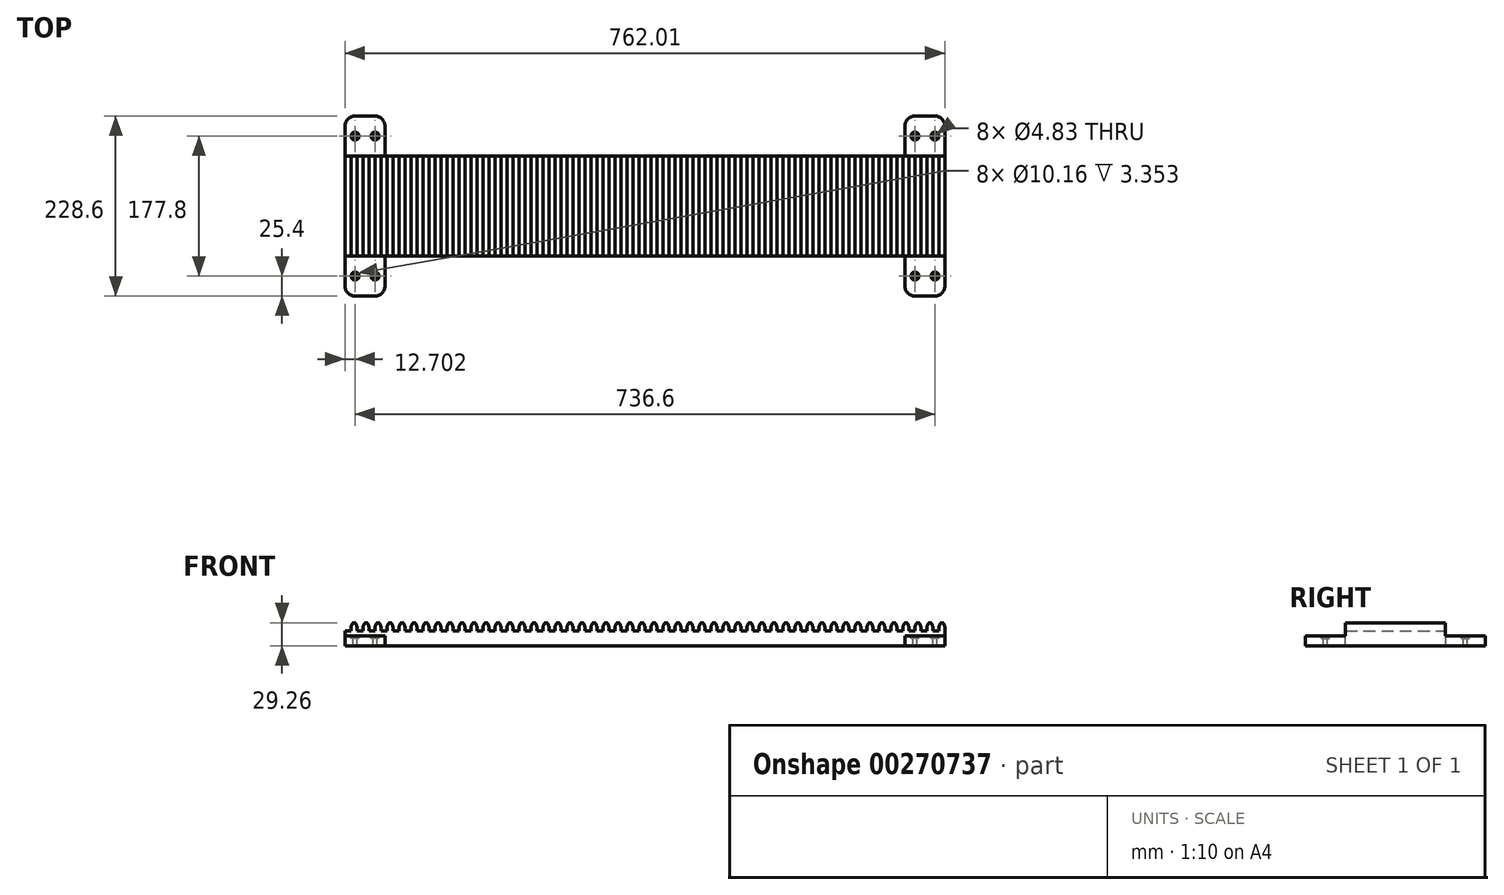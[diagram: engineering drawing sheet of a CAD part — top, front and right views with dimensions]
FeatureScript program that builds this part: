
annotation { "Feature Type Name" : "Feature", "Feature Type Description" : "" }
export const myFeature = defineFeature(function(context is Context, id is Id, definition is map)
    precondition{}
    {
        {
            var Q0;
            Q0=qCreatedBy(makeId("Front.planeOp"),FACE);
            var sketch = newSketch(context, id + "F0", { "sketchPlane" : qUnion([Q0])});
            skPoint(sketch, "E0.orphan", {"position": v(0.2, 56.91) * mm});
            skPoint(sketch, "E1.orphan", {"position": v(-3.78, 56.79) * mm});
            skArc(sketch, "E2.MirrorCS", {"start": v(-11.95, 74.44) * mm, "mid": v(-11.17, 76.23) * mm, "end": v(-10.29, 77.97) * mm});
            skArc(sketch, "E3.MirrorCS", {"start": v(-5.23, 74.46) * mm, "mid": v(-6, 76.24) * mm, "end": v(-6.88, 77.97) * mm});
            skPoint(sketch, "E4.orphan", {"position": v(-4.82, 78.33) * mm});
            skPoint(sketch, "E5.orphan", {"position": v(-12.38, 78.33) * mm});
            skPoint(sketch, "E6.visualSharp", {"position": v(-12.4, 73.25) * mm});
            skArc(sketch, "E6.filletArc", {"start": v(-11.95, 74.44) * mm, "mid": v(-12.28, 73.3) * mm, "end": v(-12.4, 72.11) * mm});
            skPoint(sketch, "E7.visualSharp", {"position": v(-4.77, 73.25) * mm});
            skArc(sketch, "E7.filletArc", {"start": v(-4.78, 72.1) * mm, "mid": v(-4.89, 73.3) * mm, "end": v(-5.23, 74.46) * mm});
            skPoint(sketch, "E8.visualSharp", {"position": v(-10.06, 78.38) * mm});
            skArc(sketch, "E8.filletArc", {"start": v(-9.6, 78.38) * mm, "mid": v(-10, 78.27) * mm, "end": v(-10.29, 77.97) * mm});
            skPoint(sketch, "E9.visualSharp", {"position": v(-7.1, 78.38) * mm});
            skArc(sketch, "E9.filletArc", {"start": v(-6.88, 77.97) * mm, "mid": v(-7.17, 78.27) * mm, "end": v(-7.57, 78.38) * mm});
            skLineSegment(sketch, "E10", {"start": v(-4.78, 72.1) * mm, "end": v(-4.79, 68.17) * mm});
            skLineSegment(sketch, "E11", {"start": v(-12.4, 72.11) * mm, "end": v(-12.4, 68.17) * mm});
            skLineSegment(sketch, "E12", {"start": v(-9.6, 78.38) * mm, "end": v(-7.57, 78.38) * mm});
            skLineSegment(sketch, "E13", {"start": v(-12.4, 68.17) * mm, "end": v(-4.79, 68.17) * mm});
            skPoint(sketch, "E14.orphan", {"position": v(-14.13, 68.17) * mm});
            skLineSegment(sketch, "E15", {"start": v(-12.4, 68.17) * mm, "end": v(2.83, 68.17) * mm});
            skPoint(sketch, "E16.1.0.0", {"position": v(5.18, 78.38) * mm});
            skArc(sketch, "E16.1.0.1", {"start": v(10.01, 74.46) * mm, "mid": v(9.24, 76.24) * mm, "end": v(8.36, 77.97) * mm});
            skArc(sketch, "E16.1.0.2", {"start": v(3.3, 74.44) * mm, "mid": v(4.07, 76.23) * mm, "end": v(4.95, 77.97) * mm});
            skPoint(sketch, "E16.1.0.3", {"position": v(10.42, 78.33) * mm});
            skPoint(sketch, "E16.1.0.4", {"position": v(2.85, 73.25) * mm});
            skPoint(sketch, "E16.1.0.5", {"position": v(10.47, 73.25) * mm});
            skPoint(sketch, "E16.1.0.6", {"position": v(1.11, 68.17) * mm});
            skLineSegment(sketch, "E16.1.0.7", {"start": v(5.64, 78.38) * mm, "end": v(7.67, 78.38) * mm});
            skPoint(sketch, "E16.1.0.8", {"position": v(8.13, 78.38) * mm});
            skLineSegment(sketch, "E16.1.0.9", {"start": v(10.46, 72.1) * mm, "end": v(10.45, 68.17) * mm});
            skLineSegment(sketch, "E16.1.0.10", {"start": v(2.83, 68.17) * mm, "end": v(18.07, 68.17) * mm});
            skPoint(sketch, "E16.1.0.11", {"position": v(2.86, 78.33) * mm});
            skLineSegment(sketch, "E16.1.0.12", {"start": v(2.84, 72.11) * mm, "end": v(2.83, 68.17) * mm});
            skArc(sketch, "E16.1.0.13", {"start": v(10.46, 72.1) * mm, "mid": v(10.35, 73.3) * mm, "end": v(10.01, 74.46) * mm});
            skArc(sketch, "E16.1.0.14", {"start": v(3.3, 74.44) * mm, "mid": v(2.96, 73.3) * mm, "end": v(2.84, 72.11) * mm});
            skLineSegment(sketch, "E16.1.0.15", {"start": v(2.83, 68.17) * mm, "end": v(10.45, 68.17) * mm});
            skArc(sketch, "E16.1.0.16", {"start": v(8.36, 77.97) * mm, "mid": v(8.07, 78.27) * mm, "end": v(7.67, 78.38) * mm});
            skArc(sketch, "E16.1.0.17", {"start": v(5.64, 78.38) * mm, "mid": v(5.24, 78.27) * mm, "end": v(4.95, 77.97) * mm});
            skPoint(sketch, "E16.2.0.0", {"position": v(20.42, 78.38) * mm});
            skArc(sketch, "E16.2.0.1", {"start": v(25.25, 74.46) * mm, "mid": v(24.48, 76.24) * mm, "end": v(23.6, 77.97) * mm});
            skArc(sketch, "E16.2.0.2", {"start": v(18.53, 74.44) * mm, "mid": v(19.3, 76.23) * mm, "end": v(20.2, 77.97) * mm});
            skPoint(sketch, "E16.2.0.3", {"position": v(25.66, 78.33) * mm});
            skPoint(sketch, "E16.2.0.4", {"position": v(18.09, 73.25) * mm});
            skPoint(sketch, "E16.2.0.5", {"position": v(25.7, 73.25) * mm});
            skPoint(sketch, "E16.2.0.6", {"position": v(16.35, 68.17) * mm});
            skLineSegment(sketch, "E16.2.0.7", {"start": v(20.88, 78.38) * mm, "end": v(22.9, 78.38) * mm});
            skPoint(sketch, "E16.2.0.8", {"position": v(23.37, 78.38) * mm});
            skLineSegment(sketch, "E16.2.0.9", {"start": v(25.7, 72.1) * mm, "end": v(25.7, 68.17) * mm});
            skLineSegment(sketch, "E16.2.0.10", {"start": v(18.07, 68.17) * mm, "end": v(33.31, 68.17) * mm});
            skPoint(sketch, "E16.2.0.11", {"position": v(18.1, 78.33) * mm});
            skLineSegment(sketch, "E16.2.0.12", {"start": v(18.08, 72.11) * mm, "end": v(18.07, 68.17) * mm});
            skArc(sketch, "E16.2.0.13", {"start": v(25.7, 72.1) * mm, "mid": v(25.6, 73.3) * mm, "end": v(25.25, 74.46) * mm});
            skArc(sketch, "E16.2.0.14", {"start": v(18.53, 74.44) * mm, "mid": v(18.2, 73.3) * mm, "end": v(18.08, 72.11) * mm});
            skLineSegment(sketch, "E16.2.0.15", {"start": v(18.07, 68.17) * mm, "end": v(25.7, 68.17) * mm});
            skArc(sketch, "E16.2.0.16", {"start": v(23.6, 77.97) * mm, "mid": v(23.31, 78.27) * mm, "end": v(22.9, 78.38) * mm});
            skArc(sketch, "E16.2.0.17", {"start": v(20.88, 78.38) * mm, "mid": v(20.48, 78.27) * mm, "end": v(20.2, 77.97) * mm});
            skPoint(sketch, "E17.0.3.0", {"position": v(35.66, 78.38) * mm});
            skArc(sketch, "E17.1.3.0", {"start": v(40.5, 74.46) * mm, "mid": v(39.72, 76.24) * mm, "end": v(38.84, 77.97) * mm});
            skArc(sketch, "E17.5.3.0", {"start": v(33.77, 74.44) * mm, "mid": v(34.55, 76.23) * mm, "end": v(35.43, 77.97) * mm});
            skPoint(sketch, "E17.9.3.0", {"position": v(40.9, 78.33) * mm});
            skPoint(sketch, "E17.10.3.0", {"position": v(33.33, 73.25) * mm});
            skPoint(sketch, "E17.11.3.0", {"position": v(40.95, 73.25) * mm});
            skPoint(sketch, "E17.12.3.0", {"position": v(31.6, 68.17) * mm});
            skLineSegment(sketch, "E17.13.3.0", {"start": v(36.12, 78.38) * mm, "end": v(38.15, 78.38) * mm});
            skPoint(sketch, "E17.16.3.0", {"position": v(38.61, 78.38) * mm});
            skLineSegment(sketch, "E17.17.3.0", {"start": v(40.94, 72.1) * mm, "end": v(40.93, 68.17) * mm});
            skLineSegment(sketch, "E17.20.3.0", {"start": v(33.31, 68.17) * mm, "end": v(48.55, 68.17) * mm});
            skPoint(sketch, "E17.23.3.0", {"position": v(33.34, 78.33) * mm});
            skLineSegment(sketch, "E17.24.3.0", {"start": v(33.32, 72.11) * mm, "end": v(33.31, 68.17) * mm});
            skArc(sketch, "E17.27.3.0", {"start": v(40.94, 72.1) * mm, "mid": v(40.83, 73.3) * mm, "end": v(40.5, 74.46) * mm});
            skArc(sketch, "E17.31.3.0", {"start": v(33.77, 74.44) * mm, "mid": v(33.44, 73.3) * mm, "end": v(33.32, 72.11) * mm});
            skLineSegment(sketch, "E17.35.3.0", {"start": v(33.31, 68.17) * mm, "end": v(40.93, 68.17) * mm});
            skArc(sketch, "E17.38.3.0", {"start": v(38.84, 77.97) * mm, "mid": v(38.55, 78.27) * mm, "end": v(38.15, 78.38) * mm});
            skArc(sketch, "E17.42.3.0", {"start": v(36.12, 78.38) * mm, "mid": v(35.72, 78.27) * mm, "end": v(35.43, 77.97) * mm});
            skPoint(sketch, "E17.0.4.0", {"position": v(50.9, 78.38) * mm});
            skArc(sketch, "E17.1.4.0", {"start": v(55.73, 74.46) * mm, "mid": v(54.96, 76.24) * mm, "end": v(54.08, 77.97) * mm});
            skArc(sketch, "E17.5.4.0", {"start": v(49.01, 74.44) * mm, "mid": v(49.79, 76.23) * mm, "end": v(50.67, 77.97) * mm});
            skPoint(sketch, "E17.9.4.0", {"position": v(56.14, 78.33) * mm});
            skPoint(sketch, "E17.10.4.0", {"position": v(48.57, 73.25) * mm});
            skPoint(sketch, "E17.11.4.0", {"position": v(56.19, 73.25) * mm});
            skPoint(sketch, "E17.12.4.0", {"position": v(46.83, 68.17) * mm});
            skLineSegment(sketch, "E17.13.4.0", {"start": v(51.36, 78.38) * mm, "end": v(53.39, 78.38) * mm});
            skPoint(sketch, "E17.16.4.0", {"position": v(53.85, 78.38) * mm});
            skLineSegment(sketch, "E17.17.4.0", {"start": v(56.18, 72.1) * mm, "end": v(56.17, 68.17) * mm});
            skLineSegment(sketch, "E17.20.4.0", {"start": v(48.55, 68.17) * mm, "end": v(63.8, 68.17) * mm});
            skPoint(sketch, "E17.23.4.0", {"position": v(48.58, 78.33) * mm});
            skLineSegment(sketch, "E17.24.4.0", {"start": v(48.56, 72.11) * mm, "end": v(48.55, 68.17) * mm});
            skArc(sketch, "E17.27.4.0", {"start": v(56.18, 72.1) * mm, "mid": v(56.07, 73.3) * mm, "end": v(55.73, 74.46) * mm});
            skArc(sketch, "E17.31.4.0", {"start": v(49.01, 74.44) * mm, "mid": v(48.68, 73.3) * mm, "end": v(48.56, 72.11) * mm});
            skLineSegment(sketch, "E17.35.4.0", {"start": v(48.55, 68.17) * mm, "end": v(56.17, 68.17) * mm});
            skArc(sketch, "E17.38.4.0", {"start": v(54.08, 77.97) * mm, "mid": v(53.8, 78.27) * mm, "end": v(53.39, 78.38) * mm});
            skArc(sketch, "E17.42.4.0", {"start": v(51.36, 78.38) * mm, "mid": v(50.96, 78.27) * mm, "end": v(50.67, 77.97) * mm});
            skPoint(sketch, "E17.0.5.0", {"position": v(66.14, 78.38) * mm});
            skArc(sketch, "E17.1.5.0", {"start": v(70.97, 74.46) * mm, "mid": v(70.2, 76.24) * mm, "end": v(69.32, 77.97) * mm});
            skArc(sketch, "E17.5.5.0", {"start": v(64.25, 74.44) * mm, "mid": v(65.03, 76.23) * mm, "end": v(65.91, 77.97) * mm});
            skPoint(sketch, "E17.9.5.0", {"position": v(71.38, 78.33) * mm});
            skPoint(sketch, "E17.10.5.0", {"position": v(63.8, 73.25) * mm});
            skPoint(sketch, "E17.11.5.0", {"position": v(71.43, 73.25) * mm});
            skPoint(sketch, "E17.12.5.0", {"position": v(62.07, 68.17) * mm});
            skLineSegment(sketch, "E17.13.5.0", {"start": v(66.6, 78.38) * mm, "end": v(68.63, 78.38) * mm});
            skPoint(sketch, "E17.16.5.0", {"position": v(69.1, 78.38) * mm});
            skLineSegment(sketch, "E17.17.5.0", {"start": v(71.42, 72.1) * mm, "end": v(71.41, 68.17) * mm});
            skLineSegment(sketch, "E17.20.5.0", {"start": v(63.8, 68.17) * mm, "end": v(79.03, 68.17) * mm});
            skPoint(sketch, "E17.23.5.0", {"position": v(63.82, 78.33) * mm});
            skLineSegment(sketch, "E17.24.5.0", {"start": v(63.8, 72.11) * mm, "end": v(63.8, 68.17) * mm});
            skArc(sketch, "E17.27.5.0", {"start": v(71.42, 72.1) * mm, "mid": v(71.31, 73.3) * mm, "end": v(70.97, 74.46) * mm});
            skArc(sketch, "E17.31.5.0", {"start": v(64.25, 74.44) * mm, "mid": v(63.92, 73.3) * mm, "end": v(63.8, 72.11) * mm});
            skLineSegment(sketch, "E17.35.5.0", {"start": v(63.8, 68.17) * mm, "end": v(71.41, 68.17) * mm});
            skArc(sketch, "E17.38.5.0", {"start": v(69.32, 77.97) * mm, "mid": v(69.03, 78.27) * mm, "end": v(68.63, 78.38) * mm});
            skArc(sketch, "E17.42.5.0", {"start": v(66.6, 78.38) * mm, "mid": v(66.2, 78.27) * mm, "end": v(65.91, 77.97) * mm});
            skPoint(sketch, "E17.0.6.0", {"position": v(81.38, 78.38) * mm});
            skArc(sketch, "E17.1.6.0", {"start": v(86.21, 74.46) * mm, "mid": v(85.44, 76.24) * mm, "end": v(84.56, 77.97) * mm});
            skArc(sketch, "E17.5.6.0", {"start": v(79.5, 74.44) * mm, "mid": v(80.27, 76.23) * mm, "end": v(81.15, 77.97) * mm});
            skPoint(sketch, "E17.9.6.0", {"position": v(86.62, 78.33) * mm});
            skPoint(sketch, "E17.10.6.0", {"position": v(79.05, 73.25) * mm});
            skPoint(sketch, "E17.11.6.0", {"position": v(86.67, 73.25) * mm});
            skPoint(sketch, "E17.12.6.0", {"position": v(77.31, 68.17) * mm});
            skLineSegment(sketch, "E17.13.6.0", {"start": v(81.84, 78.38) * mm, "end": v(83.87, 78.38) * mm});
            skPoint(sketch, "E17.16.6.0", {"position": v(84.33, 78.38) * mm});
            skLineSegment(sketch, "E17.17.6.0", {"start": v(86.66, 72.1) * mm, "end": v(86.65, 68.17) * mm});
            skLineSegment(sketch, "E17.20.6.0", {"start": v(79.03, 68.17) * mm, "end": v(94.27, 68.17) * mm});
            skPoint(sketch, "E17.23.6.0", {"position": v(79.06, 78.33) * mm});
            skLineSegment(sketch, "E17.24.6.0", {"start": v(79.04, 72.11) * mm, "end": v(79.03, 68.17) * mm});
            skArc(sketch, "E17.27.6.0", {"start": v(86.66, 72.1) * mm, "mid": v(86.55, 73.3) * mm, "end": v(86.21, 74.46) * mm});
            skArc(sketch, "E17.31.6.0", {"start": v(79.5, 74.44) * mm, "mid": v(79.16, 73.3) * mm, "end": v(79.04, 72.11) * mm});
            skLineSegment(sketch, "E17.35.6.0", {"start": v(79.03, 68.17) * mm, "end": v(86.65, 68.17) * mm});
            skArc(sketch, "E17.38.6.0", {"start": v(84.56, 77.97) * mm, "mid": v(84.27, 78.27) * mm, "end": v(83.87, 78.38) * mm});
            skArc(sketch, "E17.42.6.0", {"start": v(81.84, 78.38) * mm, "mid": v(81.44, 78.27) * mm, "end": v(81.15, 77.97) * mm});
            skPoint(sketch, "E17.0.7.0", {"position": v(96.62, 78.38) * mm});
            skArc(sketch, "E17.1.7.0", {"start": v(101.45, 74.46) * mm, "mid": v(100.68, 76.24) * mm, "end": v(99.8, 77.97) * mm});
            skArc(sketch, "E17.5.7.0", {"start": v(94.73, 74.44) * mm, "mid": v(95.5, 76.23) * mm, "end": v(96.4, 77.97) * mm});
            skPoint(sketch, "E17.9.7.0", {"position": v(101.86, 78.33) * mm});
            skPoint(sketch, "E17.10.7.0", {"position": v(94.29, 73.25) * mm});
            skPoint(sketch, "E17.11.7.0", {"position": v(101.9, 73.25) * mm});
            skPoint(sketch, "E17.12.7.0", {"position": v(92.55, 68.17) * mm});
            skLineSegment(sketch, "E17.13.7.0", {"start": v(97.08, 78.38) * mm, "end": v(99.1, 78.38) * mm});
            skPoint(sketch, "E17.16.7.0", {"position": v(99.57, 78.38) * mm});
            skLineSegment(sketch, "E17.17.7.0", {"start": v(101.9, 72.1) * mm, "end": v(101.9, 68.17) * mm});
            skLineSegment(sketch, "E17.20.7.0", {"start": v(94.27, 68.17) * mm, "end": v(109.51, 68.17) * mm});
            skPoint(sketch, "E17.23.7.0", {"position": v(94.3, 78.33) * mm});
            skLineSegment(sketch, "E17.24.7.0", {"start": v(94.28, 72.11) * mm, "end": v(94.27, 68.17) * mm});
            skArc(sketch, "E17.27.7.0", {"start": v(101.9, 72.1) * mm, "mid": v(101.8, 73.3) * mm, "end": v(101.45, 74.46) * mm});
            skArc(sketch, "E17.31.7.0", {"start": v(94.73, 74.44) * mm, "mid": v(94.4, 73.3) * mm, "end": v(94.28, 72.11) * mm});
            skLineSegment(sketch, "E17.35.7.0", {"start": v(94.27, 68.17) * mm, "end": v(101.9, 68.17) * mm});
            skArc(sketch, "E17.38.7.0", {"start": v(99.8, 77.97) * mm, "mid": v(99.51, 78.27) * mm, "end": v(99.1, 78.38) * mm});
            skArc(sketch, "E17.42.7.0", {"start": v(97.08, 78.38) * mm, "mid": v(96.68, 78.27) * mm, "end": v(96.4, 77.97) * mm});
            skPoint(sketch, "E17.0.8.0", {"position": v(111.86, 78.38) * mm});
            skArc(sketch, "E17.1.8.0", {"start": v(116.7, 74.46) * mm, "mid": v(115.92, 76.24) * mm, "end": v(115.04, 77.97) * mm});
            skArc(sketch, "E17.5.8.0", {"start": v(109.97, 74.44) * mm, "mid": v(110.75, 76.23) * mm, "end": v(111.63, 77.97) * mm});
            skPoint(sketch, "E17.9.8.0", {"position": v(117.1, 78.33) * mm});
            skPoint(sketch, "E17.10.8.0", {"position": v(109.53, 73.25) * mm});
            skPoint(sketch, "E17.11.8.0", {"position": v(117.15, 73.25) * mm});
            skPoint(sketch, "E17.12.8.0", {"position": v(107.8, 68.17) * mm});
            skLineSegment(sketch, "E17.13.8.0", {"start": v(112.32, 78.38) * mm, "end": v(114.35, 78.38) * mm});
            skPoint(sketch, "E17.16.8.0", {"position": v(114.81, 78.38) * mm});
            skLineSegment(sketch, "E17.17.8.0", {"start": v(117.14, 72.1) * mm, "end": v(117.13, 68.17) * mm});
            skLineSegment(sketch, "E17.20.8.0", {"start": v(109.51, 68.17) * mm, "end": v(124.75, 68.17) * mm});
            skPoint(sketch, "E17.23.8.0", {"position": v(109.54, 78.33) * mm});
            skLineSegment(sketch, "E17.24.8.0", {"start": v(109.52, 72.11) * mm, "end": v(109.51, 68.17) * mm});
            skArc(sketch, "E17.27.8.0", {"start": v(117.14, 72.1) * mm, "mid": v(117.03, 73.3) * mm, "end": v(116.7, 74.46) * mm});
            skArc(sketch, "E17.31.8.0", {"start": v(109.97, 74.44) * mm, "mid": v(109.64, 73.3) * mm, "end": v(109.52, 72.11) * mm});
            skLineSegment(sketch, "E17.35.8.0", {"start": v(109.51, 68.17) * mm, "end": v(117.13, 68.17) * mm});
            skArc(sketch, "E17.38.8.0", {"start": v(115.04, 77.97) * mm, "mid": v(114.75, 78.27) * mm, "end": v(114.35, 78.38) * mm});
            skArc(sketch, "E17.42.8.0", {"start": v(112.32, 78.38) * mm, "mid": v(111.92, 78.27) * mm, "end": v(111.63, 77.97) * mm});
            skPoint(sketch, "E17.0.9.0", {"position": v(127.1, 78.38) * mm});
            skArc(sketch, "E17.1.9.0", {"start": v(131.93, 74.46) * mm, "mid": v(131.16, 76.24) * mm, "end": v(130.28, 77.97) * mm});
            skArc(sketch, "E17.5.9.0", {"start": v(125.21, 74.44) * mm, "mid": v(125.99, 76.23) * mm, "end": v(126.87, 77.97) * mm});
            skPoint(sketch, "E17.9.9.0", {"position": v(132.34, 78.33) * mm});
            skPoint(sketch, "E17.10.9.0", {"position": v(124.77, 73.25) * mm});
            skPoint(sketch, "E17.11.9.0", {"position": v(132.39, 73.25) * mm});
            skPoint(sketch, "E17.12.9.0", {"position": v(123.03, 68.17) * mm});
            skLineSegment(sketch, "E17.13.9.0", {"start": v(127.56, 78.38) * mm, "end": v(129.59, 78.38) * mm});
            skPoint(sketch, "E17.16.9.0", {"position": v(130.05, 78.38) * mm});
            skLineSegment(sketch, "E17.17.9.0", {"start": v(132.38, 72.1) * mm, "end": v(132.37, 68.17) * mm});
            skLineSegment(sketch, "E17.20.9.0", {"start": v(124.75, 68.17) * mm, "end": v(140, 68.17) * mm});
            skPoint(sketch, "E17.23.9.0", {"position": v(124.78, 78.33) * mm});
            skLineSegment(sketch, "E17.24.9.0", {"start": v(124.76, 72.11) * mm, "end": v(124.75, 68.17) * mm});
            skArc(sketch, "E17.27.9.0", {"start": v(132.38, 72.1) * mm, "mid": v(132.27, 73.3) * mm, "end": v(131.93, 74.46) * mm});
            skArc(sketch, "E17.31.9.0", {"start": v(125.21, 74.44) * mm, "mid": v(124.88, 73.3) * mm, "end": v(124.76, 72.11) * mm});
            skLineSegment(sketch, "E17.35.9.0", {"start": v(124.75, 68.17) * mm, "end": v(132.37, 68.17) * mm});
            skArc(sketch, "E17.38.9.0", {"start": v(130.28, 77.97) * mm, "mid": v(130, 78.27) * mm, "end": v(129.59, 78.38) * mm});
            skArc(sketch, "E17.42.9.0", {"start": v(127.56, 78.38) * mm, "mid": v(127.16, 78.27) * mm, "end": v(126.87, 77.97) * mm});
            skPoint(sketch, "E17.0.10.0", {"position": v(142.34, 78.38) * mm});
            skArc(sketch, "E17.1.10.0", {"start": v(147.17, 74.46) * mm, "mid": v(146.4, 76.24) * mm, "end": v(145.52, 77.97) * mm});
            skArc(sketch, "E17.5.10.0", {"start": v(140.45, 74.44) * mm, "mid": v(141.23, 76.23) * mm, "end": v(142.11, 77.97) * mm});
            skPoint(sketch, "E17.9.10.0", {"position": v(147.58, 78.33) * mm});
            skPoint(sketch, "E17.10.10.0", {"position": v(140, 73.25) * mm});
            skPoint(sketch, "E17.11.10.0", {"position": v(147.63, 73.25) * mm});
            skPoint(sketch, "E17.12.10.0", {"position": v(138.27, 68.17) * mm});
            skLineSegment(sketch, "E17.13.10.0", {"start": v(142.8, 78.38) * mm, "end": v(144.83, 78.38) * mm});
            skPoint(sketch, "E17.16.10.0", {"position": v(145.3, 78.38) * mm});
            skLineSegment(sketch, "E17.17.10.0", {"start": v(147.62, 72.1) * mm, "end": v(147.61, 68.17) * mm});
            skLineSegment(sketch, "E17.20.10.0", {"start": v(140, 68.17) * mm, "end": v(155.23, 68.17) * mm});
            skPoint(sketch, "E17.23.10.0", {"position": v(140.02, 78.33) * mm});
            skLineSegment(sketch, "E17.24.10.0", {"start": v(140, 72.11) * mm, "end": v(140, 68.17) * mm});
            skArc(sketch, "E17.27.10.0", {"start": v(147.62, 72.1) * mm, "mid": v(147.51, 73.3) * mm, "end": v(147.17, 74.46) * mm});
            skArc(sketch, "E17.31.10.0", {"start": v(140.45, 74.44) * mm, "mid": v(140.12, 73.3) * mm, "end": v(140, 72.11) * mm});
            skLineSegment(sketch, "E17.35.10.0", {"start": v(140, 68.17) * mm, "end": v(147.61, 68.17) * mm});
            skArc(sketch, "E17.38.10.0", {"start": v(145.52, 77.97) * mm, "mid": v(145.23, 78.27) * mm, "end": v(144.83, 78.38) * mm});
            skArc(sketch, "E17.42.10.0", {"start": v(142.8, 78.38) * mm, "mid": v(142.4, 78.27) * mm, "end": v(142.11, 77.97) * mm});
            skPoint(sketch, "E17.0.11.0", {"position": v(157.58, 78.38) * mm});
            skArc(sketch, "E17.1.11.0", {"start": v(162.41, 74.46) * mm, "mid": v(161.64, 76.24) * mm, "end": v(160.76, 77.97) * mm});
            skArc(sketch, "E17.5.11.0", {"start": v(155.7, 74.44) * mm, "mid": v(156.47, 76.23) * mm, "end": v(157.35, 77.97) * mm});
            skPoint(sketch, "E17.9.11.0", {"position": v(162.82, 78.33) * mm});
            skPoint(sketch, "E17.10.11.0", {"position": v(155.25, 73.25) * mm});
            skPoint(sketch, "E17.11.11.0", {"position": v(162.87, 73.25) * mm});
            skPoint(sketch, "E17.12.11.0", {"position": v(153.51, 68.17) * mm});
            skLineSegment(sketch, "E17.13.11.0", {"start": v(158.04, 78.38) * mm, "end": v(160.07, 78.38) * mm});
            skPoint(sketch, "E17.16.11.0", {"position": v(160.53, 78.38) * mm});
            skLineSegment(sketch, "E17.17.11.0", {"start": v(162.86, 72.1) * mm, "end": v(162.85, 68.17) * mm});
            skLineSegment(sketch, "E17.20.11.0", {"start": v(155.23, 68.17) * mm, "end": v(170.47, 68.17) * mm});
            skPoint(sketch, "E17.23.11.0", {"position": v(155.26, 78.33) * mm});
            skLineSegment(sketch, "E17.24.11.0", {"start": v(155.24, 72.11) * mm, "end": v(155.23, 68.17) * mm});
            skArc(sketch, "E17.27.11.0", {"start": v(162.86, 72.1) * mm, "mid": v(162.75, 73.3) * mm, "end": v(162.41, 74.46) * mm});
            skArc(sketch, "E17.31.11.0", {"start": v(155.7, 74.44) * mm, "mid": v(155.36, 73.3) * mm, "end": v(155.24, 72.11) * mm});
            skLineSegment(sketch, "E17.35.11.0", {"start": v(155.23, 68.17) * mm, "end": v(162.85, 68.17) * mm});
            skArc(sketch, "E17.38.11.0", {"start": v(160.76, 77.97) * mm, "mid": v(160.47, 78.27) * mm, "end": v(160.07, 78.38) * mm});
            skArc(sketch, "E17.42.11.0", {"start": v(158.04, 78.38) * mm, "mid": v(157.64, 78.27) * mm, "end": v(157.35, 77.97) * mm});
            skPoint(sketch, "E17.0.12.0", {"position": v(172.82, 78.38) * mm});
            skArc(sketch, "E17.1.12.0", {"start": v(177.65, 74.46) * mm, "mid": v(176.88, 76.24) * mm, "end": v(176, 77.97) * mm});
            skArc(sketch, "E17.5.12.0", {"start": v(170.93, 74.44) * mm, "mid": v(171.7, 76.23) * mm, "end": v(172.6, 77.97) * mm});
            skPoint(sketch, "E17.9.12.0", {"position": v(178.06, 78.33) * mm});
            skPoint(sketch, "E17.10.12.0", {"position": v(170.49, 73.25) * mm});
            skPoint(sketch, "E17.11.12.0", {"position": v(178.1, 73.25) * mm});
            skPoint(sketch, "E17.12.12.0", {"position": v(168.75, 68.17) * mm});
            skLineSegment(sketch, "E17.13.12.0", {"start": v(173.28, 78.38) * mm, "end": v(175.3, 78.38) * mm});
            skPoint(sketch, "E17.16.12.0", {"position": v(175.77, 78.38) * mm});
            skLineSegment(sketch, "E17.17.12.0", {"start": v(178.1, 72.1) * mm, "end": v(178.1, 68.17) * mm});
            skLineSegment(sketch, "E17.20.12.0", {"start": v(170.47, 68.17) * mm, "end": v(185.71, 68.17) * mm});
            skPoint(sketch, "E17.23.12.0", {"position": v(170.5, 78.33) * mm});
            skLineSegment(sketch, "E17.24.12.0", {"start": v(170.48, 72.11) * mm, "end": v(170.47, 68.17) * mm});
            skArc(sketch, "E17.27.12.0", {"start": v(178.1, 72.1) * mm, "mid": v(178, 73.3) * mm, "end": v(177.65, 74.46) * mm});
            skArc(sketch, "E17.31.12.0", {"start": v(170.93, 74.44) * mm, "mid": v(170.6, 73.3) * mm, "end": v(170.48, 72.11) * mm});
            skLineSegment(sketch, "E17.35.12.0", {"start": v(170.47, 68.17) * mm, "end": v(178.1, 68.17) * mm});
            skArc(sketch, "E17.38.12.0", {"start": v(176, 77.97) * mm, "mid": v(175.71, 78.27) * mm, "end": v(175.3, 78.38) * mm});
            skArc(sketch, "E17.42.12.0", {"start": v(173.28, 78.38) * mm, "mid": v(172.88, 78.27) * mm, "end": v(172.6, 77.97) * mm});
            skPoint(sketch, "E17.0.13.0", {"position": v(188.06, 78.38) * mm});
            skArc(sketch, "E17.1.13.0", {"start": v(192.9, 74.46) * mm, "mid": v(192.12, 76.24) * mm, "end": v(191.24, 77.97) * mm});
            skArc(sketch, "E17.5.13.0", {"start": v(186.17, 74.44) * mm, "mid": v(186.95, 76.23) * mm, "end": v(187.83, 77.97) * mm});
            skPoint(sketch, "E17.9.13.0", {"position": v(193.3, 78.33) * mm});
            skPoint(sketch, "E17.10.13.0", {"position": v(185.73, 73.25) * mm});
            skPoint(sketch, "E17.11.13.0", {"position": v(193.35, 73.25) * mm});
            skPoint(sketch, "E17.12.13.0", {"position": v(184, 68.17) * mm});
            skLineSegment(sketch, "E17.13.13.0", {"start": v(188.52, 78.38) * mm, "end": v(190.55, 78.38) * mm});
            skPoint(sketch, "E17.16.13.0", {"position": v(191.01, 78.38) * mm});
            skLineSegment(sketch, "E17.17.13.0", {"start": v(193.34, 72.1) * mm, "end": v(193.33, 68.17) * mm});
            skLineSegment(sketch, "E17.20.13.0", {"start": v(185.71, 68.17) * mm, "end": v(200.95, 68.17) * mm});
            skPoint(sketch, "E17.23.13.0", {"position": v(185.74, 78.33) * mm});
            skLineSegment(sketch, "E17.24.13.0", {"start": v(185.72, 72.11) * mm, "end": v(185.71, 68.17) * mm});
            skArc(sketch, "E17.27.13.0", {"start": v(193.34, 72.1) * mm, "mid": v(193.23, 73.3) * mm, "end": v(192.9, 74.46) * mm});
            skArc(sketch, "E17.31.13.0", {"start": v(186.17, 74.44) * mm, "mid": v(185.84, 73.3) * mm, "end": v(185.72, 72.11) * mm});
            skLineSegment(sketch, "E17.35.13.0", {"start": v(185.71, 68.17) * mm, "end": v(193.33, 68.17) * mm});
            skArc(sketch, "E17.38.13.0", {"start": v(191.24, 77.97) * mm, "mid": v(190.95, 78.27) * mm, "end": v(190.55, 78.38) * mm});
            skArc(sketch, "E17.42.13.0", {"start": v(188.52, 78.38) * mm, "mid": v(188.12, 78.27) * mm, "end": v(187.83, 77.97) * mm});
            skPoint(sketch, "E17.0.14.0", {"position": v(203.3, 78.38) * mm});
            skArc(sketch, "E17.1.14.0", {"start": v(208.13, 74.46) * mm, "mid": v(207.36, 76.24) * mm, "end": v(206.48, 77.97) * mm});
            skArc(sketch, "E17.5.14.0", {"start": v(201.41, 74.44) * mm, "mid": v(202.19, 76.23) * mm, "end": v(203.07, 77.97) * mm});
            skPoint(sketch, "E17.9.14.0", {"position": v(208.54, 78.33) * mm});
            skPoint(sketch, "E17.10.14.0", {"position": v(200.97, 73.25) * mm});
            skPoint(sketch, "E17.11.14.0", {"position": v(208.59, 73.25) * mm});
            skPoint(sketch, "E17.12.14.0", {"position": v(199.23, 68.17) * mm});
            skLineSegment(sketch, "E17.13.14.0", {"start": v(203.76, 78.38) * mm, "end": v(205.79, 78.38) * mm});
            skPoint(sketch, "E17.16.14.0", {"position": v(206.25, 78.38) * mm});
            skLineSegment(sketch, "E17.17.14.0", {"start": v(208.58, 72.1) * mm, "end": v(208.57, 68.17) * mm});
            skLineSegment(sketch, "E17.20.14.0", {"start": v(200.95, 68.17) * mm, "end": v(216.2, 68.17) * mm});
            skPoint(sketch, "E17.23.14.0", {"position": v(200.98, 78.33) * mm});
            skLineSegment(sketch, "E17.24.14.0", {"start": v(200.96, 72.11) * mm, "end": v(200.95, 68.17) * mm});
            skArc(sketch, "E17.27.14.0", {"start": v(208.58, 72.1) * mm, "mid": v(208.47, 73.3) * mm, "end": v(208.13, 74.46) * mm});
            skArc(sketch, "E17.31.14.0", {"start": v(201.41, 74.44) * mm, "mid": v(201.08, 73.3) * mm, "end": v(200.96, 72.11) * mm});
            skLineSegment(sketch, "E17.35.14.0", {"start": v(200.95, 68.17) * mm, "end": v(208.57, 68.17) * mm});
            skArc(sketch, "E17.38.14.0", {"start": v(206.48, 77.97) * mm, "mid": v(206.2, 78.27) * mm, "end": v(205.79, 78.38) * mm});
            skArc(sketch, "E17.42.14.0", {"start": v(203.76, 78.38) * mm, "mid": v(203.36, 78.27) * mm, "end": v(203.07, 77.97) * mm});
            skPoint(sketch, "E17.0.15.0", {"position": v(218.54, 78.38) * mm});
            skArc(sketch, "E17.1.15.0", {"start": v(223.37, 74.46) * mm, "mid": v(222.6, 76.24) * mm, "end": v(221.72, 77.97) * mm});
            skArc(sketch, "E17.5.15.0", {"start": v(216.65, 74.44) * mm, "mid": v(217.43, 76.23) * mm, "end": v(218.31, 77.97) * mm});
            skPoint(sketch, "E17.9.15.0", {"position": v(223.78, 78.33) * mm});
            skPoint(sketch, "E17.10.15.0", {"position": v(216.2, 73.25) * mm});
            skPoint(sketch, "E17.11.15.0", {"position": v(223.83, 73.25) * mm});
            skPoint(sketch, "E17.12.15.0", {"position": v(214.47, 68.17) * mm});
            skLineSegment(sketch, "E17.13.15.0", {"start": v(219, 78.38) * mm, "end": v(221.03, 78.38) * mm});
            skPoint(sketch, "E17.16.15.0", {"position": v(221.5, 78.38) * mm});
            skLineSegment(sketch, "E17.17.15.0", {"start": v(223.82, 72.1) * mm, "end": v(223.81, 68.17) * mm});
            skLineSegment(sketch, "E17.20.15.0", {"start": v(216.2, 68.17) * mm, "end": v(231.43, 68.17) * mm});
            skPoint(sketch, "E17.23.15.0", {"position": v(216.22, 78.33) * mm});
            skLineSegment(sketch, "E17.24.15.0", {"start": v(216.2, 72.11) * mm, "end": v(216.2, 68.17) * mm});
            skArc(sketch, "E17.27.15.0", {"start": v(223.82, 72.1) * mm, "mid": v(223.71, 73.3) * mm, "end": v(223.37, 74.46) * mm});
            skArc(sketch, "E17.31.15.0", {"start": v(216.65, 74.44) * mm, "mid": v(216.32, 73.3) * mm, "end": v(216.2, 72.11) * mm});
            skLineSegment(sketch, "E17.35.15.0", {"start": v(216.2, 68.17) * mm, "end": v(223.81, 68.17) * mm});
            skArc(sketch, "E17.38.15.0", {"start": v(221.72, 77.97) * mm, "mid": v(221.43, 78.27) * mm, "end": v(221.03, 78.38) * mm});
            skArc(sketch, "E17.42.15.0", {"start": v(219, 78.38) * mm, "mid": v(218.6, 78.27) * mm, "end": v(218.31, 77.97) * mm});
            skPoint(sketch, "E17.0.16.0", {"position": v(233.78, 78.38) * mm});
            skArc(sketch, "E17.1.16.0", {"start": v(238.61, 74.46) * mm, "mid": v(237.84, 76.24) * mm, "end": v(236.96, 77.97) * mm});
            skArc(sketch, "E17.5.16.0", {"start": v(231.9, 74.44) * mm, "mid": v(232.67, 76.23) * mm, "end": v(233.55, 77.97) * mm});
            skPoint(sketch, "E17.9.16.0", {"position": v(239.02, 78.33) * mm});
            skPoint(sketch, "E17.10.16.0", {"position": v(231.45, 73.25) * mm});
            skPoint(sketch, "E17.11.16.0", {"position": v(239.07, 73.25) * mm});
            skPoint(sketch, "E17.12.16.0", {"position": v(229.71, 68.17) * mm});
            skLineSegment(sketch, "E17.13.16.0", {"start": v(234.24, 78.38) * mm, "end": v(236.27, 78.38) * mm});
            skPoint(sketch, "E17.16.16.0", {"position": v(236.73, 78.38) * mm});
            skLineSegment(sketch, "E17.17.16.0", {"start": v(239.06, 72.1) * mm, "end": v(239.05, 68.17) * mm});
            skLineSegment(sketch, "E17.20.16.0", {"start": v(231.43, 68.17) * mm, "end": v(246.67, 68.17) * mm});
            skPoint(sketch, "E17.23.16.0", {"position": v(231.46, 78.33) * mm});
            skLineSegment(sketch, "E17.24.16.0", {"start": v(231.44, 72.11) * mm, "end": v(231.43, 68.17) * mm});
            skArc(sketch, "E17.27.16.0", {"start": v(239.06, 72.1) * mm, "mid": v(238.95, 73.3) * mm, "end": v(238.61, 74.46) * mm});
            skArc(sketch, "E17.31.16.0", {"start": v(231.9, 74.44) * mm, "mid": v(231.56, 73.3) * mm, "end": v(231.44, 72.11) * mm});
            skLineSegment(sketch, "E17.35.16.0", {"start": v(231.43, 68.17) * mm, "end": v(239.05, 68.17) * mm});
            skArc(sketch, "E17.38.16.0", {"start": v(236.96, 77.97) * mm, "mid": v(236.67, 78.27) * mm, "end": v(236.27, 78.38) * mm});
            skArc(sketch, "E17.42.16.0", {"start": v(234.24, 78.38) * mm, "mid": v(233.84, 78.27) * mm, "end": v(233.55, 77.97) * mm});
            skPoint(sketch, "E17.0.17.0", {"position": v(249.02, 78.38) * mm});
            skArc(sketch, "E17.1.17.0", {"start": v(253.85, 74.46) * mm, "mid": v(253.08, 76.24) * mm, "end": v(252.2, 77.97) * mm});
            skArc(sketch, "E17.5.17.0", {"start": v(247.13, 74.44) * mm, "mid": v(247.9, 76.23) * mm, "end": v(248.8, 77.97) * mm});
            skPoint(sketch, "E17.9.17.0", {"position": v(254.26, 78.33) * mm});
            skPoint(sketch, "E17.10.17.0", {"position": v(246.69, 73.25) * mm});
            skPoint(sketch, "E17.11.17.0", {"position": v(254.3, 73.25) * mm});
            skPoint(sketch, "E17.12.17.0", {"position": v(244.95, 68.17) * mm});
            skLineSegment(sketch, "E17.13.17.0", {"start": v(249.48, 78.38) * mm, "end": v(251.5, 78.38) * mm});
            skPoint(sketch, "E17.16.17.0", {"position": v(251.97, 78.38) * mm});
            skLineSegment(sketch, "E17.17.17.0", {"start": v(254.3, 72.1) * mm, "end": v(254.3, 68.17) * mm});
            skLineSegment(sketch, "E17.20.17.0", {"start": v(246.67, 68.17) * mm, "end": v(261.91, 68.17) * mm});
            skPoint(sketch, "E17.23.17.0", {"position": v(246.7, 78.33) * mm});
            skLineSegment(sketch, "E17.24.17.0", {"start": v(246.68, 72.11) * mm, "end": v(246.67, 68.17) * mm});
            skArc(sketch, "E17.27.17.0", {"start": v(254.3, 72.1) * mm, "mid": v(254.2, 73.3) * mm, "end": v(253.85, 74.46) * mm});
            skArc(sketch, "E17.31.17.0", {"start": v(247.13, 74.44) * mm, "mid": v(246.8, 73.3) * mm, "end": v(246.68, 72.11) * mm});
            skLineSegment(sketch, "E17.35.17.0", {"start": v(246.67, 68.17) * mm, "end": v(254.3, 68.17) * mm});
            skArc(sketch, "E17.38.17.0", {"start": v(252.2, 77.97) * mm, "mid": v(251.91, 78.27) * mm, "end": v(251.5, 78.38) * mm});
            skArc(sketch, "E17.42.17.0", {"start": v(249.48, 78.38) * mm, "mid": v(249.08, 78.27) * mm, "end": v(248.8, 77.97) * mm});
            skPoint(sketch, "E17.0.18.0", {"position": v(264.26, 78.38) * mm});
            skArc(sketch, "E17.1.18.0", {"start": v(269.1, 74.46) * mm, "mid": v(268.32, 76.24) * mm, "end": v(267.44, 77.97) * mm});
            skArc(sketch, "E17.5.18.0", {"start": v(262.37, 74.44) * mm, "mid": v(263.15, 76.23) * mm, "end": v(264.03, 77.97) * mm});
            skPoint(sketch, "E17.9.18.0", {"position": v(269.5, 78.33) * mm});
            skPoint(sketch, "E17.10.18.0", {"position": v(261.93, 73.25) * mm});
            skPoint(sketch, "E17.11.18.0", {"position": v(269.55, 73.25) * mm});
            skPoint(sketch, "E17.12.18.0", {"position": v(260.2, 68.17) * mm});
            skLineSegment(sketch, "E17.13.18.0", {"start": v(264.72, 78.38) * mm, "end": v(266.75, 78.38) * mm});
            skPoint(sketch, "E17.16.18.0", {"position": v(267.21, 78.38) * mm});
            skLineSegment(sketch, "E17.17.18.0", {"start": v(269.54, 72.1) * mm, "end": v(269.53, 68.17) * mm});
            skLineSegment(sketch, "E17.20.18.0", {"start": v(261.91, 68.17) * mm, "end": v(277.15, 68.17) * mm});
            skPoint(sketch, "E17.23.18.0", {"position": v(261.94, 78.33) * mm});
            skLineSegment(sketch, "E17.24.18.0", {"start": v(261.92, 72.11) * mm, "end": v(261.91, 68.17) * mm});
            skArc(sketch, "E17.27.18.0", {"start": v(269.54, 72.1) * mm, "mid": v(269.43, 73.3) * mm, "end": v(269.1, 74.46) * mm});
            skArc(sketch, "E17.31.18.0", {"start": v(262.37, 74.44) * mm, "mid": v(262.04, 73.3) * mm, "end": v(261.92, 72.11) * mm});
            skLineSegment(sketch, "E17.35.18.0", {"start": v(261.91, 68.17) * mm, "end": v(269.53, 68.17) * mm});
            skArc(sketch, "E17.38.18.0", {"start": v(267.44, 77.97) * mm, "mid": v(267.15, 78.27) * mm, "end": v(266.75, 78.38) * mm});
            skArc(sketch, "E17.42.18.0", {"start": v(264.72, 78.38) * mm, "mid": v(264.32, 78.27) * mm, "end": v(264.03, 77.97) * mm});
            skPoint(sketch, "E17.0.19.0", {"position": v(279.5, 78.38) * mm});
            skArc(sketch, "E17.1.19.0", {"start": v(284.33, 74.46) * mm, "mid": v(283.56, 76.24) * mm, "end": v(282.68, 77.97) * mm});
            skArc(sketch, "E17.5.19.0", {"start": v(277.61, 74.44) * mm, "mid": v(278.39, 76.23) * mm, "end": v(279.27, 77.97) * mm});
            skPoint(sketch, "E17.9.19.0", {"position": v(284.74, 78.33) * mm});
            skPoint(sketch, "E17.10.19.0", {"position": v(277.17, 73.25) * mm});
            skPoint(sketch, "E17.11.19.0", {"position": v(284.79, 73.25) * mm});
            skPoint(sketch, "E17.12.19.0", {"position": v(275.43, 68.17) * mm});
            skLineSegment(sketch, "E17.13.19.0", {"start": v(279.96, 78.38) * mm, "end": v(281.99, 78.38) * mm});
            skPoint(sketch, "E17.16.19.0", {"position": v(282.45, 78.38) * mm});
            skLineSegment(sketch, "E17.17.19.0", {"start": v(284.78, 72.1) * mm, "end": v(284.77, 68.17) * mm});
            skLineSegment(sketch, "E17.20.19.0", {"start": v(277.15, 68.17) * mm, "end": v(292.4, 68.17) * mm});
            skPoint(sketch, "E17.23.19.0", {"position": v(277.18, 78.33) * mm});
            skLineSegment(sketch, "E17.24.19.0", {"start": v(277.16, 72.11) * mm, "end": v(277.15, 68.17) * mm});
            skArc(sketch, "E17.27.19.0", {"start": v(284.78, 72.1) * mm, "mid": v(284.67, 73.3) * mm, "end": v(284.33, 74.46) * mm});
            skArc(sketch, "E17.31.19.0", {"start": v(277.61, 74.44) * mm, "mid": v(277.28, 73.3) * mm, "end": v(277.16, 72.11) * mm});
            skLineSegment(sketch, "E17.35.19.0", {"start": v(277.15, 68.17) * mm, "end": v(284.77, 68.17) * mm});
            skArc(sketch, "E17.38.19.0", {"start": v(282.68, 77.97) * mm, "mid": v(282.4, 78.27) * mm, "end": v(281.99, 78.38) * mm});
            skArc(sketch, "E17.42.19.0", {"start": v(279.96, 78.38) * mm, "mid": v(279.56, 78.27) * mm, "end": v(279.27, 77.97) * mm});
            skPoint(sketch, "E17.0.20.0", {"position": v(294.74, 78.38) * mm});
            skArc(sketch, "E17.1.20.0", {"start": v(299.57, 74.46) * mm, "mid": v(298.8, 76.24) * mm, "end": v(297.92, 77.97) * mm});
            skArc(sketch, "E17.5.20.0", {"start": v(292.85, 74.44) * mm, "mid": v(293.63, 76.23) * mm, "end": v(294.51, 77.97) * mm});
            skPoint(sketch, "E17.9.20.0", {"position": v(299.98, 78.33) * mm});
            skPoint(sketch, "E17.10.20.0", {"position": v(292.4, 73.25) * mm});
            skPoint(sketch, "E17.11.20.0", {"position": v(300.03, 73.25) * mm});
            skPoint(sketch, "E17.12.20.0", {"position": v(290.67, 68.17) * mm});
            skLineSegment(sketch, "E17.13.20.0", {"start": v(295.2, 78.38) * mm, "end": v(297.23, 78.38) * mm});
            skPoint(sketch, "E17.16.20.0", {"position": v(297.7, 78.38) * mm});
            skLineSegment(sketch, "E17.17.20.0", {"start": v(300.02, 72.1) * mm, "end": v(300.01, 68.17) * mm});
            skLineSegment(sketch, "E17.20.20.0", {"start": v(292.4, 68.17) * mm, "end": v(307.63, 68.17) * mm});
            skPoint(sketch, "E17.23.20.0", {"position": v(292.42, 78.33) * mm});
            skLineSegment(sketch, "E17.24.20.0", {"start": v(292.4, 72.11) * mm, "end": v(292.4, 68.17) * mm});
            skArc(sketch, "E17.27.20.0", {"start": v(300.02, 72.1) * mm, "mid": v(299.91, 73.3) * mm, "end": v(299.57, 74.46) * mm});
            skArc(sketch, "E17.31.20.0", {"start": v(292.85, 74.44) * mm, "mid": v(292.52, 73.3) * mm, "end": v(292.4, 72.11) * mm});
            skLineSegment(sketch, "E17.35.20.0", {"start": v(292.4, 68.17) * mm, "end": v(300.01, 68.17) * mm});
            skArc(sketch, "E17.38.20.0", {"start": v(297.92, 77.97) * mm, "mid": v(297.63, 78.27) * mm, "end": v(297.23, 78.38) * mm});
            skArc(sketch, "E17.42.20.0", {"start": v(295.2, 78.38) * mm, "mid": v(294.8, 78.27) * mm, "end": v(294.51, 77.97) * mm});
            skPoint(sketch, "E17.0.21.0", {"position": v(309.98, 78.38) * mm});
            skArc(sketch, "E17.1.21.0", {"start": v(314.81, 74.46) * mm, "mid": v(314.04, 76.24) * mm, "end": v(313.16, 77.97) * mm});
            skArc(sketch, "E17.5.21.0", {"start": v(308.1, 74.44) * mm, "mid": v(308.87, 76.23) * mm, "end": v(309.75, 77.97) * mm});
            skPoint(sketch, "E17.9.21.0", {"position": v(315.22, 78.33) * mm});
            skPoint(sketch, "E17.10.21.0", {"position": v(307.65, 73.25) * mm});
            skPoint(sketch, "E17.11.21.0", {"position": v(315.27, 73.25) * mm});
            skPoint(sketch, "E17.12.21.0", {"position": v(305.91, 68.17) * mm});
            skLineSegment(sketch, "E17.13.21.0", {"start": v(310.44, 78.38) * mm, "end": v(312.47, 78.38) * mm});
            skPoint(sketch, "E17.16.21.0", {"position": v(312.93, 78.38) * mm});
            skLineSegment(sketch, "E17.17.21.0", {"start": v(315.26, 72.1) * mm, "end": v(315.25, 68.17) * mm});
            skLineSegment(sketch, "E17.20.21.0", {"start": v(307.63, 68.17) * mm, "end": v(322.87, 68.17) * mm});
            skPoint(sketch, "E17.23.21.0", {"position": v(307.66, 78.33) * mm});
            skLineSegment(sketch, "E17.24.21.0", {"start": v(307.64, 72.11) * mm, "end": v(307.63, 68.17) * mm});
            skArc(sketch, "E17.27.21.0", {"start": v(315.26, 72.1) * mm, "mid": v(315.15, 73.3) * mm, "end": v(314.81, 74.46) * mm});
            skArc(sketch, "E17.31.21.0", {"start": v(308.1, 74.44) * mm, "mid": v(307.76, 73.3) * mm, "end": v(307.64, 72.11) * mm});
            skLineSegment(sketch, "E17.35.21.0", {"start": v(307.63, 68.17) * mm, "end": v(315.25, 68.17) * mm});
            skArc(sketch, "E17.38.21.0", {"start": v(313.16, 77.97) * mm, "mid": v(312.87, 78.27) * mm, "end": v(312.47, 78.38) * mm});
            skArc(sketch, "E17.42.21.0", {"start": v(310.44, 78.38) * mm, "mid": v(310.04, 78.27) * mm, "end": v(309.75, 77.97) * mm});
            skPoint(sketch, "E17.0.22.0", {"position": v(325.22, 78.38) * mm});
            skArc(sketch, "E17.1.22.0", {"start": v(330.05, 74.46) * mm, "mid": v(329.28, 76.24) * mm, "end": v(328.4, 77.97) * mm});
            skArc(sketch, "E17.5.22.0", {"start": v(323.33, 74.44) * mm, "mid": v(324.1, 76.23) * mm, "end": v(325, 77.97) * mm});
            skPoint(sketch, "E17.9.22.0", {"position": v(330.46, 78.33) * mm});
            skPoint(sketch, "E17.10.22.0", {"position": v(322.89, 73.25) * mm});
            skPoint(sketch, "E17.11.22.0", {"position": v(330.5, 73.25) * mm});
            skPoint(sketch, "E17.12.22.0", {"position": v(321.15, 68.17) * mm});
            skLineSegment(sketch, "E17.13.22.0", {"start": v(325.68, 78.38) * mm, "end": v(327.7, 78.38) * mm});
            skPoint(sketch, "E17.16.22.0", {"position": v(328.17, 78.38) * mm});
            skLineSegment(sketch, "E17.17.22.0", {"start": v(330.5, 72.1) * mm, "end": v(330.5, 68.17) * mm});
            skLineSegment(sketch, "E17.20.22.0", {"start": v(322.87, 68.17) * mm, "end": v(338.11, 68.17) * mm});
            skPoint(sketch, "E17.23.22.0", {"position": v(322.9, 78.33) * mm});
            skLineSegment(sketch, "E17.24.22.0", {"start": v(322.88, 72.11) * mm, "end": v(322.87, 68.17) * mm});
            skArc(sketch, "E17.27.22.0", {"start": v(330.5, 72.1) * mm, "mid": v(330.4, 73.3) * mm, "end": v(330.05, 74.46) * mm});
            skArc(sketch, "E17.31.22.0", {"start": v(323.33, 74.44) * mm, "mid": v(323, 73.3) * mm, "end": v(322.88, 72.11) * mm});
            skLineSegment(sketch, "E17.35.22.0", {"start": v(322.87, 68.17) * mm, "end": v(330.5, 68.17) * mm});
            skArc(sketch, "E17.38.22.0", {"start": v(328.4, 77.97) * mm, "mid": v(328.11, 78.27) * mm, "end": v(327.7, 78.38) * mm});
            skArc(sketch, "E17.42.22.0", {"start": v(325.68, 78.38) * mm, "mid": v(325.28, 78.27) * mm, "end": v(325, 77.97) * mm});
            skPoint(sketch, "E17.0.23.0", {"position": v(340.46, 78.38) * mm});
            skArc(sketch, "E17.1.23.0", {"start": v(345.3, 74.46) * mm, "mid": v(344.52, 76.24) * mm, "end": v(343.64, 77.97) * mm});
            skArc(sketch, "E17.5.23.0", {"start": v(338.57, 74.44) * mm, "mid": v(339.35, 76.23) * mm, "end": v(340.23, 77.97) * mm});
            skPoint(sketch, "E17.9.23.0", {"position": v(345.7, 78.33) * mm});
            skPoint(sketch, "E17.10.23.0", {"position": v(338.13, 73.25) * mm});
            skPoint(sketch, "E17.11.23.0", {"position": v(345.75, 73.25) * mm});
            skPoint(sketch, "E17.12.23.0", {"position": v(336.4, 68.17) * mm});
            skLineSegment(sketch, "E17.13.23.0", {"start": v(340.92, 78.38) * mm, "end": v(342.95, 78.38) * mm});
            skPoint(sketch, "E17.16.23.0", {"position": v(343.41, 78.38) * mm});
            skLineSegment(sketch, "E17.17.23.0", {"start": v(345.74, 72.1) * mm, "end": v(345.73, 68.17) * mm});
            skLineSegment(sketch, "E17.20.23.0", {"start": v(338.11, 68.17) * mm, "end": v(353.35, 68.17) * mm});
            skPoint(sketch, "E17.23.23.0", {"position": v(338.14, 78.33) * mm});
            skLineSegment(sketch, "E17.24.23.0", {"start": v(338.12, 72.11) * mm, "end": v(338.11, 68.17) * mm});
            skArc(sketch, "E17.27.23.0", {"start": v(345.74, 72.1) * mm, "mid": v(345.63, 73.3) * mm, "end": v(345.3, 74.46) * mm});
            skArc(sketch, "E17.31.23.0", {"start": v(338.57, 74.44) * mm, "mid": v(338.24, 73.3) * mm, "end": v(338.12, 72.11) * mm});
            skLineSegment(sketch, "E17.35.23.0", {"start": v(338.11, 68.17) * mm, "end": v(345.73, 68.17) * mm});
            skArc(sketch, "E17.38.23.0", {"start": v(343.64, 77.97) * mm, "mid": v(343.35, 78.27) * mm, "end": v(342.95, 78.38) * mm});
            skArc(sketch, "E17.42.23.0", {"start": v(340.92, 78.38) * mm, "mid": v(340.52, 78.27) * mm, "end": v(340.23, 77.97) * mm});
            skPoint(sketch, "E17.0.24.0", {"position": v(355.7, 78.38) * mm});
            skArc(sketch, "E17.1.24.0", {"start": v(360.53, 74.46) * mm, "mid": v(359.76, 76.24) * mm, "end": v(358.88, 77.97) * mm});
            skArc(sketch, "E17.5.24.0", {"start": v(353.81, 74.44) * mm, "mid": v(354.59, 76.23) * mm, "end": v(355.47, 77.97) * mm});
            skPoint(sketch, "E17.9.24.0", {"position": v(360.94, 78.33) * mm});
            skPoint(sketch, "E17.10.24.0", {"position": v(353.37, 73.25) * mm});
            skPoint(sketch, "E17.11.24.0", {"position": v(360.99, 73.25) * mm});
            skPoint(sketch, "E17.12.24.0", {"position": v(351.63, 68.17) * mm});
            skLineSegment(sketch, "E17.13.24.0", {"start": v(356.16, 78.38) * mm, "end": v(358.19, 78.38) * mm});
            skPoint(sketch, "E17.16.24.0", {"position": v(358.65, 78.38) * mm});
            skLineSegment(sketch, "E17.17.24.0", {"start": v(360.98, 72.1) * mm, "end": v(360.97, 68.17) * mm});
            skLineSegment(sketch, "E17.20.24.0", {"start": v(353.35, 68.17) * mm, "end": v(368.6, 68.17) * mm});
            skPoint(sketch, "E17.23.24.0", {"position": v(353.38, 78.33) * mm});
            skLineSegment(sketch, "E17.24.24.0", {"start": v(353.36, 72.11) * mm, "end": v(353.35, 68.17) * mm});
            skArc(sketch, "E17.27.24.0", {"start": v(360.98, 72.1) * mm, "mid": v(360.87, 73.3) * mm, "end": v(360.53, 74.46) * mm});
            skArc(sketch, "E17.31.24.0", {"start": v(353.81, 74.44) * mm, "mid": v(353.48, 73.3) * mm, "end": v(353.36, 72.11) * mm});
            skLineSegment(sketch, "E17.35.24.0", {"start": v(353.35, 68.17) * mm, "end": v(360.97, 68.17) * mm});
            skArc(sketch, "E17.38.24.0", {"start": v(358.88, 77.97) * mm, "mid": v(358.6, 78.27) * mm, "end": v(358.19, 78.38) * mm});
            skArc(sketch, "E17.42.24.0", {"start": v(356.16, 78.38) * mm, "mid": v(355.76, 78.27) * mm, "end": v(355.47, 77.97) * mm});
            skPoint(sketch, "E17.0.25.0", {"position": v(370.94, 78.38) * mm});
            skArc(sketch, "E17.1.25.0", {"start": v(375.77, 74.46) * mm, "mid": v(375, 76.24) * mm, "end": v(374.12, 77.97) * mm});
            skArc(sketch, "E17.5.25.0", {"start": v(369.05, 74.44) * mm, "mid": v(369.83, 76.23) * mm, "end": v(370.71, 77.97) * mm});
            skPoint(sketch, "E17.9.25.0", {"position": v(376.18, 78.33) * mm});
            skPoint(sketch, "E17.10.25.0", {"position": v(368.6, 73.25) * mm});
            skPoint(sketch, "E17.11.25.0", {"position": v(376.23, 73.25) * mm});
            skPoint(sketch, "E17.12.25.0", {"position": v(366.87, 68.17) * mm});
            skLineSegment(sketch, "E17.13.25.0", {"start": v(371.4, 78.38) * mm, "end": v(373.43, 78.38) * mm});
            skPoint(sketch, "E17.16.25.0", {"position": v(373.9, 78.38) * mm});
            skLineSegment(sketch, "E17.17.25.0", {"start": v(376.22, 72.1) * mm, "end": v(376.21, 68.17) * mm});
            skLineSegment(sketch, "E17.20.25.0", {"start": v(368.6, 68.17) * mm, "end": v(383.83, 68.17) * mm});
            skPoint(sketch, "E17.23.25.0", {"position": v(368.62, 78.33) * mm});
            skLineSegment(sketch, "E17.24.25.0", {"start": v(368.6, 72.11) * mm, "end": v(368.6, 68.17) * mm});
            skArc(sketch, "E17.27.25.0", {"start": v(376.22, 72.1) * mm, "mid": v(376.11, 73.3) * mm, "end": v(375.77, 74.46) * mm});
            skArc(sketch, "E17.31.25.0", {"start": v(369.05, 74.44) * mm, "mid": v(368.72, 73.3) * mm, "end": v(368.6, 72.11) * mm});
            skLineSegment(sketch, "E17.35.25.0", {"start": v(368.6, 68.17) * mm, "end": v(376.21, 68.17) * mm});
            skArc(sketch, "E17.38.25.0", {"start": v(374.12, 77.97) * mm, "mid": v(373.83, 78.27) * mm, "end": v(373.43, 78.38) * mm});
            skArc(sketch, "E17.42.25.0", {"start": v(371.4, 78.38) * mm, "mid": v(371, 78.27) * mm, "end": v(370.71, 77.97) * mm});
            skPoint(sketch, "E17.0.26.0", {"position": v(386.18, 78.38) * mm});
            skArc(sketch, "E17.1.26.0", {"start": v(391.01, 74.46) * mm, "mid": v(390.24, 76.24) * mm, "end": v(389.36, 77.97) * mm});
            skArc(sketch, "E17.5.26.0", {"start": v(384.3, 74.44) * mm, "mid": v(385.07, 76.23) * mm, "end": v(385.95, 77.97) * mm});
            skPoint(sketch, "E17.9.26.0", {"position": v(391.42, 78.33) * mm});
            skPoint(sketch, "E17.10.26.0", {"position": v(383.85, 73.25) * mm});
            skPoint(sketch, "E17.11.26.0", {"position": v(391.47, 73.25) * mm});
            skPoint(sketch, "E17.12.26.0", {"position": v(382.11, 68.17) * mm});
            skLineSegment(sketch, "E17.13.26.0", {"start": v(386.64, 78.38) * mm, "end": v(388.67, 78.38) * mm});
            skPoint(sketch, "E17.16.26.0", {"position": v(389.13, 78.38) * mm});
            skLineSegment(sketch, "E17.17.26.0", {"start": v(391.46, 72.1) * mm, "end": v(391.45, 68.17) * mm});
            skLineSegment(sketch, "E17.20.26.0", {"start": v(383.83, 68.17) * mm, "end": v(399.07, 68.17) * mm});
            skPoint(sketch, "E17.23.26.0", {"position": v(383.86, 78.33) * mm});
            skLineSegment(sketch, "E17.24.26.0", {"start": v(383.84, 72.11) * mm, "end": v(383.83, 68.17) * mm});
            skArc(sketch, "E17.27.26.0", {"start": v(391.46, 72.1) * mm, "mid": v(391.35, 73.3) * mm, "end": v(391.01, 74.46) * mm});
            skArc(sketch, "E17.31.26.0", {"start": v(384.3, 74.44) * mm, "mid": v(383.96, 73.3) * mm, "end": v(383.84, 72.11) * mm});
            skLineSegment(sketch, "E17.35.26.0", {"start": v(383.83, 68.17) * mm, "end": v(391.45, 68.17) * mm});
            skArc(sketch, "E17.38.26.0", {"start": v(389.36, 77.97) * mm, "mid": v(389.07, 78.27) * mm, "end": v(388.67, 78.38) * mm});
            skArc(sketch, "E17.42.26.0", {"start": v(386.64, 78.38) * mm, "mid": v(386.24, 78.27) * mm, "end": v(385.95, 77.97) * mm});
            skPoint(sketch, "E17.0.27.0", {"position": v(401.42, 78.38) * mm});
            skArc(sketch, "E17.1.27.0", {"start": v(406.25, 74.46) * mm, "mid": v(405.48, 76.24) * mm, "end": v(404.6, 77.97) * mm});
            skArc(sketch, "E17.5.27.0", {"start": v(399.53, 74.44) * mm, "mid": v(400.3, 76.23) * mm, "end": v(401.2, 77.97) * mm});
            skPoint(sketch, "E17.9.27.0", {"position": v(406.66, 78.33) * mm});
            skPoint(sketch, "E17.10.27.0", {"position": v(399.09, 73.25) * mm});
            skPoint(sketch, "E17.11.27.0", {"position": v(406.7, 73.25) * mm});
            skPoint(sketch, "E17.12.27.0", {"position": v(397.35, 68.17) * mm});
            skLineSegment(sketch, "E17.13.27.0", {"start": v(401.88, 78.38) * mm, "end": v(403.9, 78.38) * mm});
            skPoint(sketch, "E17.16.27.0", {"position": v(404.37, 78.38) * mm});
            skLineSegment(sketch, "E17.17.27.0", {"start": v(406.7, 72.1) * mm, "end": v(406.7, 68.17) * mm});
            skLineSegment(sketch, "E17.20.27.0", {"start": v(399.07, 68.17) * mm, "end": v(414.31, 68.17) * mm});
            skPoint(sketch, "E17.23.27.0", {"position": v(399.1, 78.33) * mm});
            skLineSegment(sketch, "E17.24.27.0", {"start": v(399.08, 72.11) * mm, "end": v(399.07, 68.17) * mm});
            skArc(sketch, "E17.27.27.0", {"start": v(406.7, 72.1) * mm, "mid": v(406.6, 73.3) * mm, "end": v(406.25, 74.46) * mm});
            skArc(sketch, "E17.31.27.0", {"start": v(399.53, 74.44) * mm, "mid": v(399.2, 73.3) * mm, "end": v(399.08, 72.11) * mm});
            skLineSegment(sketch, "E17.35.27.0", {"start": v(399.07, 68.17) * mm, "end": v(406.7, 68.17) * mm});
            skArc(sketch, "E17.38.27.0", {"start": v(404.6, 77.97) * mm, "mid": v(404.31, 78.27) * mm, "end": v(403.9, 78.38) * mm});
            skArc(sketch, "E17.42.27.0", {"start": v(401.88, 78.38) * mm, "mid": v(401.48, 78.27) * mm, "end": v(401.2, 77.97) * mm});
            skPoint(sketch, "E17.0.28.0", {"position": v(416.66, 78.38) * mm});
            skArc(sketch, "E17.1.28.0", {"start": v(421.5, 74.46) * mm, "mid": v(420.72, 76.24) * mm, "end": v(419.84, 77.97) * mm});
            skArc(sketch, "E17.5.28.0", {"start": v(414.77, 74.44) * mm, "mid": v(415.55, 76.23) * mm, "end": v(416.43, 77.97) * mm});
            skPoint(sketch, "E17.9.28.0", {"position": v(421.9, 78.33) * mm});
            skPoint(sketch, "E17.10.28.0", {"position": v(414.33, 73.25) * mm});
            skPoint(sketch, "E17.11.28.0", {"position": v(421.95, 73.25) * mm});
            skPoint(sketch, "E17.12.28.0", {"position": v(412.6, 68.17) * mm});
            skLineSegment(sketch, "E17.13.28.0", {"start": v(417.12, 78.38) * mm, "end": v(419.15, 78.38) * mm});
            skPoint(sketch, "E17.16.28.0", {"position": v(419.61, 78.38) * mm});
            skLineSegment(sketch, "E17.17.28.0", {"start": v(421.94, 72.1) * mm, "end": v(421.93, 68.17) * mm});
            skLineSegment(sketch, "E17.20.28.0", {"start": v(414.31, 68.17) * mm, "end": v(429.55, 68.17) * mm});
            skPoint(sketch, "E17.23.28.0", {"position": v(414.34, 78.33) * mm});
            skLineSegment(sketch, "E17.24.28.0", {"start": v(414.32, 72.11) * mm, "end": v(414.31, 68.17) * mm});
            skArc(sketch, "E17.27.28.0", {"start": v(421.94, 72.1) * mm, "mid": v(421.83, 73.3) * mm, "end": v(421.5, 74.46) * mm});
            skArc(sketch, "E17.31.28.0", {"start": v(414.77, 74.44) * mm, "mid": v(414.44, 73.3) * mm, "end": v(414.32, 72.11) * mm});
            skLineSegment(sketch, "E17.35.28.0", {"start": v(414.31, 68.17) * mm, "end": v(421.93, 68.17) * mm});
            skArc(sketch, "E17.38.28.0", {"start": v(419.84, 77.97) * mm, "mid": v(419.55, 78.27) * mm, "end": v(419.15, 78.38) * mm});
            skArc(sketch, "E17.42.28.0", {"start": v(417.12, 78.38) * mm, "mid": v(416.72, 78.27) * mm, "end": v(416.43, 77.97) * mm});
            skPoint(sketch, "E17.0.29.0", {"position": v(431.9, 78.38) * mm});
            skArc(sketch, "E17.1.29.0", {"start": v(436.73, 74.46) * mm, "mid": v(435.96, 76.24) * mm, "end": v(435.08, 77.97) * mm});
            skArc(sketch, "E17.5.29.0", {"start": v(430.01, 74.44) * mm, "mid": v(430.79, 76.23) * mm, "end": v(431.67, 77.97) * mm});
            skPoint(sketch, "E17.9.29.0", {"position": v(437.14, 78.33) * mm});
            skPoint(sketch, "E17.10.29.0", {"position": v(429.57, 73.25) * mm});
            skPoint(sketch, "E17.11.29.0", {"position": v(437.19, 73.25) * mm});
            skPoint(sketch, "E17.12.29.0", {"position": v(427.83, 68.17) * mm});
            skLineSegment(sketch, "E17.13.29.0", {"start": v(432.36, 78.38) * mm, "end": v(434.39, 78.38) * mm});
            skPoint(sketch, "E17.16.29.0", {"position": v(434.85, 78.38) * mm});
            skLineSegment(sketch, "E17.17.29.0", {"start": v(437.18, 72.1) * mm, "end": v(437.17, 68.17) * mm});
            skLineSegment(sketch, "E17.20.29.0", {"start": v(429.55, 68.17) * mm, "end": v(444.8, 68.17) * mm});
            skPoint(sketch, "E17.23.29.0", {"position": v(429.58, 78.33) * mm});
            skLineSegment(sketch, "E17.24.29.0", {"start": v(429.56, 72.11) * mm, "end": v(429.55, 68.17) * mm});
            skArc(sketch, "E17.27.29.0", {"start": v(437.18, 72.1) * mm, "mid": v(437.07, 73.3) * mm, "end": v(436.73, 74.46) * mm});
            skArc(sketch, "E17.31.29.0", {"start": v(430.01, 74.44) * mm, "mid": v(429.68, 73.3) * mm, "end": v(429.56, 72.11) * mm});
            skLineSegment(sketch, "E17.35.29.0", {"start": v(429.55, 68.17) * mm, "end": v(437.17, 68.17) * mm});
            skArc(sketch, "E17.38.29.0", {"start": v(435.08, 77.97) * mm, "mid": v(434.8, 78.27) * mm, "end": v(434.39, 78.38) * mm});
            skArc(sketch, "E17.42.29.0", {"start": v(432.36, 78.38) * mm, "mid": v(431.96, 78.27) * mm, "end": v(431.67, 77.97) * mm});
            skPoint(sketch, "E17.0.30.0", {"position": v(447.14, 78.38) * mm});
            skArc(sketch, "E17.1.30.0", {"start": v(451.97, 74.46) * mm, "mid": v(451.2, 76.24) * mm, "end": v(450.32, 77.97) * mm});
            skArc(sketch, "E17.5.30.0", {"start": v(445.25, 74.44) * mm, "mid": v(446.03, 76.23) * mm, "end": v(446.91, 77.97) * mm});
            skPoint(sketch, "E17.9.30.0", {"position": v(452.38, 78.33) * mm});
            skPoint(sketch, "E17.10.30.0", {"position": v(444.8, 73.25) * mm});
            skPoint(sketch, "E17.11.30.0", {"position": v(452.43, 73.25) * mm});
            skPoint(sketch, "E17.12.30.0", {"position": v(443.07, 68.17) * mm});
            skLineSegment(sketch, "E17.13.30.0", {"start": v(447.6, 78.38) * mm, "end": v(449.63, 78.38) * mm});
            skPoint(sketch, "E17.16.30.0", {"position": v(450.1, 78.38) * mm});
            skLineSegment(sketch, "E17.17.30.0", {"start": v(452.42, 72.1) * mm, "end": v(452.41, 68.17) * mm});
            skLineSegment(sketch, "E17.20.30.0", {"start": v(444.8, 68.17) * mm, "end": v(460.03, 68.17) * mm});
            skPoint(sketch, "E17.23.30.0", {"position": v(444.82, 78.33) * mm});
            skLineSegment(sketch, "E17.24.30.0", {"start": v(444.8, 72.11) * mm, "end": v(444.8, 68.17) * mm});
            skArc(sketch, "E17.27.30.0", {"start": v(452.42, 72.1) * mm, "mid": v(452.31, 73.3) * mm, "end": v(451.97, 74.46) * mm});
            skArc(sketch, "E17.31.30.0", {"start": v(445.25, 74.44) * mm, "mid": v(444.92, 73.3) * mm, "end": v(444.8, 72.11) * mm});
            skLineSegment(sketch, "E17.35.30.0", {"start": v(444.8, 68.17) * mm, "end": v(452.41, 68.17) * mm});
            skArc(sketch, "E17.38.30.0", {"start": v(450.32, 77.97) * mm, "mid": v(450.03, 78.27) * mm, "end": v(449.63, 78.38) * mm});
            skArc(sketch, "E17.42.30.0", {"start": v(447.6, 78.38) * mm, "mid": v(447.2, 78.27) * mm, "end": v(446.91, 77.97) * mm});
            skPoint(sketch, "E17.0.31.0", {"position": v(462.38, 78.38) * mm});
            skArc(sketch, "E17.1.31.0", {"start": v(467.21, 74.46) * mm, "mid": v(466.44, 76.24) * mm, "end": v(465.56, 77.97) * mm});
            skArc(sketch, "E17.5.31.0", {"start": v(460.5, 74.44) * mm, "mid": v(461.27, 76.23) * mm, "end": v(462.15, 77.97) * mm});
            skPoint(sketch, "E17.9.31.0", {"position": v(467.62, 78.33) * mm});
            skPoint(sketch, "E17.10.31.0", {"position": v(460.05, 73.25) * mm});
            skPoint(sketch, "E17.11.31.0", {"position": v(467.67, 73.25) * mm});
            skPoint(sketch, "E17.12.31.0", {"position": v(458.31, 68.17) * mm});
            skLineSegment(sketch, "E17.13.31.0", {"start": v(462.84, 78.38) * mm, "end": v(464.87, 78.38) * mm});
            skPoint(sketch, "E17.16.31.0", {"position": v(465.33, 78.38) * mm});
            skLineSegment(sketch, "E17.17.31.0", {"start": v(467.66, 72.1) * mm, "end": v(467.65, 68.17) * mm});
            skLineSegment(sketch, "E17.20.31.0", {"start": v(460.03, 68.17) * mm, "end": v(475.27, 68.17) * mm});
            skPoint(sketch, "E17.23.31.0", {"position": v(460.06, 78.33) * mm});
            skLineSegment(sketch, "E17.24.31.0", {"start": v(460.04, 72.11) * mm, "end": v(460.03, 68.17) * mm});
            skArc(sketch, "E17.27.31.0", {"start": v(467.66, 72.1) * mm, "mid": v(467.55, 73.3) * mm, "end": v(467.21, 74.46) * mm});
            skArc(sketch, "E17.31.31.0", {"start": v(460.5, 74.44) * mm, "mid": v(460.16, 73.3) * mm, "end": v(460.04, 72.11) * mm});
            skLineSegment(sketch, "E17.35.31.0", {"start": v(460.03, 68.17) * mm, "end": v(467.65, 68.17) * mm});
            skArc(sketch, "E17.38.31.0", {"start": v(465.56, 77.97) * mm, "mid": v(465.27, 78.27) * mm, "end": v(464.87, 78.38) * mm});
            skArc(sketch, "E17.42.31.0", {"start": v(462.84, 78.38) * mm, "mid": v(462.44, 78.27) * mm, "end": v(462.15, 77.97) * mm});
            skPoint(sketch, "E17.0.32.0", {"position": v(477.62, 78.38) * mm});
            skArc(sketch, "E17.1.32.0", {"start": v(482.45, 74.46) * mm, "mid": v(481.68, 76.24) * mm, "end": v(480.8, 77.97) * mm});
            skArc(sketch, "E17.5.32.0", {"start": v(475.73, 74.44) * mm, "mid": v(476.5, 76.23) * mm, "end": v(477.4, 77.97) * mm});
            skPoint(sketch, "E17.9.32.0", {"position": v(482.86, 78.33) * mm});
            skPoint(sketch, "E17.10.32.0", {"position": v(475.29, 73.25) * mm});
            skPoint(sketch, "E17.11.32.0", {"position": v(482.9, 73.25) * mm});
            skPoint(sketch, "E17.12.32.0", {"position": v(473.55, 68.17) * mm});
            skLineSegment(sketch, "E17.13.32.0", {"start": v(478.08, 78.38) * mm, "end": v(480.1, 78.38) * mm});
            skPoint(sketch, "E17.16.32.0", {"position": v(480.57, 78.38) * mm});
            skLineSegment(sketch, "E17.17.32.0", {"start": v(482.9, 72.1) * mm, "end": v(482.9, 68.17) * mm});
            skLineSegment(sketch, "E17.20.32.0", {"start": v(475.27, 68.17) * mm, "end": v(490.51, 68.17) * mm});
            skPoint(sketch, "E17.23.32.0", {"position": v(475.3, 78.33) * mm});
            skLineSegment(sketch, "E17.24.32.0", {"start": v(475.28, 72.11) * mm, "end": v(475.27, 68.17) * mm});
            skArc(sketch, "E17.27.32.0", {"start": v(482.9, 72.1) * mm, "mid": v(482.8, 73.3) * mm, "end": v(482.45, 74.46) * mm});
            skArc(sketch, "E17.31.32.0", {"start": v(475.73, 74.44) * mm, "mid": v(475.4, 73.3) * mm, "end": v(475.28, 72.11) * mm});
            skLineSegment(sketch, "E17.35.32.0", {"start": v(475.27, 68.17) * mm, "end": v(482.9, 68.17) * mm});
            skArc(sketch, "E17.38.32.0", {"start": v(480.8, 77.97) * mm, "mid": v(480.51, 78.27) * mm, "end": v(480.1, 78.38) * mm});
            skArc(sketch, "E17.42.32.0", {"start": v(478.08, 78.38) * mm, "mid": v(477.68, 78.27) * mm, "end": v(477.4, 77.97) * mm});
            skPoint(sketch, "E17.0.33.0", {"position": v(492.86, 78.38) * mm});
            skArc(sketch, "E17.1.33.0", {"start": v(497.7, 74.46) * mm, "mid": v(496.92, 76.24) * mm, "end": v(496.04, 77.97) * mm});
            skArc(sketch, "E17.5.33.0", {"start": v(490.97, 74.44) * mm, "mid": v(491.75, 76.23) * mm, "end": v(492.63, 77.97) * mm});
            skPoint(sketch, "E17.9.33.0", {"position": v(498.1, 78.33) * mm});
            skPoint(sketch, "E17.10.33.0", {"position": v(490.53, 73.25) * mm});
            skPoint(sketch, "E17.11.33.0", {"position": v(498.15, 73.25) * mm});
            skPoint(sketch, "E17.12.33.0", {"position": v(488.8, 68.17) * mm});
            skLineSegment(sketch, "E17.13.33.0", {"start": v(493.32, 78.38) * mm, "end": v(495.35, 78.38) * mm});
            skPoint(sketch, "E17.16.33.0", {"position": v(495.81, 78.38) * mm});
            skLineSegment(sketch, "E17.17.33.0", {"start": v(498.14, 72.1) * mm, "end": v(498.13, 68.17) * mm});
            skLineSegment(sketch, "E17.20.33.0", {"start": v(490.51, 68.17) * mm, "end": v(505.75, 68.17) * mm});
            skPoint(sketch, "E17.23.33.0", {"position": v(490.54, 78.33) * mm});
            skLineSegment(sketch, "E17.24.33.0", {"start": v(490.52, 72.11) * mm, "end": v(490.51, 68.17) * mm});
            skArc(sketch, "E17.27.33.0", {"start": v(498.14, 72.1) * mm, "mid": v(498.03, 73.3) * mm, "end": v(497.7, 74.46) * mm});
            skArc(sketch, "E17.31.33.0", {"start": v(490.97, 74.44) * mm, "mid": v(490.64, 73.3) * mm, "end": v(490.52, 72.11) * mm});
            skLineSegment(sketch, "E17.35.33.0", {"start": v(490.51, 68.17) * mm, "end": v(498.13, 68.17) * mm});
            skArc(sketch, "E17.38.33.0", {"start": v(496.04, 77.97) * mm, "mid": v(495.75, 78.27) * mm, "end": v(495.35, 78.38) * mm});
            skArc(sketch, "E17.42.33.0", {"start": v(493.32, 78.38) * mm, "mid": v(492.92, 78.27) * mm, "end": v(492.63, 77.97) * mm});
            skPoint(sketch, "E17.0.34.0", {"position": v(508.1, 78.38) * mm});
            skArc(sketch, "E17.1.34.0", {"start": v(512.93, 74.46) * mm, "mid": v(512.16, 76.24) * mm, "end": v(511.28, 77.97) * mm});
            skArc(sketch, "E17.5.34.0", {"start": v(506.21, 74.44) * mm, "mid": v(506.99, 76.23) * mm, "end": v(507.87, 77.97) * mm});
            skPoint(sketch, "E17.9.34.0", {"position": v(513.34, 78.33) * mm});
            skPoint(sketch, "E17.10.34.0", {"position": v(505.77, 73.25) * mm});
            skPoint(sketch, "E17.11.34.0", {"position": v(513.39, 73.25) * mm});
            skPoint(sketch, "E17.12.34.0", {"position": v(504.03, 68.17) * mm});
            skLineSegment(sketch, "E17.13.34.0", {"start": v(508.56, 78.38) * mm, "end": v(510.59, 78.38) * mm});
            skPoint(sketch, "E17.16.34.0", {"position": v(511.05, 78.38) * mm});
            skLineSegment(sketch, "E17.17.34.0", {"start": v(513.38, 72.1) * mm, "end": v(513.37, 68.17) * mm});
            skLineSegment(sketch, "E17.20.34.0", {"start": v(505.75, 68.17) * mm, "end": v(521, 68.17) * mm});
            skPoint(sketch, "E17.23.34.0", {"position": v(505.78, 78.33) * mm});
            skLineSegment(sketch, "E17.24.34.0", {"start": v(505.76, 72.11) * mm, "end": v(505.75, 68.17) * mm});
            skArc(sketch, "E17.27.34.0", {"start": v(513.38, 72.1) * mm, "mid": v(513.27, 73.3) * mm, "end": v(512.93, 74.46) * mm});
            skArc(sketch, "E17.31.34.0", {"start": v(506.21, 74.44) * mm, "mid": v(505.88, 73.3) * mm, "end": v(505.76, 72.11) * mm});
            skLineSegment(sketch, "E17.35.34.0", {"start": v(505.75, 68.17) * mm, "end": v(513.37, 68.17) * mm});
            skArc(sketch, "E17.38.34.0", {"start": v(511.28, 77.97) * mm, "mid": v(511, 78.27) * mm, "end": v(510.59, 78.38) * mm});
            skArc(sketch, "E17.42.34.0", {"start": v(508.56, 78.38) * mm, "mid": v(508.16, 78.27) * mm, "end": v(507.87, 77.97) * mm});
            skPoint(sketch, "E17.0.35.0", {"position": v(523.34, 78.38) * mm});
            skArc(sketch, "E17.1.35.0", {"start": v(528.17, 74.46) * mm, "mid": v(527.4, 76.24) * mm, "end": v(526.52, 77.97) * mm});
            skArc(sketch, "E17.5.35.0", {"start": v(521.45, 74.44) * mm, "mid": v(522.23, 76.23) * mm, "end": v(523.11, 77.97) * mm});
            skPoint(sketch, "E17.9.35.0", {"position": v(528.58, 78.33) * mm});
            skPoint(sketch, "E17.10.35.0", {"position": v(521, 73.25) * mm});
            skPoint(sketch, "E17.11.35.0", {"position": v(528.63, 73.25) * mm});
            skPoint(sketch, "E17.12.35.0", {"position": v(519.27, 68.17) * mm});
            skLineSegment(sketch, "E17.13.35.0", {"start": v(523.8, 78.38) * mm, "end": v(525.83, 78.38) * mm});
            skPoint(sketch, "E17.16.35.0", {"position": v(526.3, 78.38) * mm});
            skLineSegment(sketch, "E17.17.35.0", {"start": v(528.62, 72.1) * mm, "end": v(528.61, 68.17) * mm});
            skLineSegment(sketch, "E17.20.35.0", {"start": v(521, 68.17) * mm, "end": v(536.23, 68.17) * mm});
            skPoint(sketch, "E17.23.35.0", {"position": v(521.02, 78.33) * mm});
            skLineSegment(sketch, "E17.24.35.0", {"start": v(521, 72.11) * mm, "end": v(521, 68.17) * mm});
            skArc(sketch, "E17.27.35.0", {"start": v(528.62, 72.1) * mm, "mid": v(528.51, 73.3) * mm, "end": v(528.17, 74.46) * mm});
            skArc(sketch, "E17.31.35.0", {"start": v(521.45, 74.44) * mm, "mid": v(521.12, 73.3) * mm, "end": v(521, 72.11) * mm});
            skLineSegment(sketch, "E17.35.35.0", {"start": v(521, 68.17) * mm, "end": v(528.61, 68.17) * mm});
            skArc(sketch, "E17.38.35.0", {"start": v(526.52, 77.97) * mm, "mid": v(526.23, 78.27) * mm, "end": v(525.83, 78.38) * mm});
            skArc(sketch, "E17.42.35.0", {"start": v(523.8, 78.38) * mm, "mid": v(523.4, 78.27) * mm, "end": v(523.11, 77.97) * mm});
            skPoint(sketch, "E17.0.36.0", {"position": v(538.58, 78.38) * mm});
            skArc(sketch, "E17.1.36.0", {"start": v(543.41, 74.46) * mm, "mid": v(542.64, 76.24) * mm, "end": v(541.76, 77.97) * mm});
            skArc(sketch, "E17.5.36.0", {"start": v(536.7, 74.44) * mm, "mid": v(537.47, 76.23) * mm, "end": v(538.35, 77.97) * mm});
            skPoint(sketch, "E17.9.36.0", {"position": v(543.82, 78.33) * mm});
            skPoint(sketch, "E17.10.36.0", {"position": v(536.25, 73.25) * mm});
            skPoint(sketch, "E17.11.36.0", {"position": v(543.87, 73.25) * mm});
            skPoint(sketch, "E17.12.36.0", {"position": v(534.51, 68.17) * mm});
            skLineSegment(sketch, "E17.13.36.0", {"start": v(539.04, 78.38) * mm, "end": v(541.07, 78.38) * mm});
            skPoint(sketch, "E17.16.36.0", {"position": v(541.53, 78.38) * mm});
            skLineSegment(sketch, "E17.17.36.0", {"start": v(543.86, 72.1) * mm, "end": v(543.85, 68.17) * mm});
            skLineSegment(sketch, "E17.20.36.0", {"start": v(536.23, 68.17) * mm, "end": v(551.47, 68.17) * mm});
            skPoint(sketch, "E17.23.36.0", {"position": v(536.26, 78.33) * mm});
            skLineSegment(sketch, "E17.24.36.0", {"start": v(536.24, 72.11) * mm, "end": v(536.23, 68.17) * mm});
            skArc(sketch, "E17.27.36.0", {"start": v(543.86, 72.1) * mm, "mid": v(543.75, 73.3) * mm, "end": v(543.41, 74.46) * mm});
            skArc(sketch, "E17.31.36.0", {"start": v(536.7, 74.44) * mm, "mid": v(536.36, 73.3) * mm, "end": v(536.24, 72.11) * mm});
            skLineSegment(sketch, "E17.35.36.0", {"start": v(536.23, 68.17) * mm, "end": v(543.85, 68.17) * mm});
            skArc(sketch, "E17.38.36.0", {"start": v(541.76, 77.97) * mm, "mid": v(541.47, 78.27) * mm, "end": v(541.07, 78.38) * mm});
            skArc(sketch, "E17.42.36.0", {"start": v(539.04, 78.38) * mm, "mid": v(538.64, 78.27) * mm, "end": v(538.35, 77.97) * mm});
            skPoint(sketch, "E17.0.37.0", {"position": v(553.82, 78.38) * mm});
            skArc(sketch, "E17.1.37.0", {"start": v(558.65, 74.46) * mm, "mid": v(557.88, 76.24) * mm, "end": v(557, 77.97) * mm});
            skArc(sketch, "E17.5.37.0", {"start": v(551.93, 74.44) * mm, "mid": v(552.7, 76.23) * mm, "end": v(553.6, 77.97) * mm});
            skPoint(sketch, "E17.9.37.0", {"position": v(559.06, 78.33) * mm});
            skPoint(sketch, "E17.10.37.0", {"position": v(551.49, 73.25) * mm});
            skPoint(sketch, "E17.11.37.0", {"position": v(559.1, 73.25) * mm});
            skPoint(sketch, "E17.12.37.0", {"position": v(549.75, 68.17) * mm});
            skLineSegment(sketch, "E17.13.37.0", {"start": v(554.28, 78.38) * mm, "end": v(556.3, 78.38) * mm});
            skPoint(sketch, "E17.16.37.0", {"position": v(556.77, 78.38) * mm});
            skLineSegment(sketch, "E17.17.37.0", {"start": v(559.1, 72.1) * mm, "end": v(559.1, 68.17) * mm});
            skLineSegment(sketch, "E17.20.37.0", {"start": v(551.47, 68.17) * mm, "end": v(566.71, 68.17) * mm});
            skPoint(sketch, "E17.23.37.0", {"position": v(551.5, 78.33) * mm});
            skLineSegment(sketch, "E17.24.37.0", {"start": v(551.48, 72.11) * mm, "end": v(551.47, 68.17) * mm});
            skArc(sketch, "E17.27.37.0", {"start": v(559.1, 72.1) * mm, "mid": v(559, 73.3) * mm, "end": v(558.65, 74.46) * mm});
            skArc(sketch, "E17.31.37.0", {"start": v(551.93, 74.44) * mm, "mid": v(551.6, 73.3) * mm, "end": v(551.48, 72.11) * mm});
            skLineSegment(sketch, "E17.35.37.0", {"start": v(551.47, 68.17) * mm, "end": v(559.1, 68.17) * mm});
            skArc(sketch, "E17.38.37.0", {"start": v(557, 77.97) * mm, "mid": v(556.71, 78.27) * mm, "end": v(556.3, 78.38) * mm});
            skArc(sketch, "E17.42.37.0", {"start": v(554.28, 78.38) * mm, "mid": v(553.88, 78.27) * mm, "end": v(553.6, 77.97) * mm});
            skPoint(sketch, "E17.0.38.0", {"position": v(569.06, 78.38) * mm});
            skArc(sketch, "E17.1.38.0", {"start": v(573.9, 74.46) * mm, "mid": v(573.12, 76.24) * mm, "end": v(572.24, 77.97) * mm});
            skArc(sketch, "E17.5.38.0", {"start": v(567.17, 74.44) * mm, "mid": v(567.95, 76.23) * mm, "end": v(568.83, 77.97) * mm});
            skPoint(sketch, "E17.9.38.0", {"position": v(574.3, 78.33) * mm});
            skPoint(sketch, "E17.10.38.0", {"position": v(566.73, 73.25) * mm});
            skPoint(sketch, "E17.11.38.0", {"position": v(574.35, 73.25) * mm});
            skPoint(sketch, "E17.12.38.0", {"position": v(565, 68.17) * mm});
            skLineSegment(sketch, "E17.13.38.0", {"start": v(569.52, 78.38) * mm, "end": v(571.55, 78.38) * mm});
            skPoint(sketch, "E17.16.38.0", {"position": v(572.01, 78.38) * mm});
            skLineSegment(sketch, "E17.17.38.0", {"start": v(574.34, 72.1) * mm, "end": v(574.33, 68.17) * mm});
            skLineSegment(sketch, "E17.20.38.0", {"start": v(566.71, 68.17) * mm, "end": v(581.95, 68.17) * mm});
            skPoint(sketch, "E17.23.38.0", {"position": v(566.74, 78.33) * mm});
            skLineSegment(sketch, "E17.24.38.0", {"start": v(566.72, 72.11) * mm, "end": v(566.71, 68.17) * mm});
            skArc(sketch, "E17.27.38.0", {"start": v(574.34, 72.1) * mm, "mid": v(574.23, 73.3) * mm, "end": v(573.9, 74.46) * mm});
            skArc(sketch, "E17.31.38.0", {"start": v(567.17, 74.44) * mm, "mid": v(566.84, 73.3) * mm, "end": v(566.72, 72.11) * mm});
            skLineSegment(sketch, "E17.35.38.0", {"start": v(566.71, 68.17) * mm, "end": v(574.33, 68.17) * mm});
            skArc(sketch, "E17.38.38.0", {"start": v(572.24, 77.97) * mm, "mid": v(571.95, 78.27) * mm, "end": v(571.55, 78.38) * mm});
            skArc(sketch, "E17.42.38.0", {"start": v(569.52, 78.38) * mm, "mid": v(569.12, 78.27) * mm, "end": v(568.83, 77.97) * mm});
            skPoint(sketch, "E17.0.39.0", {"position": v(584.3, 78.38) * mm});
            skArc(sketch, "E17.1.39.0", {"start": v(589.13, 74.46) * mm, "mid": v(588.36, 76.24) * mm, "end": v(587.48, 77.97) * mm});
            skArc(sketch, "E17.5.39.0", {"start": v(582.41, 74.44) * mm, "mid": v(583.19, 76.23) * mm, "end": v(584.07, 77.97) * mm});
            skPoint(sketch, "E17.9.39.0", {"position": v(589.54, 78.33) * mm});
            skPoint(sketch, "E17.10.39.0", {"position": v(581.97, 73.25) * mm});
            skPoint(sketch, "E17.11.39.0", {"position": v(589.59, 73.25) * mm});
            skPoint(sketch, "E17.12.39.0", {"position": v(580.23, 68.17) * mm});
            skLineSegment(sketch, "E17.13.39.0", {"start": v(584.76, 78.38) * mm, "end": v(586.79, 78.38) * mm});
            skPoint(sketch, "E17.16.39.0", {"position": v(587.25, 78.38) * mm});
            skLineSegment(sketch, "E17.17.39.0", {"start": v(589.58, 72.1) * mm, "end": v(589.57, 68.17) * mm});
            skLineSegment(sketch, "E17.20.39.0", {"start": v(581.95, 68.17) * mm, "end": v(597.2, 68.17) * mm});
            skPoint(sketch, "E17.23.39.0", {"position": v(581.98, 78.33) * mm});
            skLineSegment(sketch, "E17.24.39.0", {"start": v(581.96, 72.11) * mm, "end": v(581.95, 68.17) * mm});
            skArc(sketch, "E17.27.39.0", {"start": v(589.58, 72.1) * mm, "mid": v(589.47, 73.3) * mm, "end": v(589.13, 74.46) * mm});
            skArc(sketch, "E17.31.39.0", {"start": v(582.41, 74.44) * mm, "mid": v(582.08, 73.3) * mm, "end": v(581.96, 72.11) * mm});
            skLineSegment(sketch, "E17.35.39.0", {"start": v(581.95, 68.17) * mm, "end": v(589.57, 68.17) * mm});
            skArc(sketch, "E17.38.39.0", {"start": v(587.48, 77.97) * mm, "mid": v(587.2, 78.27) * mm, "end": v(586.79, 78.38) * mm});
            skArc(sketch, "E17.42.39.0", {"start": v(584.76, 78.38) * mm, "mid": v(584.36, 78.27) * mm, "end": v(584.07, 77.97) * mm});
            skPoint(sketch, "E17.0.40.0", {"position": v(599.54, 78.38) * mm});
            skArc(sketch, "E17.1.40.0", {"start": v(604.37, 74.46) * mm, "mid": v(603.6, 76.24) * mm, "end": v(602.72, 77.97) * mm});
            skArc(sketch, "E17.5.40.0", {"start": v(597.65, 74.44) * mm, "mid": v(598.43, 76.23) * mm, "end": v(599.31, 77.97) * mm});
            skPoint(sketch, "E17.9.40.0", {"position": v(604.78, 78.33) * mm});
            skPoint(sketch, "E17.10.40.0", {"position": v(597.2, 73.25) * mm});
            skPoint(sketch, "E17.11.40.0", {"position": v(604.83, 73.25) * mm});
            skPoint(sketch, "E17.12.40.0", {"position": v(595.47, 68.17) * mm});
            skLineSegment(sketch, "E17.13.40.0", {"start": v(600, 78.38) * mm, "end": v(602.03, 78.38) * mm});
            skPoint(sketch, "E17.16.40.0", {"position": v(602.5, 78.38) * mm});
            skLineSegment(sketch, "E17.17.40.0", {"start": v(604.82, 72.1) * mm, "end": v(604.81, 68.17) * mm});
            skLineSegment(sketch, "E17.20.40.0", {"start": v(597.2, 68.17) * mm, "end": v(612.43, 68.17) * mm});
            skPoint(sketch, "E17.23.40.0", {"position": v(597.22, 78.33) * mm});
            skLineSegment(sketch, "E17.24.40.0", {"start": v(597.2, 72.11) * mm, "end": v(597.2, 68.17) * mm});
            skArc(sketch, "E17.27.40.0", {"start": v(604.82, 72.1) * mm, "mid": v(604.71, 73.3) * mm, "end": v(604.37, 74.46) * mm});
            skArc(sketch, "E17.31.40.0", {"start": v(597.65, 74.44) * mm, "mid": v(597.32, 73.3) * mm, "end": v(597.2, 72.11) * mm});
            skLineSegment(sketch, "E17.35.40.0", {"start": v(597.2, 68.17) * mm, "end": v(604.81, 68.17) * mm});
            skArc(sketch, "E17.38.40.0", {"start": v(602.72, 77.97) * mm, "mid": v(602.43, 78.27) * mm, "end": v(602.03, 78.38) * mm});
            skArc(sketch, "E17.42.40.0", {"start": v(600, 78.38) * mm, "mid": v(599.6, 78.27) * mm, "end": v(599.31, 77.97) * mm});
            skPoint(sketch, "E17.0.41.0", {"position": v(614.78, 78.38) * mm});
            skArc(sketch, "E17.1.41.0", {"start": v(619.61, 74.46) * mm, "mid": v(618.84, 76.24) * mm, "end": v(617.96, 77.97) * mm});
            skArc(sketch, "E17.5.41.0", {"start": v(612.9, 74.44) * mm, "mid": v(613.67, 76.23) * mm, "end": v(614.55, 77.97) * mm});
            skPoint(sketch, "E17.9.41.0", {"position": v(620.02, 78.33) * mm});
            skPoint(sketch, "E17.10.41.0", {"position": v(612.45, 73.25) * mm});
            skPoint(sketch, "E17.11.41.0", {"position": v(620.07, 73.25) * mm});
            skPoint(sketch, "E17.12.41.0", {"position": v(610.71, 68.17) * mm});
            skLineSegment(sketch, "E17.13.41.0", {"start": v(615.24, 78.38) * mm, "end": v(617.27, 78.38) * mm});
            skPoint(sketch, "E17.16.41.0", {"position": v(617.73, 78.38) * mm});
            skLineSegment(sketch, "E17.17.41.0", {"start": v(620.06, 72.1) * mm, "end": v(620.05, 68.17) * mm});
            skLineSegment(sketch, "E17.20.41.0", {"start": v(612.43, 68.17) * mm, "end": v(627.67, 68.17) * mm});
            skPoint(sketch, "E17.23.41.0", {"position": v(612.46, 78.33) * mm});
            skLineSegment(sketch, "E17.24.41.0", {"start": v(612.44, 72.11) * mm, "end": v(612.43, 68.17) * mm});
            skArc(sketch, "E17.27.41.0", {"start": v(620.06, 72.1) * mm, "mid": v(619.95, 73.3) * mm, "end": v(619.61, 74.46) * mm});
            skArc(sketch, "E17.31.41.0", {"start": v(612.9, 74.44) * mm, "mid": v(612.56, 73.3) * mm, "end": v(612.44, 72.11) * mm});
            skLineSegment(sketch, "E17.35.41.0", {"start": v(612.43, 68.17) * mm, "end": v(620.05, 68.17) * mm});
            skArc(sketch, "E17.38.41.0", {"start": v(617.96, 77.97) * mm, "mid": v(617.67, 78.27) * mm, "end": v(617.27, 78.38) * mm});
            skArc(sketch, "E17.42.41.0", {"start": v(615.24, 78.38) * mm, "mid": v(614.84, 78.27) * mm, "end": v(614.55, 77.97) * mm});
            skPoint(sketch, "E17.0.42.0", {"position": v(630.02, 78.38) * mm});
            skArc(sketch, "E17.1.42.0", {"start": v(634.85, 74.46) * mm, "mid": v(634.08, 76.24) * mm, "end": v(633.2, 77.97) * mm});
            skArc(sketch, "E17.5.42.0", {"start": v(628.13, 74.44) * mm, "mid": v(628.9, 76.23) * mm, "end": v(629.8, 77.97) * mm});
            skPoint(sketch, "E17.9.42.0", {"position": v(635.26, 78.33) * mm});
            skPoint(sketch, "E17.10.42.0", {"position": v(627.69, 73.25) * mm});
            skPoint(sketch, "E17.11.42.0", {"position": v(635.3, 73.25) * mm});
            skPoint(sketch, "E17.12.42.0", {"position": v(625.95, 68.17) * mm});
            skLineSegment(sketch, "E17.13.42.0", {"start": v(630.48, 78.38) * mm, "end": v(632.5, 78.38) * mm});
            skPoint(sketch, "E17.16.42.0", {"position": v(632.97, 78.38) * mm});
            skLineSegment(sketch, "E17.17.42.0", {"start": v(635.3, 72.1) * mm, "end": v(635.3, 68.17) * mm});
            skLineSegment(sketch, "E17.20.42.0", {"start": v(627.67, 68.17) * mm, "end": v(642.91, 68.17) * mm});
            skPoint(sketch, "E17.23.42.0", {"position": v(627.7, 78.33) * mm});
            skLineSegment(sketch, "E17.24.42.0", {"start": v(627.68, 72.11) * mm, "end": v(627.67, 68.17) * mm});
            skArc(sketch, "E17.27.42.0", {"start": v(635.3, 72.1) * mm, "mid": v(635.2, 73.3) * mm, "end": v(634.85, 74.46) * mm});
            skArc(sketch, "E17.31.42.0", {"start": v(628.13, 74.44) * mm, "mid": v(627.8, 73.3) * mm, "end": v(627.68, 72.11) * mm});
            skLineSegment(sketch, "E17.35.42.0", {"start": v(627.67, 68.17) * mm, "end": v(635.3, 68.17) * mm});
            skArc(sketch, "E17.38.42.0", {"start": v(633.2, 77.97) * mm, "mid": v(632.91, 78.27) * mm, "end": v(632.5, 78.38) * mm});
            skArc(sketch, "E17.42.42.0", {"start": v(630.48, 78.38) * mm, "mid": v(630.08, 78.27) * mm, "end": v(629.8, 77.97) * mm});
            skPoint(sketch, "E17.0.43.0", {"position": v(645.26, 78.38) * mm});
            skArc(sketch, "E17.1.43.0", {"start": v(650.1, 74.46) * mm, "mid": v(649.32, 76.24) * mm, "end": v(648.44, 77.97) * mm});
            skArc(sketch, "E17.5.43.0", {"start": v(643.37, 74.44) * mm, "mid": v(644.15, 76.23) * mm, "end": v(645.03, 77.97) * mm});
            skPoint(sketch, "E17.9.43.0", {"position": v(650.5, 78.33) * mm});
            skPoint(sketch, "E17.10.43.0", {"position": v(642.93, 73.25) * mm});
            skPoint(sketch, "E17.11.43.0", {"position": v(650.55, 73.25) * mm});
            skPoint(sketch, "E17.12.43.0", {"position": v(641.2, 68.17) * mm});
            skLineSegment(sketch, "E17.13.43.0", {"start": v(645.72, 78.38) * mm, "end": v(647.75, 78.38) * mm});
            skPoint(sketch, "E17.16.43.0", {"position": v(648.21, 78.38) * mm});
            skLineSegment(sketch, "E17.17.43.0", {"start": v(650.54, 72.1) * mm, "end": v(650.53, 68.17) * mm});
            skLineSegment(sketch, "E17.20.43.0", {"start": v(642.91, 68.17) * mm, "end": v(658.15, 68.17) * mm});
            skPoint(sketch, "E17.23.43.0", {"position": v(642.94, 78.33) * mm});
            skLineSegment(sketch, "E17.24.43.0", {"start": v(642.92, 72.11) * mm, "end": v(642.91, 68.17) * mm});
            skArc(sketch, "E17.27.43.0", {"start": v(650.54, 72.1) * mm, "mid": v(650.43, 73.3) * mm, "end": v(650.1, 74.46) * mm});
            skArc(sketch, "E17.31.43.0", {"start": v(643.37, 74.44) * mm, "mid": v(643.04, 73.3) * mm, "end": v(642.92, 72.11) * mm});
            skLineSegment(sketch, "E17.35.43.0", {"start": v(642.91, 68.17) * mm, "end": v(650.53, 68.17) * mm});
            skArc(sketch, "E17.38.43.0", {"start": v(648.44, 77.97) * mm, "mid": v(648.15, 78.27) * mm, "end": v(647.75, 78.38) * mm});
            skArc(sketch, "E17.42.43.0", {"start": v(645.72, 78.38) * mm, "mid": v(645.32, 78.27) * mm, "end": v(645.03, 77.97) * mm});
            skPoint(sketch, "E17.0.44.0", {"position": v(660.5, 78.38) * mm});
            skArc(sketch, "E17.1.44.0", {"start": v(665.33, 74.46) * mm, "mid": v(664.56, 76.24) * mm, "end": v(663.68, 77.97) * mm});
            skArc(sketch, "E17.5.44.0", {"start": v(658.61, 74.44) * mm, "mid": v(659.39, 76.23) * mm, "end": v(660.27, 77.97) * mm});
            skPoint(sketch, "E17.9.44.0", {"position": v(665.74, 78.33) * mm});
            skPoint(sketch, "E17.10.44.0", {"position": v(658.17, 73.25) * mm});
            skPoint(sketch, "E17.11.44.0", {"position": v(665.79, 73.25) * mm});
            skPoint(sketch, "E17.12.44.0", {"position": v(656.43, 68.17) * mm});
            skLineSegment(sketch, "E17.13.44.0", {"start": v(660.96, 78.38) * mm, "end": v(662.99, 78.38) * mm});
            skPoint(sketch, "E17.16.44.0", {"position": v(663.45, 78.38) * mm});
            skLineSegment(sketch, "E17.17.44.0", {"start": v(665.78, 72.1) * mm, "end": v(665.77, 68.17) * mm});
            skLineSegment(sketch, "E17.20.44.0", {"start": v(658.15, 68.17) * mm, "end": v(673.4, 68.17) * mm});
            skPoint(sketch, "E17.23.44.0", {"position": v(658.18, 78.33) * mm});
            skLineSegment(sketch, "E17.24.44.0", {"start": v(658.16, 72.11) * mm, "end": v(658.15, 68.17) * mm});
            skArc(sketch, "E17.27.44.0", {"start": v(665.78, 72.1) * mm, "mid": v(665.67, 73.3) * mm, "end": v(665.33, 74.46) * mm});
            skArc(sketch, "E17.31.44.0", {"start": v(658.61, 74.44) * mm, "mid": v(658.28, 73.3) * mm, "end": v(658.16, 72.11) * mm});
            skLineSegment(sketch, "E17.35.44.0", {"start": v(658.15, 68.17) * mm, "end": v(665.77, 68.17) * mm});
            skArc(sketch, "E17.38.44.0", {"start": v(663.68, 77.97) * mm, "mid": v(663.4, 78.27) * mm, "end": v(662.99, 78.38) * mm});
            skArc(sketch, "E17.42.44.0", {"start": v(660.96, 78.38) * mm, "mid": v(660.56, 78.27) * mm, "end": v(660.27, 77.97) * mm});
            skPoint(sketch, "E17.0.45.0", {"position": v(675.74, 78.38) * mm});
            skArc(sketch, "E17.1.45.0", {"start": v(680.57, 74.46) * mm, "mid": v(679.8, 76.24) * mm, "end": v(678.92, 77.97) * mm});
            skArc(sketch, "E17.5.45.0", {"start": v(673.85, 74.44) * mm, "mid": v(674.63, 76.23) * mm, "end": v(675.51, 77.97) * mm});
            skPoint(sketch, "E17.9.45.0", {"position": v(680.98, 78.33) * mm});
            skPoint(sketch, "E17.10.45.0", {"position": v(673.4, 73.25) * mm});
            skPoint(sketch, "E17.11.45.0", {"position": v(681.03, 73.25) * mm});
            skPoint(sketch, "E17.12.45.0", {"position": v(671.67, 68.17) * mm});
            skLineSegment(sketch, "E17.13.45.0", {"start": v(676.2, 78.38) * mm, "end": v(678.23, 78.38) * mm});
            skPoint(sketch, "E17.16.45.0", {"position": v(678.7, 78.38) * mm});
            skLineSegment(sketch, "E17.17.45.0", {"start": v(681.02, 72.1) * mm, "end": v(681.01, 68.17) * mm});
            skLineSegment(sketch, "E17.20.45.0", {"start": v(673.4, 68.17) * mm, "end": v(688.63, 68.17) * mm});
            skPoint(sketch, "E17.23.45.0", {"position": v(673.42, 78.33) * mm});
            skLineSegment(sketch, "E17.24.45.0", {"start": v(673.4, 72.11) * mm, "end": v(673.4, 68.17) * mm});
            skArc(sketch, "E17.27.45.0", {"start": v(681.02, 72.1) * mm, "mid": v(680.91, 73.3) * mm, "end": v(680.57, 74.46) * mm});
            skArc(sketch, "E17.31.45.0", {"start": v(673.85, 74.44) * mm, "mid": v(673.52, 73.3) * mm, "end": v(673.4, 72.11) * mm});
            skLineSegment(sketch, "E17.35.45.0", {"start": v(673.4, 68.17) * mm, "end": v(681.01, 68.17) * mm});
            skArc(sketch, "E17.38.45.0", {"start": v(678.92, 77.97) * mm, "mid": v(678.63, 78.27) * mm, "end": v(678.23, 78.38) * mm});
            skArc(sketch, "E17.42.45.0", {"start": v(676.2, 78.38) * mm, "mid": v(675.8, 78.27) * mm, "end": v(675.51, 77.97) * mm});
            skPoint(sketch, "E17.0.46.0", {"position": v(690.98, 78.38) * mm});
            skArc(sketch, "E17.1.46.0", {"start": v(695.81, 74.46) * mm, "mid": v(695.04, 76.24) * mm, "end": v(694.16, 77.97) * mm});
            skArc(sketch, "E17.5.46.0", {"start": v(689.1, 74.44) * mm, "mid": v(689.87, 76.23) * mm, "end": v(690.75, 77.97) * mm});
            skPoint(sketch, "E17.9.46.0", {"position": v(696.22, 78.33) * mm});
            skPoint(sketch, "E17.10.46.0", {"position": v(688.65, 73.25) * mm});
            skPoint(sketch, "E17.11.46.0", {"position": v(696.27, 73.25) * mm});
            skPoint(sketch, "E17.12.46.0", {"position": v(686.91, 68.17) * mm});
            skLineSegment(sketch, "E17.13.46.0", {"start": v(691.44, 78.38) * mm, "end": v(693.47, 78.38) * mm});
            skPoint(sketch, "E17.16.46.0", {"position": v(693.93, 78.38) * mm});
            skLineSegment(sketch, "E17.17.46.0", {"start": v(696.26, 72.1) * mm, "end": v(696.25, 68.17) * mm});
            skLineSegment(sketch, "E17.20.46.0", {"start": v(688.63, 68.17) * mm, "end": v(703.87, 68.17) * mm});
            skPoint(sketch, "E17.23.46.0", {"position": v(688.66, 78.33) * mm});
            skLineSegment(sketch, "E17.24.46.0", {"start": v(688.64, 72.11) * mm, "end": v(688.63, 68.17) * mm});
            skArc(sketch, "E17.27.46.0", {"start": v(696.26, 72.1) * mm, "mid": v(696.15, 73.3) * mm, "end": v(695.81, 74.46) * mm});
            skArc(sketch, "E17.31.46.0", {"start": v(689.1, 74.44) * mm, "mid": v(688.76, 73.3) * mm, "end": v(688.64, 72.11) * mm});
            skLineSegment(sketch, "E17.35.46.0", {"start": v(688.63, 68.17) * mm, "end": v(696.25, 68.17) * mm});
            skArc(sketch, "E17.38.46.0", {"start": v(694.16, 77.97) * mm, "mid": v(693.87, 78.27) * mm, "end": v(693.47, 78.38) * mm});
            skArc(sketch, "E17.42.46.0", {"start": v(691.44, 78.38) * mm, "mid": v(691.04, 78.27) * mm, "end": v(690.75, 77.97) * mm});
            skPoint(sketch, "E17.0.47.0", {"position": v(706.22, 78.38) * mm});
            skArc(sketch, "E17.1.47.0", {"start": v(711.05, 74.46) * mm, "mid": v(710.28, 76.24) * mm, "end": v(709.4, 77.97) * mm});
            skArc(sketch, "E17.5.47.0", {"start": v(704.33, 74.44) * mm, "mid": v(705.1, 76.23) * mm, "end": v(706, 77.97) * mm});
            skPoint(sketch, "E17.9.47.0", {"position": v(711.46, 78.33) * mm});
            skPoint(sketch, "E17.10.47.0", {"position": v(703.89, 73.25) * mm});
            skPoint(sketch, "E17.11.47.0", {"position": v(711.5, 73.25) * mm});
            skPoint(sketch, "E17.12.47.0", {"position": v(702.15, 68.17) * mm});
            skLineSegment(sketch, "E17.13.47.0", {"start": v(706.68, 78.38) * mm, "end": v(708.7, 78.38) * mm});
            skPoint(sketch, "E17.16.47.0", {"position": v(709.17, 78.38) * mm});
            skLineSegment(sketch, "E17.17.47.0", {"start": v(711.5, 72.1) * mm, "end": v(711.5, 68.17) * mm});
            skLineSegment(sketch, "E17.20.47.0", {"start": v(711.5, 68.17) * mm, "end": v(719.11, 68.17) * mm});
            skPoint(sketch, "E17.23.47.0", {"position": v(703.9, 78.33) * mm});
            skLineSegment(sketch, "E17.24.47.0", {"start": v(703.88, 72.11) * mm, "end": v(703.87, 68.17) * mm});
            skArc(sketch, "E17.27.47.0", {"start": v(711.5, 72.1) * mm, "mid": v(711.4, 73.3) * mm, "end": v(711.05, 74.46) * mm});
            skArc(sketch, "E17.31.47.0", {"start": v(704.33, 74.44) * mm, "mid": v(704, 73.3) * mm, "end": v(703.88, 72.11) * mm});
            skLineSegment(sketch, "E17.35.47.0", {"start": v(703.87, 68.17) * mm, "end": v(711.5, 68.17) * mm});
            skArc(sketch, "E17.38.47.0", {"start": v(709.4, 77.97) * mm, "mid": v(709.11, 78.27) * mm, "end": v(708.7, 78.38) * mm});
            skArc(sketch, "E17.42.47.0", {"start": v(706.68, 78.38) * mm, "mid": v(706.28, 78.27) * mm, "end": v(706, 77.97) * mm});
            skPoint(sketch, "E17.0.48.0", {"position": v(721.46, 78.38) * mm});
            skArc(sketch, "E17.1.48.0", {"start": v(726.3, 74.46) * mm, "mid": v(725.52, 76.24) * mm, "end": v(724.64, 77.97) * mm});
            skArc(sketch, "E17.5.48.0", {"start": v(719.57, 74.44) * mm, "mid": v(720.35, 76.23) * mm, "end": v(721.23, 77.97) * mm});
            skPoint(sketch, "E17.9.48.0", {"position": v(726.7, 78.33) * mm});
            skPoint(sketch, "E17.10.48.0", {"position": v(719.13, 73.25) * mm});
            skPoint(sketch, "E17.11.48.0", {"position": v(726.75, 73.25) * mm});
            skPoint(sketch, "E17.12.48.0", {"position": v(717.4, 68.17) * mm});
            skLineSegment(sketch, "E17.13.48.0", {"start": v(721.92, 78.38) * mm, "end": v(723.95, 78.38) * mm});
            skPoint(sketch, "E17.16.48.0", {"position": v(724.41, 78.38) * mm});
            skLineSegment(sketch, "E17.17.48.0", {"start": v(726.74, 72.1) * mm, "end": v(726.73, 68.17) * mm});
            skLineSegment(sketch, "E17.20.48.0", {"start": v(726.73, 68.17) * mm, "end": v(734.35, 68.17) * mm});
            skPoint(sketch, "E17.23.48.0", {"position": v(719.14, 78.33) * mm});
            skLineSegment(sketch, "E17.24.48.0", {"start": v(719.12, 72.11) * mm, "end": v(719.11, 68.17) * mm});
            skArc(sketch, "E17.27.48.0", {"start": v(726.74, 72.1) * mm, "mid": v(726.63, 73.3) * mm, "end": v(726.3, 74.46) * mm});
            skArc(sketch, "E17.31.48.0", {"start": v(719.57, 74.44) * mm, "mid": v(719.24, 73.3) * mm, "end": v(719.12, 72.11) * mm});
            skArc(sketch, "E17.38.48.0", {"start": v(724.64, 77.97) * mm, "mid": v(724.35, 78.27) * mm, "end": v(723.95, 78.38) * mm});
            skArc(sketch, "E17.42.48.0", {"start": v(721.92, 78.38) * mm, "mid": v(721.52, 78.27) * mm, "end": v(721.23, 77.97) * mm});
            skPoint(sketch, "E17.0.49.0", {"position": v(736.7, 78.38) * mm});
            skArc(sketch, "E17.1.49.0", {"start": v(741.53, 74.46) * mm, "mid": v(740.76, 76.24) * mm, "end": v(739.88, 77.97) * mm});
            skArc(sketch, "E17.5.49.0", {"start": v(734.81, 74.44) * mm, "mid": v(735.59, 76.23) * mm, "end": v(736.47, 77.97) * mm});
            skPoint(sketch, "E17.9.49.0", {"position": v(741.94, 78.33) * mm});
            skPoint(sketch, "E17.10.49.0", {"position": v(734.37, 73.25) * mm});
            skPoint(sketch, "E17.11.49.0", {"position": v(741.99, 73.25) * mm});
            skPoint(sketch, "E17.12.49.0", {"position": v(732.63, 68.17) * mm});
            skLineSegment(sketch, "E17.13.49.0", {"start": v(737.16, 78.38) * mm, "end": v(739.19, 78.38) * mm});
            skPoint(sketch, "E17.16.49.0", {"position": v(739.65, 78.38) * mm});
            skLineSegment(sketch, "E17.17.49.0", {"start": v(741.98, 72.1) * mm, "end": v(741.97, 68.17) * mm});
            skPoint(sketch, "E17.23.49.0", {"position": v(734.38, 78.33) * mm});
            skLineSegment(sketch, "E17.24.49.0", {"start": v(734.36, 72.11) * mm, "end": v(734.35, 68.17) * mm});
            skArc(sketch, "E17.27.49.0", {"start": v(741.98, 72.1) * mm, "mid": v(741.87, 73.3) * mm, "end": v(741.53, 74.46) * mm});
            skArc(sketch, "E17.31.49.0", {"start": v(734.81, 74.44) * mm, "mid": v(734.48, 73.3) * mm, "end": v(734.36, 72.11) * mm});
            skArc(sketch, "E17.38.49.0", {"start": v(739.88, 77.97) * mm, "mid": v(739.6, 78.27) * mm, "end": v(739.19, 78.38) * mm});
            skArc(sketch, "E17.42.49.0", {"start": v(737.16, 78.38) * mm, "mid": v(736.76, 78.27) * mm, "end": v(736.47, 77.97) * mm});
            skLineSegment(sketch, "E18", {"start": v(-12.4, 68.17) * mm, "end": v(-20.03, 68.17) * mm});
            skLineSegment(sketch, "E19", {"start": v(-20.03, 68.17) * mm, "end": v(-20.03, 49.12) * mm});
            skLineSegment(sketch, "E20", {"start": v(-20.03, 49.12) * mm, "end": v(741.97, 49.12) * mm});
            skLineSegment(sketch, "E21", {"start": v(741.97, 49.12) * mm, "end": v(741.97, 68.17) * mm});
            skLineSegment(sketch, "E22", {"start": v(691.17, 49.12) * mm, "end": v(691.17, 61.82) * mm});
            skLineSegment(sketch, "E23", {"start": v(691.17, 61.82) * mm, "end": v(741.97, 61.82) * mm});
            skLineSegment(sketch, "E24", {"start": v(741.97, 61.82) * mm, "end": v(741.97, 49.12) * mm});
            skLineSegment(sketch, "E25", {"start": v(741.97, 49.12) * mm, "end": v(691.17, 49.12) * mm});
            skSolve(sketch);
        }
        {
            var Q0;
            Q0 = qSketchRegion(id + "F0", true);
            extrude(context, id + "F1", {"entities" : qUnion([Q0]), "depth" : 127 * mm});
        }
        {
            var Q0;
            Q0=makeQuery(id+"F1.opExtrude","CAP_FACE",FACE,{"disambiguationData":[OSD([sQuery(id+"F0.wireOp",EDGE,"E2.MirrorCS"),sQuery(id+"F0.wireOp",EDGE,"E3.MirrorCS"),sQuery(id+"F0.wireOp",EDGE,"E6.filletArc"),sQuery(id+"F0.wireOp",EDGE,"E7.filletArc"),sQuery(id+"F0.wireOp",EDGE,"E8.filletArc"),sQuery(id+"F0.wireOp",EDGE,"E9.filletArc"),sQuery(id+"F0.wireOp",EDGE,"E10"),sQuery(id+"F0.wireOp",EDGE,"E11"),sQuery(id+"F0.wireOp",EDGE,"E12"),sQuery(id+"F0.wireOp",EDGE,"E15"),sQuery(id+"F0.wireOp",EDGE,"E16.1.0.1"),sQuery(id+"F0.wireOp",EDGE,"E16.1.0.2"),sQuery(id+"F0.wireOp",EDGE,"E16.1.0.7"),sQuery(id+"F0.wireOp",EDGE,"E16.1.0.9"),sQuery(id+"F0.wireOp",EDGE,"E16.1.0.10"),sQuery(id+"F0.wireOp",EDGE,"E16.1.0.12"),sQuery(id+"F0.wireOp",EDGE,"E16.1.0.13"),sQuery(id+"F0.wireOp",EDGE,"E16.1.0.14"),sQuery(id+"F0.wireOp",EDGE,"E16.1.0.16"),sQuery(id+"F0.wireOp",EDGE,"E16.1.0.17"),sQuery(id+"F0.wireOp",EDGE,"E16.2.0.1"),sQuery(id+"F0.wireOp",EDGE,"E16.2.0.2"),sQuery(id+"F0.wireOp",EDGE,"E16.2.0.7"),sQuery(id+"F0.wireOp",EDGE,"E16.2.0.9"),sQuery(id+"F0.wireOp",EDGE,"E16.2.0.10"),sQuery(id+"F0.wireOp",EDGE,"E16.2.0.12"),sQuery(id+"F0.wireOp",EDGE,"E16.2.0.13"),sQuery(id+"F0.wireOp",EDGE,"E16.2.0.14"),sQuery(id+"F0.wireOp",EDGE,"E16.2.0.16"),sQuery(id+"F0.wireOp",EDGE,"E16.2.0.17"),sQuery(id+"F0.wireOp",EDGE,"E17.1.3.0"),sQuery(id+"F0.wireOp",EDGE,"E17.5.3.0"),sQuery(id+"F0.wireOp",EDGE,"E17.13.3.0"),sQuery(id+"F0.wireOp",EDGE,"E17.17.3.0"),sQuery(id+"F0.wireOp",EDGE,"E17.20.3.0"),sQuery(id+"F0.wireOp",EDGE,"E17.24.3.0"),sQuery(id+"F0.wireOp",EDGE,"E17.27.3.0"),sQuery(id+"F0.wireOp",EDGE,"E17.31.3.0"),sQuery(id+"F0.wireOp",EDGE,"E17.38.3.0"),sQuery(id+"F0.wireOp",EDGE,"E17.42.3.0"),sQuery(id+"F0.wireOp",EDGE,"E17.1.4.0"),sQuery(id+"F0.wireOp",EDGE,"E17.5.4.0"),sQuery(id+"F0.wireOp",EDGE,"E17.13.4.0"),sQuery(id+"F0.wireOp",EDGE,"E17.17.4.0"),sQuery(id+"F0.wireOp",EDGE,"E17.20.4.0"),sQuery(id+"F0.wireOp",EDGE,"E17.24.4.0"),sQuery(id+"F0.wireOp",EDGE,"E17.27.4.0"),sQuery(id+"F0.wireOp",EDGE,"E17.31.4.0"),sQuery(id+"F0.wireOp",EDGE,"E17.38.4.0"),sQuery(id+"F0.wireOp",EDGE,"E17.42.4.0"),sQuery(id+"F0.wireOp",EDGE,"E17.1.5.0"),sQuery(id+"F0.wireOp",EDGE,"E17.5.5.0"),sQuery(id+"F0.wireOp",EDGE,"E17.13.5.0"),sQuery(id+"F0.wireOp",EDGE,"E17.17.5.0"),sQuery(id+"F0.wireOp",EDGE,"E17.20.5.0"),sQuery(id+"F0.wireOp",EDGE,"E17.24.5.0"),sQuery(id+"F0.wireOp",EDGE,"E17.27.5.0"),sQuery(id+"F0.wireOp",EDGE,"E17.31.5.0"),sQuery(id+"F0.wireOp",EDGE,"E17.38.5.0"),sQuery(id+"F0.wireOp",EDGE,"E17.42.5.0"),sQuery(id+"F0.wireOp",EDGE,"E17.1.6.0"),sQuery(id+"F0.wireOp",EDGE,"E17.5.6.0"),sQuery(id+"F0.wireOp",EDGE,"E17.13.6.0"),sQuery(id+"F0.wireOp",EDGE,"E17.17.6.0"),sQuery(id+"F0.wireOp",EDGE,"E17.20.6.0"),sQuery(id+"F0.wireOp",EDGE,"E17.24.6.0"),sQuery(id+"F0.wireOp",EDGE,"E17.27.6.0"),sQuery(id+"F0.wireOp",EDGE,"E17.31.6.0"),sQuery(id+"F0.wireOp",EDGE,"E17.38.6.0"),sQuery(id+"F0.wireOp",EDGE,"E17.42.6.0"),sQuery(id+"F0.wireOp",EDGE,"E17.1.7.0"),sQuery(id+"F0.wireOp",EDGE,"E17.5.7.0"),sQuery(id+"F0.wireOp",EDGE,"E17.13.7.0"),sQuery(id+"F0.wireOp",EDGE,"E17.17.7.0"),sQuery(id+"F0.wireOp",EDGE,"E17.20.7.0"),sQuery(id+"F0.wireOp",EDGE,"E17.24.7.0"),sQuery(id+"F0.wireOp",EDGE,"E17.27.7.0"),sQuery(id+"F0.wireOp",EDGE,"E17.31.7.0"),sQuery(id+"F0.wireOp",EDGE,"E17.38.7.0"),sQuery(id+"F0.wireOp",EDGE,"E17.42.7.0"),sQuery(id+"F0.wireOp",EDGE,"E17.1.8.0"),sQuery(id+"F0.wireOp",EDGE,"E17.5.8.0"),sQuery(id+"F0.wireOp",EDGE,"E17.13.8.0"),sQuery(id+"F0.wireOp",EDGE,"E17.17.8.0"),sQuery(id+"F0.wireOp",EDGE,"E17.20.8.0"),sQuery(id+"F0.wireOp",EDGE,"E17.24.8.0"),sQuery(id+"F0.wireOp",EDGE,"E17.27.8.0"),sQuery(id+"F0.wireOp",EDGE,"E17.31.8.0"),sQuery(id+"F0.wireOp",EDGE,"E17.38.8.0"),sQuery(id+"F0.wireOp",EDGE,"E17.42.8.0"),sQuery(id+"F0.wireOp",EDGE,"E17.1.9.0"),sQuery(id+"F0.wireOp",EDGE,"E17.5.9.0"),sQuery(id+"F0.wireOp",EDGE,"E17.13.9.0"),sQuery(id+"F0.wireOp",EDGE,"E17.17.9.0"),sQuery(id+"F0.wireOp",EDGE,"E17.20.9.0"),sQuery(id+"F0.wireOp",EDGE,"E17.24.9.0"),sQuery(id+"F0.wireOp",EDGE,"E17.27.9.0"),sQuery(id+"F0.wireOp",EDGE,"E17.31.9.0"),sQuery(id+"F0.wireOp",EDGE,"E17.38.9.0"),sQuery(id+"F0.wireOp",EDGE,"E17.42.9.0"),sQuery(id+"F0.wireOp",EDGE,"E17.1.10.0"),sQuery(id+"F0.wireOp",EDGE,"E17.5.10.0"),sQuery(id+"F0.wireOp",EDGE,"E17.13.10.0"),sQuery(id+"F0.wireOp",EDGE,"E17.17.10.0"),sQuery(id+"F0.wireOp",EDGE,"E17.20.10.0"),sQuery(id+"F0.wireOp",EDGE,"E17.24.10.0"),sQuery(id+"F0.wireOp",EDGE,"E17.27.10.0"),sQuery(id+"F0.wireOp",EDGE,"E17.31.10.0"),sQuery(id+"F0.wireOp",EDGE,"E17.38.10.0"),sQuery(id+"F0.wireOp",EDGE,"E17.42.10.0"),sQuery(id+"F0.wireOp",EDGE,"E17.1.11.0"),sQuery(id+"F0.wireOp",EDGE,"E17.5.11.0"),sQuery(id+"F0.wireOp",EDGE,"E17.13.11.0"),sQuery(id+"F0.wireOp",EDGE,"E17.17.11.0"),sQuery(id+"F0.wireOp",EDGE,"E17.20.11.0"),sQuery(id+"F0.wireOp",EDGE,"E17.24.11.0"),sQuery(id+"F0.wireOp",EDGE,"E17.27.11.0"),sQuery(id+"F0.wireOp",EDGE,"E17.31.11.0"),sQuery(id+"F0.wireOp",EDGE,"E17.38.11.0"),sQuery(id+"F0.wireOp",EDGE,"E17.42.11.0"),sQuery(id+"F0.wireOp",EDGE,"E17.1.12.0"),sQuery(id+"F0.wireOp",EDGE,"E17.5.12.0"),sQuery(id+"F0.wireOp",EDGE,"E17.13.12.0"),sQuery(id+"F0.wireOp",EDGE,"E17.17.12.0"),sQuery(id+"F0.wireOp",EDGE,"E17.20.12.0"),sQuery(id+"F0.wireOp",EDGE,"E17.24.12.0"),sQuery(id+"F0.wireOp",EDGE,"E17.27.12.0"),sQuery(id+"F0.wireOp",EDGE,"E17.31.12.0"),sQuery(id+"F0.wireOp",EDGE,"E17.38.12.0"),sQuery(id+"F0.wireOp",EDGE,"E17.42.12.0"),sQuery(id+"F0.wireOp",EDGE,"E17.1.13.0"),sQuery(id+"F0.wireOp",EDGE,"E17.5.13.0"),sQuery(id+"F0.wireOp",EDGE,"E17.13.13.0"),sQuery(id+"F0.wireOp",EDGE,"E17.17.13.0"),sQuery(id+"F0.wireOp",EDGE,"E17.20.13.0"),sQuery(id+"F0.wireOp",EDGE,"E17.24.13.0"),sQuery(id+"F0.wireOp",EDGE,"E17.27.13.0"),sQuery(id+"F0.wireOp",EDGE,"E17.31.13.0"),sQuery(id+"F0.wireOp",EDGE,"E17.38.13.0"),sQuery(id+"F0.wireOp",EDGE,"E17.42.13.0"),sQuery(id+"F0.wireOp",EDGE,"E17.1.14.0"),sQuery(id+"F0.wireOp",EDGE,"E17.5.14.0"),sQuery(id+"F0.wireOp",EDGE,"E17.13.14.0"),sQuery(id+"F0.wireOp",EDGE,"E17.17.14.0"),sQuery(id+"F0.wireOp",EDGE,"E17.20.14.0"),sQuery(id+"F0.wireOp",EDGE,"E17.24.14.0"),sQuery(id+"F0.wireOp",EDGE,"E17.27.14.0"),sQuery(id+"F0.wireOp",EDGE,"E17.31.14.0"),sQuery(id+"F0.wireOp",EDGE,"E17.38.14.0"),sQuery(id+"F0.wireOp",EDGE,"E17.42.14.0"),sQuery(id+"F0.wireOp",EDGE,"E17.1.15.0"),sQuery(id+"F0.wireOp",EDGE,"E17.5.15.0"),sQuery(id+"F0.wireOp",EDGE,"E17.13.15.0"),sQuery(id+"F0.wireOp",EDGE,"E17.17.15.0"),sQuery(id+"F0.wireOp",EDGE,"E17.20.15.0"),sQuery(id+"F0.wireOp",EDGE,"E17.24.15.0"),sQuery(id+"F0.wireOp",EDGE,"E17.27.15.0"),sQuery(id+"F0.wireOp",EDGE,"E17.31.15.0"),sQuery(id+"F0.wireOp",EDGE,"E17.38.15.0"),sQuery(id+"F0.wireOp",EDGE,"E17.42.15.0"),sQuery(id+"F0.wireOp",EDGE,"E17.1.16.0"),sQuery(id+"F0.wireOp",EDGE,"E17.5.16.0"),sQuery(id+"F0.wireOp",EDGE,"E17.13.16.0"),sQuery(id+"F0.wireOp",EDGE,"E17.17.16.0"),sQuery(id+"F0.wireOp",EDGE,"E17.20.16.0"),sQuery(id+"F0.wireOp",EDGE,"E17.24.16.0"),sQuery(id+"F0.wireOp",EDGE,"E17.27.16.0"),sQuery(id+"F0.wireOp",EDGE,"E17.31.16.0"),sQuery(id+"F0.wireOp",EDGE,"E17.38.16.0"),sQuery(id+"F0.wireOp",EDGE,"E17.42.16.0"),sQuery(id+"F0.wireOp",EDGE,"E17.1.17.0"),sQuery(id+"F0.wireOp",EDGE,"E17.5.17.0"),sQuery(id+"F0.wireOp",EDGE,"E17.13.17.0"),sQuery(id+"F0.wireOp",EDGE,"E17.17.17.0"),sQuery(id+"F0.wireOp",EDGE,"E17.20.17.0"),sQuery(id+"F0.wireOp",EDGE,"E17.24.17.0"),sQuery(id+"F0.wireOp",EDGE,"E17.27.17.0"),sQuery(id+"F0.wireOp",EDGE,"E17.31.17.0"),sQuery(id+"F0.wireOp",EDGE,"E17.38.17.0"),sQuery(id+"F0.wireOp",EDGE,"E17.42.17.0"),sQuery(id+"F0.wireOp",EDGE,"E17.1.18.0"),sQuery(id+"F0.wireOp",EDGE,"E17.5.18.0"),sQuery(id+"F0.wireOp",EDGE,"E17.13.18.0"),sQuery(id+"F0.wireOp",EDGE,"E17.17.18.0"),sQuery(id+"F0.wireOp",EDGE,"E17.20.18.0"),sQuery(id+"F0.wireOp",EDGE,"E17.24.18.0"),sQuery(id+"F0.wireOp",EDGE,"E17.27.18.0"),sQuery(id+"F0.wireOp",EDGE,"E17.31.18.0"),sQuery(id+"F0.wireOp",EDGE,"E17.38.18.0"),sQuery(id+"F0.wireOp",EDGE,"E17.42.18.0"),sQuery(id+"F0.wireOp",EDGE,"E17.1.19.0"),sQuery(id+"F0.wireOp",EDGE,"E17.5.19.0"),sQuery(id+"F0.wireOp",EDGE,"E17.13.19.0"),sQuery(id+"F0.wireOp",EDGE,"E17.17.19.0"),sQuery(id+"F0.wireOp",EDGE,"E17.20.19.0"),sQuery(id+"F0.wireOp",EDGE,"E17.24.19.0"),sQuery(id+"F0.wireOp",EDGE,"E17.27.19.0"),sQuery(id+"F0.wireOp",EDGE,"E17.31.19.0"),sQuery(id+"F0.wireOp",EDGE,"E17.38.19.0"),sQuery(id+"F0.wireOp",EDGE,"E17.42.19.0"),sQuery(id+"F0.wireOp",EDGE,"E17.1.20.0"),sQuery(id+"F0.wireOp",EDGE,"E17.5.20.0"),sQuery(id+"F0.wireOp",EDGE,"E17.13.20.0"),sQuery(id+"F0.wireOp",EDGE,"E17.17.20.0"),sQuery(id+"F0.wireOp",EDGE,"E17.20.20.0"),sQuery(id+"F0.wireOp",EDGE,"E17.24.20.0"),sQuery(id+"F0.wireOp",EDGE,"E17.27.20.0"),sQuery(id+"F0.wireOp",EDGE,"E17.31.20.0"),sQuery(id+"F0.wireOp",EDGE,"E17.38.20.0"),sQuery(id+"F0.wireOp",EDGE,"E17.42.20.0"),sQuery(id+"F0.wireOp",EDGE,"E17.1.21.0"),sQuery(id+"F0.wireOp",EDGE,"E17.5.21.0"),sQuery(id+"F0.wireOp",EDGE,"E17.13.21.0"),sQuery(id+"F0.wireOp",EDGE,"E17.17.21.0"),sQuery(id+"F0.wireOp",EDGE,"E17.20.21.0"),sQuery(id+"F0.wireOp",EDGE,"E17.24.21.0"),sQuery(id+"F0.wireOp",EDGE,"E17.27.21.0"),sQuery(id+"F0.wireOp",EDGE,"E17.31.21.0"),sQuery(id+"F0.wireOp",EDGE,"E17.38.21.0"),sQuery(id+"F0.wireOp",EDGE,"E17.42.21.0"),sQuery(id+"F0.wireOp",EDGE,"E17.1.22.0"),sQuery(id+"F0.wireOp",EDGE,"E17.5.22.0"),sQuery(id+"F0.wireOp",EDGE,"E17.13.22.0"),sQuery(id+"F0.wireOp",EDGE,"E17.17.22.0"),sQuery(id+"F0.wireOp",EDGE,"E17.20.22.0"),sQuery(id+"F0.wireOp",EDGE,"E17.24.22.0"),sQuery(id+"F0.wireOp",EDGE,"E17.27.22.0"),sQuery(id+"F0.wireOp",EDGE,"E17.31.22.0"),sQuery(id+"F0.wireOp",EDGE,"E17.38.22.0"),sQuery(id+"F0.wireOp",EDGE,"E17.42.22.0"),sQuery(id+"F0.wireOp",EDGE,"E17.1.23.0"),sQuery(id+"F0.wireOp",EDGE,"E17.5.23.0"),sQuery(id+"F0.wireOp",EDGE,"E17.13.23.0"),sQuery(id+"F0.wireOp",EDGE,"E17.17.23.0"),sQuery(id+"F0.wireOp",EDGE,"E17.20.23.0"),sQuery(id+"F0.wireOp",EDGE,"E17.24.23.0"),sQuery(id+"F0.wireOp",EDGE,"E17.27.23.0"),sQuery(id+"F0.wireOp",EDGE,"E17.31.23.0"),sQuery(id+"F0.wireOp",EDGE,"E17.38.23.0"),sQuery(id+"F0.wireOp",EDGE,"E17.42.23.0"),sQuery(id+"F0.wireOp",EDGE,"E17.1.24.0"),sQuery(id+"F0.wireOp",EDGE,"E17.5.24.0"),sQuery(id+"F0.wireOp",EDGE,"E17.13.24.0"),sQuery(id+"F0.wireOp",EDGE,"E17.17.24.0"),sQuery(id+"F0.wireOp",EDGE,"E17.20.24.0"),sQuery(id+"F0.wireOp",EDGE,"E17.24.24.0"),sQuery(id+"F0.wireOp",EDGE,"E17.27.24.0"),sQuery(id+"F0.wireOp",EDGE,"E17.31.24.0"),sQuery(id+"F0.wireOp",EDGE,"E17.38.24.0"),sQuery(id+"F0.wireOp",EDGE,"E17.42.24.0"),sQuery(id+"F0.wireOp",EDGE,"E17.1.25.0"),sQuery(id+"F0.wireOp",EDGE,"E17.5.25.0"),sQuery(id+"F0.wireOp",EDGE,"E17.13.25.0"),sQuery(id+"F0.wireOp",EDGE,"E17.17.25.0"),sQuery(id+"F0.wireOp",EDGE,"E17.20.25.0"),sQuery(id+"F0.wireOp",EDGE,"E17.24.25.0"),sQuery(id+"F0.wireOp",EDGE,"E17.27.25.0"),sQuery(id+"F0.wireOp",EDGE,"E17.31.25.0"),sQuery(id+"F0.wireOp",EDGE,"E17.38.25.0"),sQuery(id+"F0.wireOp",EDGE,"E17.42.25.0"),sQuery(id+"F0.wireOp",EDGE,"E17.1.26.0"),sQuery(id+"F0.wireOp",EDGE,"E17.5.26.0"),sQuery(id+"F0.wireOp",EDGE,"E17.13.26.0"),sQuery(id+"F0.wireOp",EDGE,"E17.17.26.0"),sQuery(id+"F0.wireOp",EDGE,"E17.20.26.0"),sQuery(id+"F0.wireOp",EDGE,"E17.24.26.0"),sQuery(id+"F0.wireOp",EDGE,"E17.27.26.0"),sQuery(id+"F0.wireOp",EDGE,"E17.31.26.0"),sQuery(id+"F0.wireOp",EDGE,"E17.38.26.0"),sQuery(id+"F0.wireOp",EDGE,"E17.42.26.0"),sQuery(id+"F0.wireOp",EDGE,"E17.1.27.0"),sQuery(id+"F0.wireOp",EDGE,"E17.5.27.0"),sQuery(id+"F0.wireOp",EDGE,"E17.13.27.0"),sQuery(id+"F0.wireOp",EDGE,"E17.17.27.0"),sQuery(id+"F0.wireOp",EDGE,"E17.20.27.0"),sQuery(id+"F0.wireOp",EDGE,"E17.24.27.0"),sQuery(id+"F0.wireOp",EDGE,"E17.27.27.0"),sQuery(id+"F0.wireOp",EDGE,"E17.31.27.0"),sQuery(id+"F0.wireOp",EDGE,"E17.38.27.0"),sQuery(id+"F0.wireOp",EDGE,"E17.42.27.0"),sQuery(id+"F0.wireOp",EDGE,"E17.1.28.0"),sQuery(id+"F0.wireOp",EDGE,"E17.5.28.0"),sQuery(id+"F0.wireOp",EDGE,"E17.13.28.0"),sQuery(id+"F0.wireOp",EDGE,"E17.17.28.0"),sQuery(id+"F0.wireOp",EDGE,"E17.20.28.0"),sQuery(id+"F0.wireOp",EDGE,"E17.24.28.0"),sQuery(id+"F0.wireOp",EDGE,"E17.27.28.0"),sQuery(id+"F0.wireOp",EDGE,"E17.31.28.0"),sQuery(id+"F0.wireOp",EDGE,"E17.38.28.0"),sQuery(id+"F0.wireOp",EDGE,"E17.42.28.0"),sQuery(id+"F0.wireOp",EDGE,"E17.1.29.0"),sQuery(id+"F0.wireOp",EDGE,"E17.5.29.0"),sQuery(id+"F0.wireOp",EDGE,"E17.13.29.0"),sQuery(id+"F0.wireOp",EDGE,"E17.17.29.0"),sQuery(id+"F0.wireOp",EDGE,"E17.20.29.0"),sQuery(id+"F0.wireOp",EDGE,"E17.24.29.0"),sQuery(id+"F0.wireOp",EDGE,"E17.27.29.0"),sQuery(id+"F0.wireOp",EDGE,"E17.31.29.0"),sQuery(id+"F0.wireOp",EDGE,"E17.38.29.0"),sQuery(id+"F0.wireOp",EDGE,"E17.42.29.0"),sQuery(id+"F0.wireOp",EDGE,"E17.1.30.0"),sQuery(id+"F0.wireOp",EDGE,"E17.5.30.0"),sQuery(id+"F0.wireOp",EDGE,"E17.13.30.0"),sQuery(id+"F0.wireOp",EDGE,"E17.17.30.0"),sQuery(id+"F0.wireOp",EDGE,"E17.20.30.0"),sQuery(id+"F0.wireOp",EDGE,"E17.24.30.0"),sQuery(id+"F0.wireOp",EDGE,"E17.27.30.0"),sQuery(id+"F0.wireOp",EDGE,"E17.31.30.0"),sQuery(id+"F0.wireOp",EDGE,"E17.38.30.0"),sQuery(id+"F0.wireOp",EDGE,"E17.42.30.0"),sQuery(id+"F0.wireOp",EDGE,"E17.1.31.0"),sQuery(id+"F0.wireOp",EDGE,"E17.5.31.0"),sQuery(id+"F0.wireOp",EDGE,"E17.13.31.0"),sQuery(id+"F0.wireOp",EDGE,"E17.17.31.0"),sQuery(id+"F0.wireOp",EDGE,"E17.20.31.0"),sQuery(id+"F0.wireOp",EDGE,"E17.24.31.0"),sQuery(id+"F0.wireOp",EDGE,"E17.27.31.0"),sQuery(id+"F0.wireOp",EDGE,"E17.31.31.0"),sQuery(id+"F0.wireOp",EDGE,"E17.38.31.0"),sQuery(id+"F0.wireOp",EDGE,"E17.42.31.0"),sQuery(id+"F0.wireOp",EDGE,"E17.1.32.0"),sQuery(id+"F0.wireOp",EDGE,"E17.5.32.0"),sQuery(id+"F0.wireOp",EDGE,"E17.13.32.0"),sQuery(id+"F0.wireOp",EDGE,"E17.17.32.0"),sQuery(id+"F0.wireOp",EDGE,"E17.20.32.0"),sQuery(id+"F0.wireOp",EDGE,"E17.24.32.0"),sQuery(id+"F0.wireOp",EDGE,"E17.27.32.0"),sQuery(id+"F0.wireOp",EDGE,"E17.31.32.0"),sQuery(id+"F0.wireOp",EDGE,"E17.38.32.0"),sQuery(id+"F0.wireOp",EDGE,"E17.42.32.0"),sQuery(id+"F0.wireOp",EDGE,"E17.1.33.0"),sQuery(id+"F0.wireOp",EDGE,"E17.5.33.0"),sQuery(id+"F0.wireOp",EDGE,"E17.13.33.0"),sQuery(id+"F0.wireOp",EDGE,"E17.17.33.0"),sQuery(id+"F0.wireOp",EDGE,"E17.20.33.0"),sQuery(id+"F0.wireOp",EDGE,"E17.24.33.0"),sQuery(id+"F0.wireOp",EDGE,"E17.27.33.0"),sQuery(id+"F0.wireOp",EDGE,"E17.31.33.0"),sQuery(id+"F0.wireOp",EDGE,"E17.38.33.0"),sQuery(id+"F0.wireOp",EDGE,"E17.42.33.0"),sQuery(id+"F0.wireOp",EDGE,"E17.1.34.0"),sQuery(id+"F0.wireOp",EDGE,"E17.5.34.0"),sQuery(id+"F0.wireOp",EDGE,"E17.13.34.0"),sQuery(id+"F0.wireOp",EDGE,"E17.17.34.0"),sQuery(id+"F0.wireOp",EDGE,"E17.20.34.0"),sQuery(id+"F0.wireOp",EDGE,"E17.24.34.0"),sQuery(id+"F0.wireOp",EDGE,"E17.27.34.0"),sQuery(id+"F0.wireOp",EDGE,"E17.31.34.0"),sQuery(id+"F0.wireOp",EDGE,"E17.38.34.0"),sQuery(id+"F0.wireOp",EDGE,"E17.42.34.0"),sQuery(id+"F0.wireOp",EDGE,"E17.1.35.0"),sQuery(id+"F0.wireOp",EDGE,"E17.5.35.0"),sQuery(id+"F0.wireOp",EDGE,"E17.13.35.0"),sQuery(id+"F0.wireOp",EDGE,"E17.17.35.0"),sQuery(id+"F0.wireOp",EDGE,"E17.20.35.0"),sQuery(id+"F0.wireOp",EDGE,"E17.24.35.0"),sQuery(id+"F0.wireOp",EDGE,"E17.27.35.0"),sQuery(id+"F0.wireOp",EDGE,"E17.31.35.0"),sQuery(id+"F0.wireOp",EDGE,"E17.38.35.0"),sQuery(id+"F0.wireOp",EDGE,"E17.42.35.0"),sQuery(id+"F0.wireOp",EDGE,"E17.1.36.0"),sQuery(id+"F0.wireOp",EDGE,"E17.5.36.0"),sQuery(id+"F0.wireOp",EDGE,"E17.13.36.0"),sQuery(id+"F0.wireOp",EDGE,"E17.17.36.0"),sQuery(id+"F0.wireOp",EDGE,"E17.20.36.0"),sQuery(id+"F0.wireOp",EDGE,"E17.24.36.0"),sQuery(id+"F0.wireOp",EDGE,"E17.27.36.0"),sQuery(id+"F0.wireOp",EDGE,"E17.31.36.0"),sQuery(id+"F0.wireOp",EDGE,"E17.38.36.0"),sQuery(id+"F0.wireOp",EDGE,"E17.42.36.0"),sQuery(id+"F0.wireOp",EDGE,"E17.1.37.0"),sQuery(id+"F0.wireOp",EDGE,"E17.5.37.0"),sQuery(id+"F0.wireOp",EDGE,"E17.13.37.0"),sQuery(id+"F0.wireOp",EDGE,"E17.17.37.0"),sQuery(id+"F0.wireOp",EDGE,"E17.20.37.0"),sQuery(id+"F0.wireOp",EDGE,"E17.24.37.0"),sQuery(id+"F0.wireOp",EDGE,"E17.27.37.0"),sQuery(id+"F0.wireOp",EDGE,"E17.31.37.0"),sQuery(id+"F0.wireOp",EDGE,"E17.38.37.0"),sQuery(id+"F0.wireOp",EDGE,"E17.42.37.0"),sQuery(id+"F0.wireOp",EDGE,"E17.1.38.0"),sQuery(id+"F0.wireOp",EDGE,"E17.5.38.0"),sQuery(id+"F0.wireOp",EDGE,"E17.13.38.0"),sQuery(id+"F0.wireOp",EDGE,"E17.17.38.0"),sQuery(id+"F0.wireOp",EDGE,"E17.20.38.0"),sQuery(id+"F0.wireOp",EDGE,"E17.24.38.0"),sQuery(id+"F0.wireOp",EDGE,"E17.27.38.0"),sQuery(id+"F0.wireOp",EDGE,"E17.31.38.0"),sQuery(id+"F0.wireOp",EDGE,"E17.38.38.0"),sQuery(id+"F0.wireOp",EDGE,"E17.42.38.0"),sQuery(id+"F0.wireOp",EDGE,"E17.1.39.0"),sQuery(id+"F0.wireOp",EDGE,"E17.5.39.0"),sQuery(id+"F0.wireOp",EDGE,"E17.13.39.0"),sQuery(id+"F0.wireOp",EDGE,"E17.17.39.0"),sQuery(id+"F0.wireOp",EDGE,"E17.20.39.0"),sQuery(id+"F0.wireOp",EDGE,"E17.24.39.0"),sQuery(id+"F0.wireOp",EDGE,"E17.27.39.0"),sQuery(id+"F0.wireOp",EDGE,"E17.31.39.0"),sQuery(id+"F0.wireOp",EDGE,"E17.38.39.0"),sQuery(id+"F0.wireOp",EDGE,"E17.42.39.0"),sQuery(id+"F0.wireOp",EDGE,"E17.1.40.0"),sQuery(id+"F0.wireOp",EDGE,"E17.5.40.0"),sQuery(id+"F0.wireOp",EDGE,"E17.13.40.0"),sQuery(id+"F0.wireOp",EDGE,"E17.17.40.0"),sQuery(id+"F0.wireOp",EDGE,"E17.20.40.0"),sQuery(id+"F0.wireOp",EDGE,"E17.24.40.0"),sQuery(id+"F0.wireOp",EDGE,"E17.27.40.0"),sQuery(id+"F0.wireOp",EDGE,"E17.31.40.0"),sQuery(id+"F0.wireOp",EDGE,"E17.38.40.0"),sQuery(id+"F0.wireOp",EDGE,"E17.42.40.0"),sQuery(id+"F0.wireOp",EDGE,"E17.1.41.0"),sQuery(id+"F0.wireOp",EDGE,"E17.5.41.0"),sQuery(id+"F0.wireOp",EDGE,"E17.13.41.0"),sQuery(id+"F0.wireOp",EDGE,"E17.17.41.0"),sQuery(id+"F0.wireOp",EDGE,"E17.20.41.0"),sQuery(id+"F0.wireOp",EDGE,"E17.24.41.0"),sQuery(id+"F0.wireOp",EDGE,"E17.27.41.0"),sQuery(id+"F0.wireOp",EDGE,"E17.31.41.0"),sQuery(id+"F0.wireOp",EDGE,"E17.38.41.0"),sQuery(id+"F0.wireOp",EDGE,"E17.42.41.0"),sQuery(id+"F0.wireOp",EDGE,"E17.1.42.0"),sQuery(id+"F0.wireOp",EDGE,"E17.5.42.0"),sQuery(id+"F0.wireOp",EDGE,"E17.13.42.0"),sQuery(id+"F0.wireOp",EDGE,"E17.17.42.0"),sQuery(id+"F0.wireOp",EDGE,"E17.20.42.0"),sQuery(id+"F0.wireOp",EDGE,"E17.24.42.0"),sQuery(id+"F0.wireOp",EDGE,"E17.27.42.0"),sQuery(id+"F0.wireOp",EDGE,"E17.31.42.0"),sQuery(id+"F0.wireOp",EDGE,"E17.38.42.0"),sQuery(id+"F0.wireOp",EDGE,"E17.42.42.0"),sQuery(id+"F0.wireOp",EDGE,"E17.1.43.0"),sQuery(id+"F0.wireOp",EDGE,"E17.5.43.0"),sQuery(id+"F0.wireOp",EDGE,"E17.13.43.0"),sQuery(id+"F0.wireOp",EDGE,"E17.17.43.0"),sQuery(id+"F0.wireOp",EDGE,"E17.20.43.0"),sQuery(id+"F0.wireOp",EDGE,"E17.24.43.0"),sQuery(id+"F0.wireOp",EDGE,"E17.27.43.0"),sQuery(id+"F0.wireOp",EDGE,"E17.31.43.0"),sQuery(id+"F0.wireOp",EDGE,"E17.38.43.0"),sQuery(id+"F0.wireOp",EDGE,"E17.42.43.0"),sQuery(id+"F0.wireOp",EDGE,"E17.1.44.0"),sQuery(id+"F0.wireOp",EDGE,"E17.5.44.0"),sQuery(id+"F0.wireOp",EDGE,"E17.13.44.0"),sQuery(id+"F0.wireOp",EDGE,"E17.17.44.0"),sQuery(id+"F0.wireOp",EDGE,"E17.20.44.0"),sQuery(id+"F0.wireOp",EDGE,"E17.24.44.0"),sQuery(id+"F0.wireOp",EDGE,"E17.27.44.0"),sQuery(id+"F0.wireOp",EDGE,"E17.31.44.0"),sQuery(id+"F0.wireOp",EDGE,"E17.38.44.0"),sQuery(id+"F0.wireOp",EDGE,"E17.42.44.0"),sQuery(id+"F0.wireOp",EDGE,"E17.1.45.0"),sQuery(id+"F0.wireOp",EDGE,"E17.5.45.0"),sQuery(id+"F0.wireOp",EDGE,"E17.13.45.0"),sQuery(id+"F0.wireOp",EDGE,"E17.17.45.0"),sQuery(id+"F0.wireOp",EDGE,"E17.20.45.0"),sQuery(id+"F0.wireOp",EDGE,"E17.24.45.0"),sQuery(id+"F0.wireOp",EDGE,"E17.27.45.0"),sQuery(id+"F0.wireOp",EDGE,"E17.31.45.0"),sQuery(id+"F0.wireOp",EDGE,"E17.38.45.0"),sQuery(id+"F0.wireOp",EDGE,"E17.42.45.0"),sQuery(id+"F0.wireOp",EDGE,"E17.1.46.0"),sQuery(id+"F0.wireOp",EDGE,"E17.5.46.0"),sQuery(id+"F0.wireOp",EDGE,"E17.13.46.0"),sQuery(id+"F0.wireOp",EDGE,"E17.17.46.0"),sQuery(id+"F0.wireOp",EDGE,"E17.20.46.0"),sQuery(id+"F0.wireOp",EDGE,"E17.24.46.0"),sQuery(id+"F0.wireOp",EDGE,"E17.27.46.0"),sQuery(id+"F0.wireOp",EDGE,"E17.31.46.0"),sQuery(id+"F0.wireOp",EDGE,"E17.38.46.0"),sQuery(id+"F0.wireOp",EDGE,"E17.42.46.0"),sQuery(id+"F0.wireOp",EDGE,"E17.1.47.0"),sQuery(id+"F0.wireOp",EDGE,"E17.5.47.0"),sQuery(id+"F0.wireOp",EDGE,"E17.13.47.0"),sQuery(id+"F0.wireOp",EDGE,"E17.17.47.0"),sQuery(id+"F0.wireOp",EDGE,"E17.20.47.0"),sQuery(id+"F0.wireOp",EDGE,"E17.24.47.0"),sQuery(id+"F0.wireOp",EDGE,"E17.27.47.0"),sQuery(id+"F0.wireOp",EDGE,"E17.31.47.0"),sQuery(id+"F0.wireOp",EDGE,"E17.38.47.0"),sQuery(id+"F0.wireOp",EDGE,"E17.42.47.0"),sQuery(id+"F0.wireOp",EDGE,"E17.1.48.0"),sQuery(id+"F0.wireOp",EDGE,"E17.5.48.0"),sQuery(id+"F0.wireOp",EDGE,"E17.13.48.0"),sQuery(id+"F0.wireOp",EDGE,"E17.17.48.0"),sQuery(id+"F0.wireOp",EDGE,"E17.20.48.0"),sQuery(id+"F0.wireOp",EDGE,"E17.24.48.0"),sQuery(id+"F0.wireOp",EDGE,"E17.27.48.0"),sQuery(id+"F0.wireOp",EDGE,"E17.31.48.0"),sQuery(id+"F0.wireOp",EDGE,"E17.38.48.0"),sQuery(id+"F0.wireOp",EDGE,"E17.42.48.0"),sQuery(id+"F0.wireOp",EDGE,"E17.1.49.0"),sQuery(id+"F0.wireOp",EDGE,"E17.5.49.0"),sQuery(id+"F0.wireOp",EDGE,"E17.13.49.0"),sQuery(id+"F0.wireOp",EDGE,"E17.17.49.0"),sQuery(id+"F0.wireOp",EDGE,"E17.24.49.0"),sQuery(id+"F0.wireOp",EDGE,"E17.27.49.0"),sQuery(id+"F0.wireOp",EDGE,"E17.31.49.0"),sQuery(id+"F0.wireOp",EDGE,"E17.38.49.0"),sQuery(id+"F0.wireOp",EDGE,"E17.42.49.0"),sQuery(id+"F0.wireOp",EDGE,"E18"),sQuery(id+"F0.wireOp",EDGE,"E19"),sQuery(id+"F0.wireOp",EDGE,"E20"),sQuery(id+"F0.wireOp",EDGE,"E21")])],"isStart":false});
            var sketch = newSketch(context, id + "F2", { "sketchPlane" : qUnion([Q0])});
            skLineSegment(sketch, "E26", {"start": v(-20.03, 49.12) * mm, "end": v(-20.03, 61.82) * mm});
            skLineSegment(sketch, "E27", {"start": v(-20.03, 61.82) * mm, "end": v(30.77, 61.82) * mm});
            skLineSegment(sketch, "E28", {"start": v(30.77, 61.82) * mm, "end": v(30.77, 49.12) * mm});
            skLineSegment(sketch, "E29", {"start": v(30.77, 49.12) * mm, "end": v(-20.03, 49.12) * mm});
            skLineSegment(sketch, "E30", {"start": v(691.17, 49.12) * mm, "end": v(691.17, 61.82) * mm});
            skLineSegment(sketch, "E31", {"start": v(691.17, 61.82) * mm, "end": v(741.97, 61.82) * mm});
            skLineSegment(sketch, "E32", {"start": v(741.97, 61.82) * mm, "end": v(741.97, 49.12) * mm});
            skLineSegment(sketch, "E33", {"start": v(741.97, 49.12) * mm, "end": v(691.17, 49.12) * mm});
            skSolve(sketch);
        }
        {
            var Q0;
            Q0 = qSketchRegion(id + "F2", true);
            extrude(context, id + "F3", {"entities" : qUnion([Q0]), "operationType" : NewBodyOperationType.ADD, "depth" : 50.8 * mm});
        }
        {
            var Q0;
            Q0=makeQuery(id+"F1.opExtrude","CAP_FACE",FACE,{"disambiguationData":[OSD([sQuery(id+"F0.wireOp",EDGE,"E2.MirrorCS"),sQuery(id+"F0.wireOp",EDGE,"E3.MirrorCS"),sQuery(id+"F0.wireOp",EDGE,"E6.filletArc"),sQuery(id+"F0.wireOp",EDGE,"E7.filletArc"),sQuery(id+"F0.wireOp",EDGE,"E8.filletArc"),sQuery(id+"F0.wireOp",EDGE,"E9.filletArc"),sQuery(id+"F0.wireOp",EDGE,"E10"),sQuery(id+"F0.wireOp",EDGE,"E11"),sQuery(id+"F0.wireOp",EDGE,"E12"),sQuery(id+"F0.wireOp",EDGE,"E15"),sQuery(id+"F0.wireOp",EDGE,"E16.1.0.1"),sQuery(id+"F0.wireOp",EDGE,"E16.1.0.2"),sQuery(id+"F0.wireOp",EDGE,"E16.1.0.7"),sQuery(id+"F0.wireOp",EDGE,"E16.1.0.9"),sQuery(id+"F0.wireOp",EDGE,"E16.1.0.10"),sQuery(id+"F0.wireOp",EDGE,"E16.1.0.12"),sQuery(id+"F0.wireOp",EDGE,"E16.1.0.13"),sQuery(id+"F0.wireOp",EDGE,"E16.1.0.14"),sQuery(id+"F0.wireOp",EDGE,"E16.1.0.16"),sQuery(id+"F0.wireOp",EDGE,"E16.1.0.17"),sQuery(id+"F0.wireOp",EDGE,"E16.2.0.1"),sQuery(id+"F0.wireOp",EDGE,"E16.2.0.2"),sQuery(id+"F0.wireOp",EDGE,"E16.2.0.7"),sQuery(id+"F0.wireOp",EDGE,"E16.2.0.9"),sQuery(id+"F0.wireOp",EDGE,"E16.2.0.10"),sQuery(id+"F0.wireOp",EDGE,"E16.2.0.12"),sQuery(id+"F0.wireOp",EDGE,"E16.2.0.13"),sQuery(id+"F0.wireOp",EDGE,"E16.2.0.14"),sQuery(id+"F0.wireOp",EDGE,"E16.2.0.16"),sQuery(id+"F0.wireOp",EDGE,"E16.2.0.17"),sQuery(id+"F0.wireOp",EDGE,"E17.1.3.0"),sQuery(id+"F0.wireOp",EDGE,"E17.5.3.0"),sQuery(id+"F0.wireOp",EDGE,"E17.13.3.0"),sQuery(id+"F0.wireOp",EDGE,"E17.17.3.0"),sQuery(id+"F0.wireOp",EDGE,"E17.20.3.0"),sQuery(id+"F0.wireOp",EDGE,"E17.24.3.0"),sQuery(id+"F0.wireOp",EDGE,"E17.27.3.0"),sQuery(id+"F0.wireOp",EDGE,"E17.31.3.0"),sQuery(id+"F0.wireOp",EDGE,"E17.38.3.0"),sQuery(id+"F0.wireOp",EDGE,"E17.42.3.0"),sQuery(id+"F0.wireOp",EDGE,"E17.1.4.0"),sQuery(id+"F0.wireOp",EDGE,"E17.5.4.0"),sQuery(id+"F0.wireOp",EDGE,"E17.13.4.0"),sQuery(id+"F0.wireOp",EDGE,"E17.17.4.0"),sQuery(id+"F0.wireOp",EDGE,"E17.20.4.0"),sQuery(id+"F0.wireOp",EDGE,"E17.24.4.0"),sQuery(id+"F0.wireOp",EDGE,"E17.27.4.0"),sQuery(id+"F0.wireOp",EDGE,"E17.31.4.0"),sQuery(id+"F0.wireOp",EDGE,"E17.38.4.0"),sQuery(id+"F0.wireOp",EDGE,"E17.42.4.0"),sQuery(id+"F0.wireOp",EDGE,"E17.1.5.0"),sQuery(id+"F0.wireOp",EDGE,"E17.5.5.0"),sQuery(id+"F0.wireOp",EDGE,"E17.13.5.0"),sQuery(id+"F0.wireOp",EDGE,"E17.17.5.0"),sQuery(id+"F0.wireOp",EDGE,"E17.20.5.0"),sQuery(id+"F0.wireOp",EDGE,"E17.24.5.0"),sQuery(id+"F0.wireOp",EDGE,"E17.27.5.0"),sQuery(id+"F0.wireOp",EDGE,"E17.31.5.0"),sQuery(id+"F0.wireOp",EDGE,"E17.38.5.0"),sQuery(id+"F0.wireOp",EDGE,"E17.42.5.0"),sQuery(id+"F0.wireOp",EDGE,"E17.1.6.0"),sQuery(id+"F0.wireOp",EDGE,"E17.5.6.0"),sQuery(id+"F0.wireOp",EDGE,"E17.13.6.0"),sQuery(id+"F0.wireOp",EDGE,"E17.17.6.0"),sQuery(id+"F0.wireOp",EDGE,"E17.20.6.0"),sQuery(id+"F0.wireOp",EDGE,"E17.24.6.0"),sQuery(id+"F0.wireOp",EDGE,"E17.27.6.0"),sQuery(id+"F0.wireOp",EDGE,"E17.31.6.0"),sQuery(id+"F0.wireOp",EDGE,"E17.38.6.0"),sQuery(id+"F0.wireOp",EDGE,"E17.42.6.0"),sQuery(id+"F0.wireOp",EDGE,"E17.1.7.0"),sQuery(id+"F0.wireOp",EDGE,"E17.5.7.0"),sQuery(id+"F0.wireOp",EDGE,"E17.13.7.0"),sQuery(id+"F0.wireOp",EDGE,"E17.17.7.0"),sQuery(id+"F0.wireOp",EDGE,"E17.20.7.0"),sQuery(id+"F0.wireOp",EDGE,"E17.24.7.0"),sQuery(id+"F0.wireOp",EDGE,"E17.27.7.0"),sQuery(id+"F0.wireOp",EDGE,"E17.31.7.0"),sQuery(id+"F0.wireOp",EDGE,"E17.38.7.0"),sQuery(id+"F0.wireOp",EDGE,"E17.42.7.0"),sQuery(id+"F0.wireOp",EDGE,"E17.1.8.0"),sQuery(id+"F0.wireOp",EDGE,"E17.5.8.0"),sQuery(id+"F0.wireOp",EDGE,"E17.13.8.0"),sQuery(id+"F0.wireOp",EDGE,"E17.17.8.0"),sQuery(id+"F0.wireOp",EDGE,"E17.20.8.0"),sQuery(id+"F0.wireOp",EDGE,"E17.24.8.0"),sQuery(id+"F0.wireOp",EDGE,"E17.27.8.0"),sQuery(id+"F0.wireOp",EDGE,"E17.31.8.0"),sQuery(id+"F0.wireOp",EDGE,"E17.38.8.0"),sQuery(id+"F0.wireOp",EDGE,"E17.42.8.0"),sQuery(id+"F0.wireOp",EDGE,"E17.1.9.0"),sQuery(id+"F0.wireOp",EDGE,"E17.5.9.0"),sQuery(id+"F0.wireOp",EDGE,"E17.13.9.0"),sQuery(id+"F0.wireOp",EDGE,"E17.17.9.0"),sQuery(id+"F0.wireOp",EDGE,"E17.20.9.0"),sQuery(id+"F0.wireOp",EDGE,"E17.24.9.0"),sQuery(id+"F0.wireOp",EDGE,"E17.27.9.0"),sQuery(id+"F0.wireOp",EDGE,"E17.31.9.0"),sQuery(id+"F0.wireOp",EDGE,"E17.38.9.0"),sQuery(id+"F0.wireOp",EDGE,"E17.42.9.0"),sQuery(id+"F0.wireOp",EDGE,"E17.1.10.0"),sQuery(id+"F0.wireOp",EDGE,"E17.5.10.0"),sQuery(id+"F0.wireOp",EDGE,"E17.13.10.0"),sQuery(id+"F0.wireOp",EDGE,"E17.17.10.0"),sQuery(id+"F0.wireOp",EDGE,"E17.20.10.0"),sQuery(id+"F0.wireOp",EDGE,"E17.24.10.0"),sQuery(id+"F0.wireOp",EDGE,"E17.27.10.0"),sQuery(id+"F0.wireOp",EDGE,"E17.31.10.0"),sQuery(id+"F0.wireOp",EDGE,"E17.38.10.0"),sQuery(id+"F0.wireOp",EDGE,"E17.42.10.0"),sQuery(id+"F0.wireOp",EDGE,"E17.1.11.0"),sQuery(id+"F0.wireOp",EDGE,"E17.5.11.0"),sQuery(id+"F0.wireOp",EDGE,"E17.13.11.0"),sQuery(id+"F0.wireOp",EDGE,"E17.17.11.0"),sQuery(id+"F0.wireOp",EDGE,"E17.20.11.0"),sQuery(id+"F0.wireOp",EDGE,"E17.24.11.0"),sQuery(id+"F0.wireOp",EDGE,"E17.27.11.0"),sQuery(id+"F0.wireOp",EDGE,"E17.31.11.0"),sQuery(id+"F0.wireOp",EDGE,"E17.38.11.0"),sQuery(id+"F0.wireOp",EDGE,"E17.42.11.0"),sQuery(id+"F0.wireOp",EDGE,"E17.1.12.0"),sQuery(id+"F0.wireOp",EDGE,"E17.5.12.0"),sQuery(id+"F0.wireOp",EDGE,"E17.13.12.0"),sQuery(id+"F0.wireOp",EDGE,"E17.17.12.0"),sQuery(id+"F0.wireOp",EDGE,"E17.20.12.0"),sQuery(id+"F0.wireOp",EDGE,"E17.24.12.0"),sQuery(id+"F0.wireOp",EDGE,"E17.27.12.0"),sQuery(id+"F0.wireOp",EDGE,"E17.31.12.0"),sQuery(id+"F0.wireOp",EDGE,"E17.38.12.0"),sQuery(id+"F0.wireOp",EDGE,"E17.42.12.0"),sQuery(id+"F0.wireOp",EDGE,"E17.1.13.0"),sQuery(id+"F0.wireOp",EDGE,"E17.5.13.0"),sQuery(id+"F0.wireOp",EDGE,"E17.13.13.0"),sQuery(id+"F0.wireOp",EDGE,"E17.17.13.0"),sQuery(id+"F0.wireOp",EDGE,"E17.20.13.0"),sQuery(id+"F0.wireOp",EDGE,"E17.24.13.0"),sQuery(id+"F0.wireOp",EDGE,"E17.27.13.0"),sQuery(id+"F0.wireOp",EDGE,"E17.31.13.0"),sQuery(id+"F0.wireOp",EDGE,"E17.38.13.0"),sQuery(id+"F0.wireOp",EDGE,"E17.42.13.0"),sQuery(id+"F0.wireOp",EDGE,"E17.1.14.0"),sQuery(id+"F0.wireOp",EDGE,"E17.5.14.0"),sQuery(id+"F0.wireOp",EDGE,"E17.13.14.0"),sQuery(id+"F0.wireOp",EDGE,"E17.17.14.0"),sQuery(id+"F0.wireOp",EDGE,"E17.20.14.0"),sQuery(id+"F0.wireOp",EDGE,"E17.24.14.0"),sQuery(id+"F0.wireOp",EDGE,"E17.27.14.0"),sQuery(id+"F0.wireOp",EDGE,"E17.31.14.0"),sQuery(id+"F0.wireOp",EDGE,"E17.38.14.0"),sQuery(id+"F0.wireOp",EDGE,"E17.42.14.0"),sQuery(id+"F0.wireOp",EDGE,"E17.1.15.0"),sQuery(id+"F0.wireOp",EDGE,"E17.5.15.0"),sQuery(id+"F0.wireOp",EDGE,"E17.13.15.0"),sQuery(id+"F0.wireOp",EDGE,"E17.17.15.0"),sQuery(id+"F0.wireOp",EDGE,"E17.20.15.0"),sQuery(id+"F0.wireOp",EDGE,"E17.24.15.0"),sQuery(id+"F0.wireOp",EDGE,"E17.27.15.0"),sQuery(id+"F0.wireOp",EDGE,"E17.31.15.0"),sQuery(id+"F0.wireOp",EDGE,"E17.38.15.0"),sQuery(id+"F0.wireOp",EDGE,"E17.42.15.0"),sQuery(id+"F0.wireOp",EDGE,"E17.1.16.0"),sQuery(id+"F0.wireOp",EDGE,"E17.5.16.0"),sQuery(id+"F0.wireOp",EDGE,"E17.13.16.0"),sQuery(id+"F0.wireOp",EDGE,"E17.17.16.0"),sQuery(id+"F0.wireOp",EDGE,"E17.20.16.0"),sQuery(id+"F0.wireOp",EDGE,"E17.24.16.0"),sQuery(id+"F0.wireOp",EDGE,"E17.27.16.0"),sQuery(id+"F0.wireOp",EDGE,"E17.31.16.0"),sQuery(id+"F0.wireOp",EDGE,"E17.38.16.0"),sQuery(id+"F0.wireOp",EDGE,"E17.42.16.0"),sQuery(id+"F0.wireOp",EDGE,"E17.1.17.0"),sQuery(id+"F0.wireOp",EDGE,"E17.5.17.0"),sQuery(id+"F0.wireOp",EDGE,"E17.13.17.0"),sQuery(id+"F0.wireOp",EDGE,"E17.17.17.0"),sQuery(id+"F0.wireOp",EDGE,"E17.20.17.0"),sQuery(id+"F0.wireOp",EDGE,"E17.24.17.0"),sQuery(id+"F0.wireOp",EDGE,"E17.27.17.0"),sQuery(id+"F0.wireOp",EDGE,"E17.31.17.0"),sQuery(id+"F0.wireOp",EDGE,"E17.38.17.0"),sQuery(id+"F0.wireOp",EDGE,"E17.42.17.0"),sQuery(id+"F0.wireOp",EDGE,"E17.1.18.0"),sQuery(id+"F0.wireOp",EDGE,"E17.5.18.0"),sQuery(id+"F0.wireOp",EDGE,"E17.13.18.0"),sQuery(id+"F0.wireOp",EDGE,"E17.17.18.0"),sQuery(id+"F0.wireOp",EDGE,"E17.20.18.0"),sQuery(id+"F0.wireOp",EDGE,"E17.24.18.0"),sQuery(id+"F0.wireOp",EDGE,"E17.27.18.0"),sQuery(id+"F0.wireOp",EDGE,"E17.31.18.0"),sQuery(id+"F0.wireOp",EDGE,"E17.38.18.0"),sQuery(id+"F0.wireOp",EDGE,"E17.42.18.0"),sQuery(id+"F0.wireOp",EDGE,"E17.1.19.0"),sQuery(id+"F0.wireOp",EDGE,"E17.5.19.0"),sQuery(id+"F0.wireOp",EDGE,"E17.13.19.0"),sQuery(id+"F0.wireOp",EDGE,"E17.17.19.0"),sQuery(id+"F0.wireOp",EDGE,"E17.20.19.0"),sQuery(id+"F0.wireOp",EDGE,"E17.24.19.0"),sQuery(id+"F0.wireOp",EDGE,"E17.27.19.0"),sQuery(id+"F0.wireOp",EDGE,"E17.31.19.0"),sQuery(id+"F0.wireOp",EDGE,"E17.38.19.0"),sQuery(id+"F0.wireOp",EDGE,"E17.42.19.0"),sQuery(id+"F0.wireOp",EDGE,"E17.1.20.0"),sQuery(id+"F0.wireOp",EDGE,"E17.5.20.0"),sQuery(id+"F0.wireOp",EDGE,"E17.13.20.0"),sQuery(id+"F0.wireOp",EDGE,"E17.17.20.0"),sQuery(id+"F0.wireOp",EDGE,"E17.20.20.0"),sQuery(id+"F0.wireOp",EDGE,"E17.24.20.0"),sQuery(id+"F0.wireOp",EDGE,"E17.27.20.0"),sQuery(id+"F0.wireOp",EDGE,"E17.31.20.0"),sQuery(id+"F0.wireOp",EDGE,"E17.38.20.0"),sQuery(id+"F0.wireOp",EDGE,"E17.42.20.0"),sQuery(id+"F0.wireOp",EDGE,"E17.1.21.0"),sQuery(id+"F0.wireOp",EDGE,"E17.5.21.0"),sQuery(id+"F0.wireOp",EDGE,"E17.13.21.0"),sQuery(id+"F0.wireOp",EDGE,"E17.17.21.0"),sQuery(id+"F0.wireOp",EDGE,"E17.20.21.0"),sQuery(id+"F0.wireOp",EDGE,"E17.24.21.0"),sQuery(id+"F0.wireOp",EDGE,"E17.27.21.0"),sQuery(id+"F0.wireOp",EDGE,"E17.31.21.0"),sQuery(id+"F0.wireOp",EDGE,"E17.38.21.0"),sQuery(id+"F0.wireOp",EDGE,"E17.42.21.0"),sQuery(id+"F0.wireOp",EDGE,"E17.1.22.0"),sQuery(id+"F0.wireOp",EDGE,"E17.5.22.0"),sQuery(id+"F0.wireOp",EDGE,"E17.13.22.0"),sQuery(id+"F0.wireOp",EDGE,"E17.17.22.0"),sQuery(id+"F0.wireOp",EDGE,"E17.20.22.0"),sQuery(id+"F0.wireOp",EDGE,"E17.24.22.0"),sQuery(id+"F0.wireOp",EDGE,"E17.27.22.0"),sQuery(id+"F0.wireOp",EDGE,"E17.31.22.0"),sQuery(id+"F0.wireOp",EDGE,"E17.38.22.0"),sQuery(id+"F0.wireOp",EDGE,"E17.42.22.0"),sQuery(id+"F0.wireOp",EDGE,"E17.1.23.0"),sQuery(id+"F0.wireOp",EDGE,"E17.5.23.0"),sQuery(id+"F0.wireOp",EDGE,"E17.13.23.0"),sQuery(id+"F0.wireOp",EDGE,"E17.17.23.0"),sQuery(id+"F0.wireOp",EDGE,"E17.20.23.0"),sQuery(id+"F0.wireOp",EDGE,"E17.24.23.0"),sQuery(id+"F0.wireOp",EDGE,"E17.27.23.0"),sQuery(id+"F0.wireOp",EDGE,"E17.31.23.0"),sQuery(id+"F0.wireOp",EDGE,"E17.38.23.0"),sQuery(id+"F0.wireOp",EDGE,"E17.42.23.0"),sQuery(id+"F0.wireOp",EDGE,"E17.1.24.0"),sQuery(id+"F0.wireOp",EDGE,"E17.5.24.0"),sQuery(id+"F0.wireOp",EDGE,"E17.13.24.0"),sQuery(id+"F0.wireOp",EDGE,"E17.17.24.0"),sQuery(id+"F0.wireOp",EDGE,"E17.20.24.0"),sQuery(id+"F0.wireOp",EDGE,"E17.24.24.0"),sQuery(id+"F0.wireOp",EDGE,"E17.27.24.0"),sQuery(id+"F0.wireOp",EDGE,"E17.31.24.0"),sQuery(id+"F0.wireOp",EDGE,"E17.38.24.0"),sQuery(id+"F0.wireOp",EDGE,"E17.42.24.0"),sQuery(id+"F0.wireOp",EDGE,"E17.1.25.0"),sQuery(id+"F0.wireOp",EDGE,"E17.5.25.0"),sQuery(id+"F0.wireOp",EDGE,"E17.13.25.0"),sQuery(id+"F0.wireOp",EDGE,"E17.17.25.0"),sQuery(id+"F0.wireOp",EDGE,"E17.20.25.0"),sQuery(id+"F0.wireOp",EDGE,"E17.24.25.0"),sQuery(id+"F0.wireOp",EDGE,"E17.27.25.0"),sQuery(id+"F0.wireOp",EDGE,"E17.31.25.0"),sQuery(id+"F0.wireOp",EDGE,"E17.38.25.0"),sQuery(id+"F0.wireOp",EDGE,"E17.42.25.0"),sQuery(id+"F0.wireOp",EDGE,"E17.1.26.0"),sQuery(id+"F0.wireOp",EDGE,"E17.5.26.0"),sQuery(id+"F0.wireOp",EDGE,"E17.13.26.0"),sQuery(id+"F0.wireOp",EDGE,"E17.17.26.0"),sQuery(id+"F0.wireOp",EDGE,"E17.20.26.0"),sQuery(id+"F0.wireOp",EDGE,"E17.24.26.0"),sQuery(id+"F0.wireOp",EDGE,"E17.27.26.0"),sQuery(id+"F0.wireOp",EDGE,"E17.31.26.0"),sQuery(id+"F0.wireOp",EDGE,"E17.38.26.0"),sQuery(id+"F0.wireOp",EDGE,"E17.42.26.0"),sQuery(id+"F0.wireOp",EDGE,"E17.1.27.0"),sQuery(id+"F0.wireOp",EDGE,"E17.5.27.0"),sQuery(id+"F0.wireOp",EDGE,"E17.13.27.0"),sQuery(id+"F0.wireOp",EDGE,"E17.17.27.0"),sQuery(id+"F0.wireOp",EDGE,"E17.20.27.0"),sQuery(id+"F0.wireOp",EDGE,"E17.24.27.0"),sQuery(id+"F0.wireOp",EDGE,"E17.27.27.0"),sQuery(id+"F0.wireOp",EDGE,"E17.31.27.0"),sQuery(id+"F0.wireOp",EDGE,"E17.38.27.0"),sQuery(id+"F0.wireOp",EDGE,"E17.42.27.0"),sQuery(id+"F0.wireOp",EDGE,"E17.1.28.0"),sQuery(id+"F0.wireOp",EDGE,"E17.5.28.0"),sQuery(id+"F0.wireOp",EDGE,"E17.13.28.0"),sQuery(id+"F0.wireOp",EDGE,"E17.17.28.0"),sQuery(id+"F0.wireOp",EDGE,"E17.20.28.0"),sQuery(id+"F0.wireOp",EDGE,"E17.24.28.0"),sQuery(id+"F0.wireOp",EDGE,"E17.27.28.0"),sQuery(id+"F0.wireOp",EDGE,"E17.31.28.0"),sQuery(id+"F0.wireOp",EDGE,"E17.38.28.0"),sQuery(id+"F0.wireOp",EDGE,"E17.42.28.0"),sQuery(id+"F0.wireOp",EDGE,"E17.1.29.0"),sQuery(id+"F0.wireOp",EDGE,"E17.5.29.0"),sQuery(id+"F0.wireOp",EDGE,"E17.13.29.0"),sQuery(id+"F0.wireOp",EDGE,"E17.17.29.0"),sQuery(id+"F0.wireOp",EDGE,"E17.20.29.0"),sQuery(id+"F0.wireOp",EDGE,"E17.24.29.0"),sQuery(id+"F0.wireOp",EDGE,"E17.27.29.0"),sQuery(id+"F0.wireOp",EDGE,"E17.31.29.0"),sQuery(id+"F0.wireOp",EDGE,"E17.38.29.0"),sQuery(id+"F0.wireOp",EDGE,"E17.42.29.0"),sQuery(id+"F0.wireOp",EDGE,"E17.1.30.0"),sQuery(id+"F0.wireOp",EDGE,"E17.5.30.0"),sQuery(id+"F0.wireOp",EDGE,"E17.13.30.0"),sQuery(id+"F0.wireOp",EDGE,"E17.17.30.0"),sQuery(id+"F0.wireOp",EDGE,"E17.20.30.0"),sQuery(id+"F0.wireOp",EDGE,"E17.24.30.0"),sQuery(id+"F0.wireOp",EDGE,"E17.27.30.0"),sQuery(id+"F0.wireOp",EDGE,"E17.31.30.0"),sQuery(id+"F0.wireOp",EDGE,"E17.38.30.0"),sQuery(id+"F0.wireOp",EDGE,"E17.42.30.0"),sQuery(id+"F0.wireOp",EDGE,"E17.1.31.0"),sQuery(id+"F0.wireOp",EDGE,"E17.5.31.0"),sQuery(id+"F0.wireOp",EDGE,"E17.13.31.0"),sQuery(id+"F0.wireOp",EDGE,"E17.17.31.0"),sQuery(id+"F0.wireOp",EDGE,"E17.20.31.0"),sQuery(id+"F0.wireOp",EDGE,"E17.24.31.0"),sQuery(id+"F0.wireOp",EDGE,"E17.27.31.0"),sQuery(id+"F0.wireOp",EDGE,"E17.31.31.0"),sQuery(id+"F0.wireOp",EDGE,"E17.38.31.0"),sQuery(id+"F0.wireOp",EDGE,"E17.42.31.0"),sQuery(id+"F0.wireOp",EDGE,"E17.1.32.0"),sQuery(id+"F0.wireOp",EDGE,"E17.5.32.0"),sQuery(id+"F0.wireOp",EDGE,"E17.13.32.0"),sQuery(id+"F0.wireOp",EDGE,"E17.17.32.0"),sQuery(id+"F0.wireOp",EDGE,"E17.20.32.0"),sQuery(id+"F0.wireOp",EDGE,"E17.24.32.0"),sQuery(id+"F0.wireOp",EDGE,"E17.27.32.0"),sQuery(id+"F0.wireOp",EDGE,"E17.31.32.0"),sQuery(id+"F0.wireOp",EDGE,"E17.38.32.0"),sQuery(id+"F0.wireOp",EDGE,"E17.42.32.0"),sQuery(id+"F0.wireOp",EDGE,"E17.1.33.0"),sQuery(id+"F0.wireOp",EDGE,"E17.5.33.0"),sQuery(id+"F0.wireOp",EDGE,"E17.13.33.0"),sQuery(id+"F0.wireOp",EDGE,"E17.17.33.0"),sQuery(id+"F0.wireOp",EDGE,"E17.20.33.0"),sQuery(id+"F0.wireOp",EDGE,"E17.24.33.0"),sQuery(id+"F0.wireOp",EDGE,"E17.27.33.0"),sQuery(id+"F0.wireOp",EDGE,"E17.31.33.0"),sQuery(id+"F0.wireOp",EDGE,"E17.38.33.0"),sQuery(id+"F0.wireOp",EDGE,"E17.42.33.0"),sQuery(id+"F0.wireOp",EDGE,"E17.1.34.0"),sQuery(id+"F0.wireOp",EDGE,"E17.5.34.0"),sQuery(id+"F0.wireOp",EDGE,"E17.13.34.0"),sQuery(id+"F0.wireOp",EDGE,"E17.17.34.0"),sQuery(id+"F0.wireOp",EDGE,"E17.20.34.0"),sQuery(id+"F0.wireOp",EDGE,"E17.24.34.0"),sQuery(id+"F0.wireOp",EDGE,"E17.27.34.0"),sQuery(id+"F0.wireOp",EDGE,"E17.31.34.0"),sQuery(id+"F0.wireOp",EDGE,"E17.38.34.0"),sQuery(id+"F0.wireOp",EDGE,"E17.42.34.0"),sQuery(id+"F0.wireOp",EDGE,"E17.1.35.0"),sQuery(id+"F0.wireOp",EDGE,"E17.5.35.0"),sQuery(id+"F0.wireOp",EDGE,"E17.13.35.0"),sQuery(id+"F0.wireOp",EDGE,"E17.17.35.0"),sQuery(id+"F0.wireOp",EDGE,"E17.20.35.0"),sQuery(id+"F0.wireOp",EDGE,"E17.24.35.0"),sQuery(id+"F0.wireOp",EDGE,"E17.27.35.0"),sQuery(id+"F0.wireOp",EDGE,"E17.31.35.0"),sQuery(id+"F0.wireOp",EDGE,"E17.38.35.0"),sQuery(id+"F0.wireOp",EDGE,"E17.42.35.0"),sQuery(id+"F0.wireOp",EDGE,"E17.1.36.0"),sQuery(id+"F0.wireOp",EDGE,"E17.5.36.0"),sQuery(id+"F0.wireOp",EDGE,"E17.13.36.0"),sQuery(id+"F0.wireOp",EDGE,"E17.17.36.0"),sQuery(id+"F0.wireOp",EDGE,"E17.20.36.0"),sQuery(id+"F0.wireOp",EDGE,"E17.24.36.0"),sQuery(id+"F0.wireOp",EDGE,"E17.27.36.0"),sQuery(id+"F0.wireOp",EDGE,"E17.31.36.0"),sQuery(id+"F0.wireOp",EDGE,"E17.38.36.0"),sQuery(id+"F0.wireOp",EDGE,"E17.42.36.0"),sQuery(id+"F0.wireOp",EDGE,"E17.1.37.0"),sQuery(id+"F0.wireOp",EDGE,"E17.5.37.0"),sQuery(id+"F0.wireOp",EDGE,"E17.13.37.0"),sQuery(id+"F0.wireOp",EDGE,"E17.17.37.0"),sQuery(id+"F0.wireOp",EDGE,"E17.20.37.0"),sQuery(id+"F0.wireOp",EDGE,"E17.24.37.0"),sQuery(id+"F0.wireOp",EDGE,"E17.27.37.0"),sQuery(id+"F0.wireOp",EDGE,"E17.31.37.0"),sQuery(id+"F0.wireOp",EDGE,"E17.38.37.0"),sQuery(id+"F0.wireOp",EDGE,"E17.42.37.0"),sQuery(id+"F0.wireOp",EDGE,"E17.1.38.0"),sQuery(id+"F0.wireOp",EDGE,"E17.5.38.0"),sQuery(id+"F0.wireOp",EDGE,"E17.13.38.0"),sQuery(id+"F0.wireOp",EDGE,"E17.17.38.0"),sQuery(id+"F0.wireOp",EDGE,"E17.20.38.0"),sQuery(id+"F0.wireOp",EDGE,"E17.24.38.0"),sQuery(id+"F0.wireOp",EDGE,"E17.27.38.0"),sQuery(id+"F0.wireOp",EDGE,"E17.31.38.0"),sQuery(id+"F0.wireOp",EDGE,"E17.38.38.0"),sQuery(id+"F0.wireOp",EDGE,"E17.42.38.0"),sQuery(id+"F0.wireOp",EDGE,"E17.1.39.0"),sQuery(id+"F0.wireOp",EDGE,"E17.5.39.0"),sQuery(id+"F0.wireOp",EDGE,"E17.13.39.0"),sQuery(id+"F0.wireOp",EDGE,"E17.17.39.0"),sQuery(id+"F0.wireOp",EDGE,"E17.20.39.0"),sQuery(id+"F0.wireOp",EDGE,"E17.24.39.0"),sQuery(id+"F0.wireOp",EDGE,"E17.27.39.0"),sQuery(id+"F0.wireOp",EDGE,"E17.31.39.0"),sQuery(id+"F0.wireOp",EDGE,"E17.38.39.0"),sQuery(id+"F0.wireOp",EDGE,"E17.42.39.0"),sQuery(id+"F0.wireOp",EDGE,"E17.1.40.0"),sQuery(id+"F0.wireOp",EDGE,"E17.5.40.0"),sQuery(id+"F0.wireOp",EDGE,"E17.13.40.0"),sQuery(id+"F0.wireOp",EDGE,"E17.17.40.0"),sQuery(id+"F0.wireOp",EDGE,"E17.20.40.0"),sQuery(id+"F0.wireOp",EDGE,"E17.24.40.0"),sQuery(id+"F0.wireOp",EDGE,"E17.27.40.0"),sQuery(id+"F0.wireOp",EDGE,"E17.31.40.0"),sQuery(id+"F0.wireOp",EDGE,"E17.38.40.0"),sQuery(id+"F0.wireOp",EDGE,"E17.42.40.0"),sQuery(id+"F0.wireOp",EDGE,"E17.1.41.0"),sQuery(id+"F0.wireOp",EDGE,"E17.5.41.0"),sQuery(id+"F0.wireOp",EDGE,"E17.13.41.0"),sQuery(id+"F0.wireOp",EDGE,"E17.17.41.0"),sQuery(id+"F0.wireOp",EDGE,"E17.20.41.0"),sQuery(id+"F0.wireOp",EDGE,"E17.24.41.0"),sQuery(id+"F0.wireOp",EDGE,"E17.27.41.0"),sQuery(id+"F0.wireOp",EDGE,"E17.31.41.0"),sQuery(id+"F0.wireOp",EDGE,"E17.38.41.0"),sQuery(id+"F0.wireOp",EDGE,"E17.42.41.0"),sQuery(id+"F0.wireOp",EDGE,"E17.1.42.0"),sQuery(id+"F0.wireOp",EDGE,"E17.5.42.0"),sQuery(id+"F0.wireOp",EDGE,"E17.13.42.0"),sQuery(id+"F0.wireOp",EDGE,"E17.17.42.0"),sQuery(id+"F0.wireOp",EDGE,"E17.20.42.0"),sQuery(id+"F0.wireOp",EDGE,"E17.24.42.0"),sQuery(id+"F0.wireOp",EDGE,"E17.27.42.0"),sQuery(id+"F0.wireOp",EDGE,"E17.31.42.0"),sQuery(id+"F0.wireOp",EDGE,"E17.38.42.0"),sQuery(id+"F0.wireOp",EDGE,"E17.42.42.0"),sQuery(id+"F0.wireOp",EDGE,"E17.1.43.0"),sQuery(id+"F0.wireOp",EDGE,"E17.5.43.0"),sQuery(id+"F0.wireOp",EDGE,"E17.13.43.0"),sQuery(id+"F0.wireOp",EDGE,"E17.17.43.0"),sQuery(id+"F0.wireOp",EDGE,"E17.20.43.0"),sQuery(id+"F0.wireOp",EDGE,"E17.24.43.0"),sQuery(id+"F0.wireOp",EDGE,"E17.27.43.0"),sQuery(id+"F0.wireOp",EDGE,"E17.31.43.0"),sQuery(id+"F0.wireOp",EDGE,"E17.38.43.0"),sQuery(id+"F0.wireOp",EDGE,"E17.42.43.0"),sQuery(id+"F0.wireOp",EDGE,"E17.1.44.0"),sQuery(id+"F0.wireOp",EDGE,"E17.5.44.0"),sQuery(id+"F0.wireOp",EDGE,"E17.13.44.0"),sQuery(id+"F0.wireOp",EDGE,"E17.17.44.0"),sQuery(id+"F0.wireOp",EDGE,"E17.20.44.0"),sQuery(id+"F0.wireOp",EDGE,"E17.24.44.0"),sQuery(id+"F0.wireOp",EDGE,"E17.27.44.0"),sQuery(id+"F0.wireOp",EDGE,"E17.31.44.0"),sQuery(id+"F0.wireOp",EDGE,"E17.38.44.0"),sQuery(id+"F0.wireOp",EDGE,"E17.42.44.0"),sQuery(id+"F0.wireOp",EDGE,"E17.1.45.0"),sQuery(id+"F0.wireOp",EDGE,"E17.5.45.0"),sQuery(id+"F0.wireOp",EDGE,"E17.13.45.0"),sQuery(id+"F0.wireOp",EDGE,"E17.17.45.0"),sQuery(id+"F0.wireOp",EDGE,"E17.20.45.0"),sQuery(id+"F0.wireOp",EDGE,"E17.24.45.0"),sQuery(id+"F0.wireOp",EDGE,"E17.27.45.0"),sQuery(id+"F0.wireOp",EDGE,"E17.31.45.0"),sQuery(id+"F0.wireOp",EDGE,"E17.38.45.0"),sQuery(id+"F0.wireOp",EDGE,"E17.42.45.0"),sQuery(id+"F0.wireOp",EDGE,"E17.1.46.0"),sQuery(id+"F0.wireOp",EDGE,"E17.5.46.0"),sQuery(id+"F0.wireOp",EDGE,"E17.13.46.0"),sQuery(id+"F0.wireOp",EDGE,"E17.17.46.0"),sQuery(id+"F0.wireOp",EDGE,"E17.20.46.0"),sQuery(id+"F0.wireOp",EDGE,"E17.24.46.0"),sQuery(id+"F0.wireOp",EDGE,"E17.27.46.0"),sQuery(id+"F0.wireOp",EDGE,"E17.31.46.0"),sQuery(id+"F0.wireOp",EDGE,"E17.38.46.0"),sQuery(id+"F0.wireOp",EDGE,"E17.42.46.0"),sQuery(id+"F0.wireOp",EDGE,"E17.1.47.0"),sQuery(id+"F0.wireOp",EDGE,"E17.5.47.0"),sQuery(id+"F0.wireOp",EDGE,"E17.13.47.0"),sQuery(id+"F0.wireOp",EDGE,"E17.17.47.0"),sQuery(id+"F0.wireOp",EDGE,"E17.20.47.0"),sQuery(id+"F0.wireOp",EDGE,"E17.24.47.0"),sQuery(id+"F0.wireOp",EDGE,"E17.27.47.0"),sQuery(id+"F0.wireOp",EDGE,"E17.31.47.0"),sQuery(id+"F0.wireOp",EDGE,"E17.38.47.0"),sQuery(id+"F0.wireOp",EDGE,"E17.42.47.0"),sQuery(id+"F0.wireOp",EDGE,"E17.1.48.0"),sQuery(id+"F0.wireOp",EDGE,"E17.5.48.0"),sQuery(id+"F0.wireOp",EDGE,"E17.13.48.0"),sQuery(id+"F0.wireOp",EDGE,"E17.17.48.0"),sQuery(id+"F0.wireOp",EDGE,"E17.20.48.0"),sQuery(id+"F0.wireOp",EDGE,"E17.24.48.0"),sQuery(id+"F0.wireOp",EDGE,"E17.27.48.0"),sQuery(id+"F0.wireOp",EDGE,"E17.31.48.0"),sQuery(id+"F0.wireOp",EDGE,"E17.38.48.0"),sQuery(id+"F0.wireOp",EDGE,"E17.42.48.0"),sQuery(id+"F0.wireOp",EDGE,"E17.1.49.0"),sQuery(id+"F0.wireOp",EDGE,"E17.5.49.0"),sQuery(id+"F0.wireOp",EDGE,"E17.13.49.0"),sQuery(id+"F0.wireOp",EDGE,"E17.17.49.0"),sQuery(id+"F0.wireOp",EDGE,"E17.24.49.0"),sQuery(id+"F0.wireOp",EDGE,"E17.27.49.0"),sQuery(id+"F0.wireOp",EDGE,"E17.31.49.0"),sQuery(id+"F0.wireOp",EDGE,"E17.38.49.0"),sQuery(id+"F0.wireOp",EDGE,"E17.42.49.0"),sQuery(id+"F0.wireOp",EDGE,"E18"),sQuery(id+"F0.wireOp",EDGE,"E19"),sQuery(id+"F0.wireOp",EDGE,"E20"),sQuery(id+"F0.wireOp",EDGE,"E21")])],"isStart":true});
            var sketch = newSketch(context, id + "F4", { "sketchPlane" : qUnion([Q0])});
            skLineSegment(sketch, "E34", {"start": v(-30.77, 49.12) * mm, "end": v(-30.77, 61.82) * mm});
            skLineSegment(sketch, "E35", {"start": v(-30.77, 61.82) * mm, "end": v(20.03, 61.82) * mm});
            skLineSegment(sketch, "E36", {"start": v(20.03, 61.82) * mm, "end": v(20.03, 49.12) * mm});
            skLineSegment(sketch, "E37", {"start": v(20.03, 49.12) * mm, "end": v(-30.77, 49.12) * mm});
            skLineSegment(sketch, "E38", {"start": v(-741.97, 49.12) * mm, "end": v(-741.97, 61.82) * mm});
            skLineSegment(sketch, "E39", {"start": v(-741.97, 61.82) * mm, "end": v(-691.17, 61.82) * mm});
            skLineSegment(sketch, "E40", {"start": v(-691.17, 61.82) * mm, "end": v(-691.17, 49.12) * mm});
            skLineSegment(sketch, "E41", {"start": v(-691.17, 49.12) * mm, "end": v(-741.97, 49.12) * mm});
            skSolve(sketch);
        }
        {
            var Q0;
            Q0 = qSketchRegion(id + "F4", true);
            extrude(context, id + "F5", {"entities" : qUnion([Q0]), "operationType" : NewBodyOperationType.ADD, "depth" : 50.8 * mm});
        }
        {
            var Q0;
            Q0=makeQuery(id+"F3.opExtrude","CAP_EDGE",EDGE,{"disambiguationData":[OSD([sQuery(id+"F2.wireOp",EDGE,"E26")])],"isStart":false});
            var Q1;
            Q1=makeQuery(id+"F3.opExtrude","CAP_EDGE",EDGE,{"disambiguationData":[OSD([sQuery(id+"F2.wireOp",EDGE,"E28")])],"isStart":false});
            var Q2;
            Q2=makeQuery(id+"F5.opExtrude","CAP_EDGE",EDGE,{"disambiguationData":[OSD([sQuery(id+"F4.wireOp",EDGE,"E34")])],"isStart":false});
            var Q3;
            Q3=makeQuery(id+"F5.opExtrude","CAP_EDGE",EDGE,{"disambiguationData":[OSD([sQuery(id+"F4.wireOp",EDGE,"E36")])],"isStart":false});
            var Q4;
            Q4=makeQuery(id+"F3.opExtrude","CAP_EDGE",EDGE,{"disambiguationData":[OSD([sQuery(id+"F2.wireOp",EDGE,"E32")])],"isStart":false});
            var Q5;
            Q5=makeQuery(id+"F3.opExtrude","CAP_EDGE",EDGE,{"disambiguationData":[OSD([sQuery(id+"F2.wireOp",EDGE,"E30")])],"isStart":false});
            var Q6;
            Q6=makeQuery(id+"F5.opExtrude","CAP_EDGE",EDGE,{"disambiguationData":[OSD([sQuery(id+"F4.wireOp",EDGE,"E40")])],"isStart":false});
            var Q7;
            Q7=makeQuery(id+"F5.opExtrude","CAP_EDGE",EDGE,{"disambiguationData":[OSD([sQuery(id+"F4.wireOp",EDGE,"E38")])],"isStart":false});
            fillet(context, id + "F6", {"entities" : qUnion([Q0, Q1, Q2, Q3, Q4, Q5, Q6, Q7]), "radius" : 12.7 * mm, "tangentPropagation" : true, "allowEdgeOverflow" : false});
        }
        {
            var Q0;
            Q0=makeQuery(id+"F5.opExtrude","SWEPT_FACE",FACE,{"disambiguationData":[OSD([sQuery(id+"F4.wireOp",EDGE,"E35")])]});
            var sketch = newSketch(context, id + "F7", { "sketchPlane" : qUnion([Q0])});
            skLineSegment(sketch, "E42", {"start": v(30.77, 0) * mm, "end": v(30.77, 25.4) * mm});
            skPoint(sketch, "E43", {"position": v(-7.33, 25.4) * mm});
            skPoint(sketch, "E44", {"position": v(18.07, 25.4) * mm});
            skSolve(sketch);
        }
        {
            var Q0;
            Q0=makeQuery(id+"F3.opExtrude","SWEPT_FACE",FACE,{"disambiguationData":[OSD([sQuery(id+"F2.wireOp",EDGE,"E27")])]});
            var sketch = newSketch(context, id + "F8", { "sketchPlane" : qUnion([Q0])});
            skPoint(sketch, "E45", {"position": v(18.07, -152.4) * mm});
            skPoint(sketch, "E46", {"position": v(-7.33, -152.4) * mm});
            skSolve(sketch);
        }
        {
            var Q0;
            Q0=makeQuery(id+"F3.opExtrude","SWEPT_FACE",FACE,{"disambiguationData":[OSD([sQuery(id+"F2.wireOp",EDGE,"E31")])]});
            var sketch = newSketch(context, id + "F9", { "sketchPlane" : qUnion([Q0])});
            skPoint(sketch, "E47", {"position": v(729.27, -152.4) * mm});
            skPoint(sketch, "E48", {"position": v(703.87, -152.4) * mm});
            skSolve(sketch);
        }
        {
            var Q0;
            Q0=makeQuery(id+"F5.opExtrude","SWEPT_FACE",FACE,{"disambiguationData":[OSD([sQuery(id+"F4.wireOp",EDGE,"E39")])]});
            var sketch = newSketch(context, id + "F10", { "sketchPlane" : qUnion([Q0])});
            skPoint(sketch, "E49", {"position": v(703.87, 25.4) * mm});
            skPoint(sketch, "E50", {"position": v(729.27, 25.4) * mm});
            skSolve(sketch);
        }
        {
            var Q0;
            Q0=sQuery(id+"F10.wireOp",VERTEX,"E49");
            var Q1;
            Q1=sQuery(id+"F10.wireOp",VERTEX,"E50");
            var Q2;
            Q2=sQuery(id+"F9.wireOp",VERTEX,"E48");
            var Q3;
            Q3=sQuery(id+"F9.wireOp",VERTEX,"E47");
            var Q4;
            Q4=sQuery(id+"F7.wireOp",VERTEX,"E43");
            var Q5;
            Q5=sQuery(id+"F7.wireOp",VERTEX,"E44");
            var Q6;
            Q6=sQuery(id+"F8.wireOp",VERTEX,"E45");
            var Q7;
            Q7=sQuery(id+"F8.wireOp",VERTEX,"E46");
            var Q8;
            Q8=makeQuery(id+"F1.opExtrude","SWEPT_BODY",BODY,{"disambiguationData":[OSD([sQuery(id+"F0.wireOp",EDGE,"E2.MirrorCS"),sQuery(id+"F0.wireOp",EDGE,"E3.MirrorCS"),sQuery(id+"F0.wireOp",EDGE,"E6.filletArc"),sQuery(id+"F0.wireOp",EDGE,"E7.filletArc"),sQuery(id+"F0.wireOp",EDGE,"E8.filletArc"),sQuery(id+"F0.wireOp",EDGE,"E9.filletArc"),sQuery(id+"F0.wireOp",EDGE,"E10"),sQuery(id+"F0.wireOp",EDGE,"E11"),sQuery(id+"F0.wireOp",EDGE,"E12"),sQuery(id+"F0.wireOp",EDGE,"E15"),sQuery(id+"F0.wireOp",EDGE,"E16.1.0.1"),sQuery(id+"F0.wireOp",EDGE,"E16.1.0.2"),sQuery(id+"F0.wireOp",EDGE,"E16.1.0.7"),sQuery(id+"F0.wireOp",EDGE,"E16.1.0.9"),sQuery(id+"F0.wireOp",EDGE,"E16.1.0.10"),sQuery(id+"F0.wireOp",EDGE,"E16.1.0.12"),sQuery(id+"F0.wireOp",EDGE,"E16.1.0.13"),sQuery(id+"F0.wireOp",EDGE,"E16.1.0.14"),sQuery(id+"F0.wireOp",EDGE,"E16.1.0.16"),sQuery(id+"F0.wireOp",EDGE,"E16.1.0.17"),sQuery(id+"F0.wireOp",EDGE,"E16.2.0.1"),sQuery(id+"F0.wireOp",EDGE,"E16.2.0.2"),sQuery(id+"F0.wireOp",EDGE,"E16.2.0.7"),sQuery(id+"F0.wireOp",EDGE,"E16.2.0.9"),sQuery(id+"F0.wireOp",EDGE,"E16.2.0.10"),sQuery(id+"F0.wireOp",EDGE,"E16.2.0.12"),sQuery(id+"F0.wireOp",EDGE,"E16.2.0.13"),sQuery(id+"F0.wireOp",EDGE,"E16.2.0.14"),sQuery(id+"F0.wireOp",EDGE,"E16.2.0.16"),sQuery(id+"F0.wireOp",EDGE,"E16.2.0.17"),sQuery(id+"F0.wireOp",EDGE,"E17.1.3.0"),sQuery(id+"F0.wireOp",EDGE,"E17.5.3.0"),sQuery(id+"F0.wireOp",EDGE,"E17.13.3.0"),sQuery(id+"F0.wireOp",EDGE,"E17.17.3.0"),sQuery(id+"F0.wireOp",EDGE,"E17.20.3.0"),sQuery(id+"F0.wireOp",EDGE,"E17.24.3.0"),sQuery(id+"F0.wireOp",EDGE,"E17.27.3.0"),sQuery(id+"F0.wireOp",EDGE,"E17.31.3.0"),sQuery(id+"F0.wireOp",EDGE,"E17.38.3.0"),sQuery(id+"F0.wireOp",EDGE,"E17.42.3.0"),sQuery(id+"F0.wireOp",EDGE,"E17.1.4.0"),sQuery(id+"F0.wireOp",EDGE,"E17.5.4.0"),sQuery(id+"F0.wireOp",EDGE,"E17.13.4.0"),sQuery(id+"F0.wireOp",EDGE,"E17.17.4.0"),sQuery(id+"F0.wireOp",EDGE,"E17.20.4.0"),sQuery(id+"F0.wireOp",EDGE,"E17.24.4.0"),sQuery(id+"F0.wireOp",EDGE,"E17.27.4.0"),sQuery(id+"F0.wireOp",EDGE,"E17.31.4.0"),sQuery(id+"F0.wireOp",EDGE,"E17.38.4.0"),sQuery(id+"F0.wireOp",EDGE,"E17.42.4.0"),sQuery(id+"F0.wireOp",EDGE,"E17.1.5.0"),sQuery(id+"F0.wireOp",EDGE,"E17.5.5.0"),sQuery(id+"F0.wireOp",EDGE,"E17.13.5.0"),sQuery(id+"F0.wireOp",EDGE,"E17.17.5.0"),sQuery(id+"F0.wireOp",EDGE,"E17.20.5.0"),sQuery(id+"F0.wireOp",EDGE,"E17.24.5.0"),sQuery(id+"F0.wireOp",EDGE,"E17.27.5.0"),sQuery(id+"F0.wireOp",EDGE,"E17.31.5.0"),sQuery(id+"F0.wireOp",EDGE,"E17.38.5.0"),sQuery(id+"F0.wireOp",EDGE,"E17.42.5.0"),sQuery(id+"F0.wireOp",EDGE,"E17.1.6.0"),sQuery(id+"F0.wireOp",EDGE,"E17.5.6.0"),sQuery(id+"F0.wireOp",EDGE,"E17.13.6.0"),sQuery(id+"F0.wireOp",EDGE,"E17.17.6.0"),sQuery(id+"F0.wireOp",EDGE,"E17.20.6.0"),sQuery(id+"F0.wireOp",EDGE,"E17.24.6.0"),sQuery(id+"F0.wireOp",EDGE,"E17.27.6.0"),sQuery(id+"F0.wireOp",EDGE,"E17.31.6.0"),sQuery(id+"F0.wireOp",EDGE,"E17.38.6.0"),sQuery(id+"F0.wireOp",EDGE,"E17.42.6.0"),sQuery(id+"F0.wireOp",EDGE,"E17.1.7.0"),sQuery(id+"F0.wireOp",EDGE,"E17.5.7.0"),sQuery(id+"F0.wireOp",EDGE,"E17.13.7.0"),sQuery(id+"F0.wireOp",EDGE,"E17.17.7.0"),sQuery(id+"F0.wireOp",EDGE,"E17.20.7.0"),sQuery(id+"F0.wireOp",EDGE,"E17.24.7.0"),sQuery(id+"F0.wireOp",EDGE,"E17.27.7.0"),sQuery(id+"F0.wireOp",EDGE,"E17.31.7.0"),sQuery(id+"F0.wireOp",EDGE,"E17.38.7.0"),sQuery(id+"F0.wireOp",EDGE,"E17.42.7.0"),sQuery(id+"F0.wireOp",EDGE,"E17.1.8.0"),sQuery(id+"F0.wireOp",EDGE,"E17.5.8.0"),sQuery(id+"F0.wireOp",EDGE,"E17.13.8.0"),sQuery(id+"F0.wireOp",EDGE,"E17.17.8.0"),sQuery(id+"F0.wireOp",EDGE,"E17.20.8.0"),sQuery(id+"F0.wireOp",EDGE,"E17.24.8.0"),sQuery(id+"F0.wireOp",EDGE,"E17.27.8.0"),sQuery(id+"F0.wireOp",EDGE,"E17.31.8.0"),sQuery(id+"F0.wireOp",EDGE,"E17.38.8.0"),sQuery(id+"F0.wireOp",EDGE,"E17.42.8.0"),sQuery(id+"F0.wireOp",EDGE,"E17.1.9.0"),sQuery(id+"F0.wireOp",EDGE,"E17.5.9.0"),sQuery(id+"F0.wireOp",EDGE,"E17.13.9.0"),sQuery(id+"F0.wireOp",EDGE,"E17.17.9.0"),sQuery(id+"F0.wireOp",EDGE,"E17.20.9.0"),sQuery(id+"F0.wireOp",EDGE,"E17.24.9.0"),sQuery(id+"F0.wireOp",EDGE,"E17.27.9.0"),sQuery(id+"F0.wireOp",EDGE,"E17.31.9.0"),sQuery(id+"F0.wireOp",EDGE,"E17.38.9.0"),sQuery(id+"F0.wireOp",EDGE,"E17.42.9.0"),sQuery(id+"F0.wireOp",EDGE,"E17.1.10.0"),sQuery(id+"F0.wireOp",EDGE,"E17.5.10.0"),sQuery(id+"F0.wireOp",EDGE,"E17.13.10.0"),sQuery(id+"F0.wireOp",EDGE,"E17.17.10.0"),sQuery(id+"F0.wireOp",EDGE,"E17.20.10.0"),sQuery(id+"F0.wireOp",EDGE,"E17.24.10.0"),sQuery(id+"F0.wireOp",EDGE,"E17.27.10.0"),sQuery(id+"F0.wireOp",EDGE,"E17.31.10.0"),sQuery(id+"F0.wireOp",EDGE,"E17.38.10.0"),sQuery(id+"F0.wireOp",EDGE,"E17.42.10.0"),sQuery(id+"F0.wireOp",EDGE,"E17.1.11.0"),sQuery(id+"F0.wireOp",EDGE,"E17.5.11.0"),sQuery(id+"F0.wireOp",EDGE,"E17.13.11.0"),sQuery(id+"F0.wireOp",EDGE,"E17.17.11.0"),sQuery(id+"F0.wireOp",EDGE,"E17.20.11.0"),sQuery(id+"F0.wireOp",EDGE,"E17.24.11.0"),sQuery(id+"F0.wireOp",EDGE,"E17.27.11.0"),sQuery(id+"F0.wireOp",EDGE,"E17.31.11.0"),sQuery(id+"F0.wireOp",EDGE,"E17.38.11.0"),sQuery(id+"F0.wireOp",EDGE,"E17.42.11.0"),sQuery(id+"F0.wireOp",EDGE,"E17.1.12.0"),sQuery(id+"F0.wireOp",EDGE,"E17.5.12.0"),sQuery(id+"F0.wireOp",EDGE,"E17.13.12.0"),sQuery(id+"F0.wireOp",EDGE,"E17.17.12.0"),sQuery(id+"F0.wireOp",EDGE,"E17.20.12.0"),sQuery(id+"F0.wireOp",EDGE,"E17.24.12.0"),sQuery(id+"F0.wireOp",EDGE,"E17.27.12.0"),sQuery(id+"F0.wireOp",EDGE,"E17.31.12.0"),sQuery(id+"F0.wireOp",EDGE,"E17.38.12.0"),sQuery(id+"F0.wireOp",EDGE,"E17.42.12.0"),sQuery(id+"F0.wireOp",EDGE,"E17.1.13.0"),sQuery(id+"F0.wireOp",EDGE,"E17.5.13.0"),sQuery(id+"F0.wireOp",EDGE,"E17.13.13.0"),sQuery(id+"F0.wireOp",EDGE,"E17.17.13.0"),sQuery(id+"F0.wireOp",EDGE,"E17.20.13.0"),sQuery(id+"F0.wireOp",EDGE,"E17.24.13.0"),sQuery(id+"F0.wireOp",EDGE,"E17.27.13.0"),sQuery(id+"F0.wireOp",EDGE,"E17.31.13.0"),sQuery(id+"F0.wireOp",EDGE,"E17.38.13.0"),sQuery(id+"F0.wireOp",EDGE,"E17.42.13.0"),sQuery(id+"F0.wireOp",EDGE,"E17.1.14.0"),sQuery(id+"F0.wireOp",EDGE,"E17.5.14.0"),sQuery(id+"F0.wireOp",EDGE,"E17.13.14.0"),sQuery(id+"F0.wireOp",EDGE,"E17.17.14.0"),sQuery(id+"F0.wireOp",EDGE,"E17.20.14.0"),sQuery(id+"F0.wireOp",EDGE,"E17.24.14.0"),sQuery(id+"F0.wireOp",EDGE,"E17.27.14.0"),sQuery(id+"F0.wireOp",EDGE,"E17.31.14.0"),sQuery(id+"F0.wireOp",EDGE,"E17.38.14.0"),sQuery(id+"F0.wireOp",EDGE,"E17.42.14.0"),sQuery(id+"F0.wireOp",EDGE,"E17.1.15.0"),sQuery(id+"F0.wireOp",EDGE,"E17.5.15.0"),sQuery(id+"F0.wireOp",EDGE,"E17.13.15.0"),sQuery(id+"F0.wireOp",EDGE,"E17.17.15.0"),sQuery(id+"F0.wireOp",EDGE,"E17.20.15.0"),sQuery(id+"F0.wireOp",EDGE,"E17.24.15.0"),sQuery(id+"F0.wireOp",EDGE,"E17.27.15.0"),sQuery(id+"F0.wireOp",EDGE,"E17.31.15.0"),sQuery(id+"F0.wireOp",EDGE,"E17.38.15.0"),sQuery(id+"F0.wireOp",EDGE,"E17.42.15.0"),sQuery(id+"F0.wireOp",EDGE,"E17.1.16.0"),sQuery(id+"F0.wireOp",EDGE,"E17.5.16.0"),sQuery(id+"F0.wireOp",EDGE,"E17.13.16.0"),sQuery(id+"F0.wireOp",EDGE,"E17.17.16.0"),sQuery(id+"F0.wireOp",EDGE,"E17.20.16.0"),sQuery(id+"F0.wireOp",EDGE,"E17.24.16.0"),sQuery(id+"F0.wireOp",EDGE,"E17.27.16.0"),sQuery(id+"F0.wireOp",EDGE,"E17.31.16.0"),sQuery(id+"F0.wireOp",EDGE,"E17.38.16.0"),sQuery(id+"F0.wireOp",EDGE,"E17.42.16.0"),sQuery(id+"F0.wireOp",EDGE,"E17.1.17.0"),sQuery(id+"F0.wireOp",EDGE,"E17.5.17.0"),sQuery(id+"F0.wireOp",EDGE,"E17.13.17.0"),sQuery(id+"F0.wireOp",EDGE,"E17.17.17.0"),sQuery(id+"F0.wireOp",EDGE,"E17.20.17.0"),sQuery(id+"F0.wireOp",EDGE,"E17.24.17.0"),sQuery(id+"F0.wireOp",EDGE,"E17.27.17.0"),sQuery(id+"F0.wireOp",EDGE,"E17.31.17.0"),sQuery(id+"F0.wireOp",EDGE,"E17.38.17.0"),sQuery(id+"F0.wireOp",EDGE,"E17.42.17.0"),sQuery(id+"F0.wireOp",EDGE,"E17.1.18.0"),sQuery(id+"F0.wireOp",EDGE,"E17.5.18.0"),sQuery(id+"F0.wireOp",EDGE,"E17.13.18.0"),sQuery(id+"F0.wireOp",EDGE,"E17.17.18.0"),sQuery(id+"F0.wireOp",EDGE,"E17.20.18.0"),sQuery(id+"F0.wireOp",EDGE,"E17.24.18.0"),sQuery(id+"F0.wireOp",EDGE,"E17.27.18.0"),sQuery(id+"F0.wireOp",EDGE,"E17.31.18.0"),sQuery(id+"F0.wireOp",EDGE,"E17.38.18.0"),sQuery(id+"F0.wireOp",EDGE,"E17.42.18.0"),sQuery(id+"F0.wireOp",EDGE,"E17.1.19.0"),sQuery(id+"F0.wireOp",EDGE,"E17.5.19.0"),sQuery(id+"F0.wireOp",EDGE,"E17.13.19.0"),sQuery(id+"F0.wireOp",EDGE,"E17.17.19.0"),sQuery(id+"F0.wireOp",EDGE,"E17.20.19.0"),sQuery(id+"F0.wireOp",EDGE,"E17.24.19.0"),sQuery(id+"F0.wireOp",EDGE,"E17.27.19.0"),sQuery(id+"F0.wireOp",EDGE,"E17.31.19.0"),sQuery(id+"F0.wireOp",EDGE,"E17.38.19.0"),sQuery(id+"F0.wireOp",EDGE,"E17.42.19.0"),sQuery(id+"F0.wireOp",EDGE,"E17.1.20.0"),sQuery(id+"F0.wireOp",EDGE,"E17.5.20.0"),sQuery(id+"F0.wireOp",EDGE,"E17.13.20.0"),sQuery(id+"F0.wireOp",EDGE,"E17.17.20.0"),sQuery(id+"F0.wireOp",EDGE,"E17.20.20.0"),sQuery(id+"F0.wireOp",EDGE,"E17.24.20.0"),sQuery(id+"F0.wireOp",EDGE,"E17.27.20.0"),sQuery(id+"F0.wireOp",EDGE,"E17.31.20.0"),sQuery(id+"F0.wireOp",EDGE,"E17.38.20.0"),sQuery(id+"F0.wireOp",EDGE,"E17.42.20.0"),sQuery(id+"F0.wireOp",EDGE,"E17.1.21.0"),sQuery(id+"F0.wireOp",EDGE,"E17.5.21.0"),sQuery(id+"F0.wireOp",EDGE,"E17.13.21.0"),sQuery(id+"F0.wireOp",EDGE,"E17.17.21.0"),sQuery(id+"F0.wireOp",EDGE,"E17.20.21.0"),sQuery(id+"F0.wireOp",EDGE,"E17.24.21.0"),sQuery(id+"F0.wireOp",EDGE,"E17.27.21.0"),sQuery(id+"F0.wireOp",EDGE,"E17.31.21.0"),sQuery(id+"F0.wireOp",EDGE,"E17.38.21.0"),sQuery(id+"F0.wireOp",EDGE,"E17.42.21.0"),sQuery(id+"F0.wireOp",EDGE,"E17.1.22.0"),sQuery(id+"F0.wireOp",EDGE,"E17.5.22.0"),sQuery(id+"F0.wireOp",EDGE,"E17.13.22.0"),sQuery(id+"F0.wireOp",EDGE,"E17.17.22.0"),sQuery(id+"F0.wireOp",EDGE,"E17.20.22.0"),sQuery(id+"F0.wireOp",EDGE,"E17.24.22.0"),sQuery(id+"F0.wireOp",EDGE,"E17.27.22.0"),sQuery(id+"F0.wireOp",EDGE,"E17.31.22.0"),sQuery(id+"F0.wireOp",EDGE,"E17.38.22.0"),sQuery(id+"F0.wireOp",EDGE,"E17.42.22.0"),sQuery(id+"F0.wireOp",EDGE,"E17.1.23.0"),sQuery(id+"F0.wireOp",EDGE,"E17.5.23.0"),sQuery(id+"F0.wireOp",EDGE,"E17.13.23.0"),sQuery(id+"F0.wireOp",EDGE,"E17.17.23.0"),sQuery(id+"F0.wireOp",EDGE,"E17.20.23.0"),sQuery(id+"F0.wireOp",EDGE,"E17.24.23.0"),sQuery(id+"F0.wireOp",EDGE,"E17.27.23.0"),sQuery(id+"F0.wireOp",EDGE,"E17.31.23.0"),sQuery(id+"F0.wireOp",EDGE,"E17.38.23.0"),sQuery(id+"F0.wireOp",EDGE,"E17.42.23.0"),sQuery(id+"F0.wireOp",EDGE,"E17.1.24.0"),sQuery(id+"F0.wireOp",EDGE,"E17.5.24.0"),sQuery(id+"F0.wireOp",EDGE,"E17.13.24.0"),sQuery(id+"F0.wireOp",EDGE,"E17.17.24.0"),sQuery(id+"F0.wireOp",EDGE,"E17.20.24.0"),sQuery(id+"F0.wireOp",EDGE,"E17.24.24.0"),sQuery(id+"F0.wireOp",EDGE,"E17.27.24.0"),sQuery(id+"F0.wireOp",EDGE,"E17.31.24.0"),sQuery(id+"F0.wireOp",EDGE,"E17.38.24.0"),sQuery(id+"F0.wireOp",EDGE,"E17.42.24.0"),sQuery(id+"F0.wireOp",EDGE,"E17.1.25.0"),sQuery(id+"F0.wireOp",EDGE,"E17.5.25.0"),sQuery(id+"F0.wireOp",EDGE,"E17.13.25.0"),sQuery(id+"F0.wireOp",EDGE,"E17.17.25.0"),sQuery(id+"F0.wireOp",EDGE,"E17.20.25.0"),sQuery(id+"F0.wireOp",EDGE,"E17.24.25.0"),sQuery(id+"F0.wireOp",EDGE,"E17.27.25.0"),sQuery(id+"F0.wireOp",EDGE,"E17.31.25.0"),sQuery(id+"F0.wireOp",EDGE,"E17.38.25.0"),sQuery(id+"F0.wireOp",EDGE,"E17.42.25.0"),sQuery(id+"F0.wireOp",EDGE,"E17.1.26.0"),sQuery(id+"F0.wireOp",EDGE,"E17.5.26.0"),sQuery(id+"F0.wireOp",EDGE,"E17.13.26.0"),sQuery(id+"F0.wireOp",EDGE,"E17.17.26.0"),sQuery(id+"F0.wireOp",EDGE,"E17.20.26.0"),sQuery(id+"F0.wireOp",EDGE,"E17.24.26.0"),sQuery(id+"F0.wireOp",EDGE,"E17.27.26.0"),sQuery(id+"F0.wireOp",EDGE,"E17.31.26.0"),sQuery(id+"F0.wireOp",EDGE,"E17.38.26.0"),sQuery(id+"F0.wireOp",EDGE,"E17.42.26.0"),sQuery(id+"F0.wireOp",EDGE,"E17.1.27.0"),sQuery(id+"F0.wireOp",EDGE,"E17.5.27.0"),sQuery(id+"F0.wireOp",EDGE,"E17.13.27.0"),sQuery(id+"F0.wireOp",EDGE,"E17.17.27.0"),sQuery(id+"F0.wireOp",EDGE,"E17.20.27.0"),sQuery(id+"F0.wireOp",EDGE,"E17.24.27.0"),sQuery(id+"F0.wireOp",EDGE,"E17.27.27.0"),sQuery(id+"F0.wireOp",EDGE,"E17.31.27.0"),sQuery(id+"F0.wireOp",EDGE,"E17.38.27.0"),sQuery(id+"F0.wireOp",EDGE,"E17.42.27.0"),sQuery(id+"F0.wireOp",EDGE,"E17.1.28.0"),sQuery(id+"F0.wireOp",EDGE,"E17.5.28.0"),sQuery(id+"F0.wireOp",EDGE,"E17.13.28.0"),sQuery(id+"F0.wireOp",EDGE,"E17.17.28.0"),sQuery(id+"F0.wireOp",EDGE,"E17.20.28.0"),sQuery(id+"F0.wireOp",EDGE,"E17.24.28.0"),sQuery(id+"F0.wireOp",EDGE,"E17.27.28.0"),sQuery(id+"F0.wireOp",EDGE,"E17.31.28.0"),sQuery(id+"F0.wireOp",EDGE,"E17.38.28.0"),sQuery(id+"F0.wireOp",EDGE,"E17.42.28.0"),sQuery(id+"F0.wireOp",EDGE,"E17.1.29.0"),sQuery(id+"F0.wireOp",EDGE,"E17.5.29.0"),sQuery(id+"F0.wireOp",EDGE,"E17.13.29.0"),sQuery(id+"F0.wireOp",EDGE,"E17.17.29.0"),sQuery(id+"F0.wireOp",EDGE,"E17.20.29.0"),sQuery(id+"F0.wireOp",EDGE,"E17.24.29.0"),sQuery(id+"F0.wireOp",EDGE,"E17.27.29.0"),sQuery(id+"F0.wireOp",EDGE,"E17.31.29.0"),sQuery(id+"F0.wireOp",EDGE,"E17.38.29.0"),sQuery(id+"F0.wireOp",EDGE,"E17.42.29.0"),sQuery(id+"F0.wireOp",EDGE,"E17.1.30.0"),sQuery(id+"F0.wireOp",EDGE,"E17.5.30.0"),sQuery(id+"F0.wireOp",EDGE,"E17.13.30.0"),sQuery(id+"F0.wireOp",EDGE,"E17.17.30.0"),sQuery(id+"F0.wireOp",EDGE,"E17.20.30.0"),sQuery(id+"F0.wireOp",EDGE,"E17.24.30.0"),sQuery(id+"F0.wireOp",EDGE,"E17.27.30.0"),sQuery(id+"F0.wireOp",EDGE,"E17.31.30.0"),sQuery(id+"F0.wireOp",EDGE,"E17.38.30.0"),sQuery(id+"F0.wireOp",EDGE,"E17.42.30.0"),sQuery(id+"F0.wireOp",EDGE,"E17.1.31.0"),sQuery(id+"F0.wireOp",EDGE,"E17.5.31.0"),sQuery(id+"F0.wireOp",EDGE,"E17.13.31.0"),sQuery(id+"F0.wireOp",EDGE,"E17.17.31.0"),sQuery(id+"F0.wireOp",EDGE,"E17.20.31.0"),sQuery(id+"F0.wireOp",EDGE,"E17.24.31.0"),sQuery(id+"F0.wireOp",EDGE,"E17.27.31.0"),sQuery(id+"F0.wireOp",EDGE,"E17.31.31.0"),sQuery(id+"F0.wireOp",EDGE,"E17.38.31.0"),sQuery(id+"F0.wireOp",EDGE,"E17.42.31.0"),sQuery(id+"F0.wireOp",EDGE,"E17.1.32.0"),sQuery(id+"F0.wireOp",EDGE,"E17.5.32.0"),sQuery(id+"F0.wireOp",EDGE,"E17.13.32.0"),sQuery(id+"F0.wireOp",EDGE,"E17.17.32.0"),sQuery(id+"F0.wireOp",EDGE,"E17.20.32.0"),sQuery(id+"F0.wireOp",EDGE,"E17.24.32.0"),sQuery(id+"F0.wireOp",EDGE,"E17.27.32.0"),sQuery(id+"F0.wireOp",EDGE,"E17.31.32.0"),sQuery(id+"F0.wireOp",EDGE,"E17.38.32.0"),sQuery(id+"F0.wireOp",EDGE,"E17.42.32.0"),sQuery(id+"F0.wireOp",EDGE,"E17.1.33.0"),sQuery(id+"F0.wireOp",EDGE,"E17.5.33.0"),sQuery(id+"F0.wireOp",EDGE,"E17.13.33.0"),sQuery(id+"F0.wireOp",EDGE,"E17.17.33.0"),sQuery(id+"F0.wireOp",EDGE,"E17.20.33.0"),sQuery(id+"F0.wireOp",EDGE,"E17.24.33.0"),sQuery(id+"F0.wireOp",EDGE,"E17.27.33.0"),sQuery(id+"F0.wireOp",EDGE,"E17.31.33.0"),sQuery(id+"F0.wireOp",EDGE,"E17.38.33.0"),sQuery(id+"F0.wireOp",EDGE,"E17.42.33.0"),sQuery(id+"F0.wireOp",EDGE,"E17.1.34.0"),sQuery(id+"F0.wireOp",EDGE,"E17.5.34.0"),sQuery(id+"F0.wireOp",EDGE,"E17.13.34.0"),sQuery(id+"F0.wireOp",EDGE,"E17.17.34.0"),sQuery(id+"F0.wireOp",EDGE,"E17.20.34.0"),sQuery(id+"F0.wireOp",EDGE,"E17.24.34.0"),sQuery(id+"F0.wireOp",EDGE,"E17.27.34.0"),sQuery(id+"F0.wireOp",EDGE,"E17.31.34.0"),sQuery(id+"F0.wireOp",EDGE,"E17.38.34.0"),sQuery(id+"F0.wireOp",EDGE,"E17.42.34.0"),sQuery(id+"F0.wireOp",EDGE,"E17.1.35.0"),sQuery(id+"F0.wireOp",EDGE,"E17.5.35.0"),sQuery(id+"F0.wireOp",EDGE,"E17.13.35.0"),sQuery(id+"F0.wireOp",EDGE,"E17.17.35.0"),sQuery(id+"F0.wireOp",EDGE,"E17.20.35.0"),sQuery(id+"F0.wireOp",EDGE,"E17.24.35.0"),sQuery(id+"F0.wireOp",EDGE,"E17.27.35.0"),sQuery(id+"F0.wireOp",EDGE,"E17.31.35.0"),sQuery(id+"F0.wireOp",EDGE,"E17.38.35.0"),sQuery(id+"F0.wireOp",EDGE,"E17.42.35.0"),sQuery(id+"F0.wireOp",EDGE,"E17.1.36.0"),sQuery(id+"F0.wireOp",EDGE,"E17.5.36.0"),sQuery(id+"F0.wireOp",EDGE,"E17.13.36.0"),sQuery(id+"F0.wireOp",EDGE,"E17.17.36.0"),sQuery(id+"F0.wireOp",EDGE,"E17.20.36.0"),sQuery(id+"F0.wireOp",EDGE,"E17.24.36.0"),sQuery(id+"F0.wireOp",EDGE,"E17.27.36.0"),sQuery(id+"F0.wireOp",EDGE,"E17.31.36.0"),sQuery(id+"F0.wireOp",EDGE,"E17.38.36.0"),sQuery(id+"F0.wireOp",EDGE,"E17.42.36.0"),sQuery(id+"F0.wireOp",EDGE,"E17.1.37.0"),sQuery(id+"F0.wireOp",EDGE,"E17.5.37.0"),sQuery(id+"F0.wireOp",EDGE,"E17.13.37.0"),sQuery(id+"F0.wireOp",EDGE,"E17.17.37.0"),sQuery(id+"F0.wireOp",EDGE,"E17.20.37.0"),sQuery(id+"F0.wireOp",EDGE,"E17.24.37.0"),sQuery(id+"F0.wireOp",EDGE,"E17.27.37.0"),sQuery(id+"F0.wireOp",EDGE,"E17.31.37.0"),sQuery(id+"F0.wireOp",EDGE,"E17.38.37.0"),sQuery(id+"F0.wireOp",EDGE,"E17.42.37.0"),sQuery(id+"F0.wireOp",EDGE,"E17.1.38.0"),sQuery(id+"F0.wireOp",EDGE,"E17.5.38.0"),sQuery(id+"F0.wireOp",EDGE,"E17.13.38.0"),sQuery(id+"F0.wireOp",EDGE,"E17.17.38.0"),sQuery(id+"F0.wireOp",EDGE,"E17.20.38.0"),sQuery(id+"F0.wireOp",EDGE,"E17.24.38.0"),sQuery(id+"F0.wireOp",EDGE,"E17.27.38.0"),sQuery(id+"F0.wireOp",EDGE,"E17.31.38.0"),sQuery(id+"F0.wireOp",EDGE,"E17.38.38.0"),sQuery(id+"F0.wireOp",EDGE,"E17.42.38.0"),sQuery(id+"F0.wireOp",EDGE,"E17.1.39.0"),sQuery(id+"F0.wireOp",EDGE,"E17.5.39.0"),sQuery(id+"F0.wireOp",EDGE,"E17.13.39.0"),sQuery(id+"F0.wireOp",EDGE,"E17.17.39.0"),sQuery(id+"F0.wireOp",EDGE,"E17.20.39.0"),sQuery(id+"F0.wireOp",EDGE,"E17.24.39.0"),sQuery(id+"F0.wireOp",EDGE,"E17.27.39.0"),sQuery(id+"F0.wireOp",EDGE,"E17.31.39.0"),sQuery(id+"F0.wireOp",EDGE,"E17.38.39.0"),sQuery(id+"F0.wireOp",EDGE,"E17.42.39.0"),sQuery(id+"F0.wireOp",EDGE,"E17.1.40.0"),sQuery(id+"F0.wireOp",EDGE,"E17.5.40.0"),sQuery(id+"F0.wireOp",EDGE,"E17.13.40.0"),sQuery(id+"F0.wireOp",EDGE,"E17.17.40.0"),sQuery(id+"F0.wireOp",EDGE,"E17.20.40.0"),sQuery(id+"F0.wireOp",EDGE,"E17.24.40.0"),sQuery(id+"F0.wireOp",EDGE,"E17.27.40.0"),sQuery(id+"F0.wireOp",EDGE,"E17.31.40.0"),sQuery(id+"F0.wireOp",EDGE,"E17.38.40.0"),sQuery(id+"F0.wireOp",EDGE,"E17.42.40.0"),sQuery(id+"F0.wireOp",EDGE,"E17.1.41.0"),sQuery(id+"F0.wireOp",EDGE,"E17.5.41.0"),sQuery(id+"F0.wireOp",EDGE,"E17.13.41.0"),sQuery(id+"F0.wireOp",EDGE,"E17.17.41.0"),sQuery(id+"F0.wireOp",EDGE,"E17.20.41.0"),sQuery(id+"F0.wireOp",EDGE,"E17.24.41.0"),sQuery(id+"F0.wireOp",EDGE,"E17.27.41.0"),sQuery(id+"F0.wireOp",EDGE,"E17.31.41.0"),sQuery(id+"F0.wireOp",EDGE,"E17.38.41.0"),sQuery(id+"F0.wireOp",EDGE,"E17.42.41.0"),sQuery(id+"F0.wireOp",EDGE,"E17.1.42.0"),sQuery(id+"F0.wireOp",EDGE,"E17.5.42.0"),sQuery(id+"F0.wireOp",EDGE,"E17.13.42.0"),sQuery(id+"F0.wireOp",EDGE,"E17.17.42.0"),sQuery(id+"F0.wireOp",EDGE,"E17.20.42.0"),sQuery(id+"F0.wireOp",EDGE,"E17.24.42.0"),sQuery(id+"F0.wireOp",EDGE,"E17.27.42.0"),sQuery(id+"F0.wireOp",EDGE,"E17.31.42.0"),sQuery(id+"F0.wireOp",EDGE,"E17.38.42.0"),sQuery(id+"F0.wireOp",EDGE,"E17.42.42.0"),sQuery(id+"F0.wireOp",EDGE,"E17.1.43.0"),sQuery(id+"F0.wireOp",EDGE,"E17.5.43.0"),sQuery(id+"F0.wireOp",EDGE,"E17.13.43.0"),sQuery(id+"F0.wireOp",EDGE,"E17.17.43.0"),sQuery(id+"F0.wireOp",EDGE,"E17.20.43.0"),sQuery(id+"F0.wireOp",EDGE,"E17.24.43.0"),sQuery(id+"F0.wireOp",EDGE,"E17.27.43.0"),sQuery(id+"F0.wireOp",EDGE,"E17.31.43.0"),sQuery(id+"F0.wireOp",EDGE,"E17.38.43.0"),sQuery(id+"F0.wireOp",EDGE,"E17.42.43.0"),sQuery(id+"F0.wireOp",EDGE,"E17.1.44.0"),sQuery(id+"F0.wireOp",EDGE,"E17.5.44.0"),sQuery(id+"F0.wireOp",EDGE,"E17.13.44.0"),sQuery(id+"F0.wireOp",EDGE,"E17.17.44.0"),sQuery(id+"F0.wireOp",EDGE,"E17.20.44.0"),sQuery(id+"F0.wireOp",EDGE,"E17.24.44.0"),sQuery(id+"F0.wireOp",EDGE,"E17.27.44.0"),sQuery(id+"F0.wireOp",EDGE,"E17.31.44.0"),sQuery(id+"F0.wireOp",EDGE,"E17.38.44.0"),sQuery(id+"F0.wireOp",EDGE,"E17.42.44.0"),sQuery(id+"F0.wireOp",EDGE,"E17.1.45.0"),sQuery(id+"F0.wireOp",EDGE,"E17.5.45.0"),sQuery(id+"F0.wireOp",EDGE,"E17.13.45.0"),sQuery(id+"F0.wireOp",EDGE,"E17.17.45.0"),sQuery(id+"F0.wireOp",EDGE,"E17.20.45.0"),sQuery(id+"F0.wireOp",EDGE,"E17.24.45.0"),sQuery(id+"F0.wireOp",EDGE,"E17.27.45.0"),sQuery(id+"F0.wireOp",EDGE,"E17.31.45.0"),sQuery(id+"F0.wireOp",EDGE,"E17.38.45.0"),sQuery(id+"F0.wireOp",EDGE,"E17.42.45.0"),sQuery(id+"F0.wireOp",EDGE,"E17.1.46.0"),sQuery(id+"F0.wireOp",EDGE,"E17.5.46.0"),sQuery(id+"F0.wireOp",EDGE,"E17.13.46.0"),sQuery(id+"F0.wireOp",EDGE,"E17.17.46.0"),sQuery(id+"F0.wireOp",EDGE,"E17.20.46.0"),sQuery(id+"F0.wireOp",EDGE,"E17.24.46.0"),sQuery(id+"F0.wireOp",EDGE,"E17.27.46.0"),sQuery(id+"F0.wireOp",EDGE,"E17.31.46.0"),sQuery(id+"F0.wireOp",EDGE,"E17.38.46.0"),sQuery(id+"F0.wireOp",EDGE,"E17.42.46.0"),sQuery(id+"F0.wireOp",EDGE,"E17.1.47.0"),sQuery(id+"F0.wireOp",EDGE,"E17.5.47.0"),sQuery(id+"F0.wireOp",EDGE,"E17.13.47.0"),sQuery(id+"F0.wireOp",EDGE,"E17.17.47.0"),sQuery(id+"F0.wireOp",EDGE,"E17.20.47.0"),sQuery(id+"F0.wireOp",EDGE,"E17.24.47.0"),sQuery(id+"F0.wireOp",EDGE,"E17.27.47.0"),sQuery(id+"F0.wireOp",EDGE,"E17.31.47.0"),sQuery(id+"F0.wireOp",EDGE,"E17.38.47.0"),sQuery(id+"F0.wireOp",EDGE,"E17.42.47.0"),sQuery(id+"F0.wireOp",EDGE,"E17.1.48.0"),sQuery(id+"F0.wireOp",EDGE,"E17.5.48.0"),sQuery(id+"F0.wireOp",EDGE,"E17.13.48.0"),sQuery(id+"F0.wireOp",EDGE,"E17.17.48.0"),sQuery(id+"F0.wireOp",EDGE,"E17.20.48.0"),sQuery(id+"F0.wireOp",EDGE,"E17.24.48.0"),sQuery(id+"F0.wireOp",EDGE,"E17.27.48.0"),sQuery(id+"F0.wireOp",EDGE,"E17.31.48.0"),sQuery(id+"F0.wireOp",EDGE,"E17.38.48.0"),sQuery(id+"F0.wireOp",EDGE,"E17.42.48.0"),sQuery(id+"F0.wireOp",EDGE,"E17.1.49.0"),sQuery(id+"F0.wireOp",EDGE,"E17.5.49.0"),sQuery(id+"F0.wireOp",EDGE,"E17.13.49.0"),sQuery(id+"F0.wireOp",EDGE,"E17.17.49.0"),sQuery(id+"F0.wireOp",EDGE,"E17.24.49.0"),sQuery(id+"F0.wireOp",EDGE,"E17.27.49.0"),sQuery(id+"F0.wireOp",EDGE,"E17.31.49.0"),sQuery(id+"F0.wireOp",EDGE,"E17.38.49.0"),sQuery(id+"F0.wireOp",EDGE,"E17.42.49.0"),sQuery(id+"F0.wireOp",EDGE,"E18"),sQuery(id+"F0.wireOp",EDGE,"E19"),sQuery(id+"F0.wireOp",EDGE,"E20"),sQuery(id+"F0.wireOp",EDGE,"E21"),sQuery(id+"F0.wireOp",EDGE,"E24"),sQuery(id+"F0.wireOp",EDGE,"E25")])]});
            hole(context, id + "F11", {"style" : HoleStyle.C_BORE, "endStyle" : HoleEndStyle.THROUGH, "holeDiameter" : 4.83 * mm, "cBoreDiameter" : 10.16 * mm, "cBoreDepth" : 3.35 * mm, "tappedDepth" : 12.7 * mm, "tapClearance" : 3, "locations" : qUnion([Q0, Q1, Q2, Q3, Q4, Q5, Q6, Q7]), "scope" : qUnion([Q8])});
        }
    });
